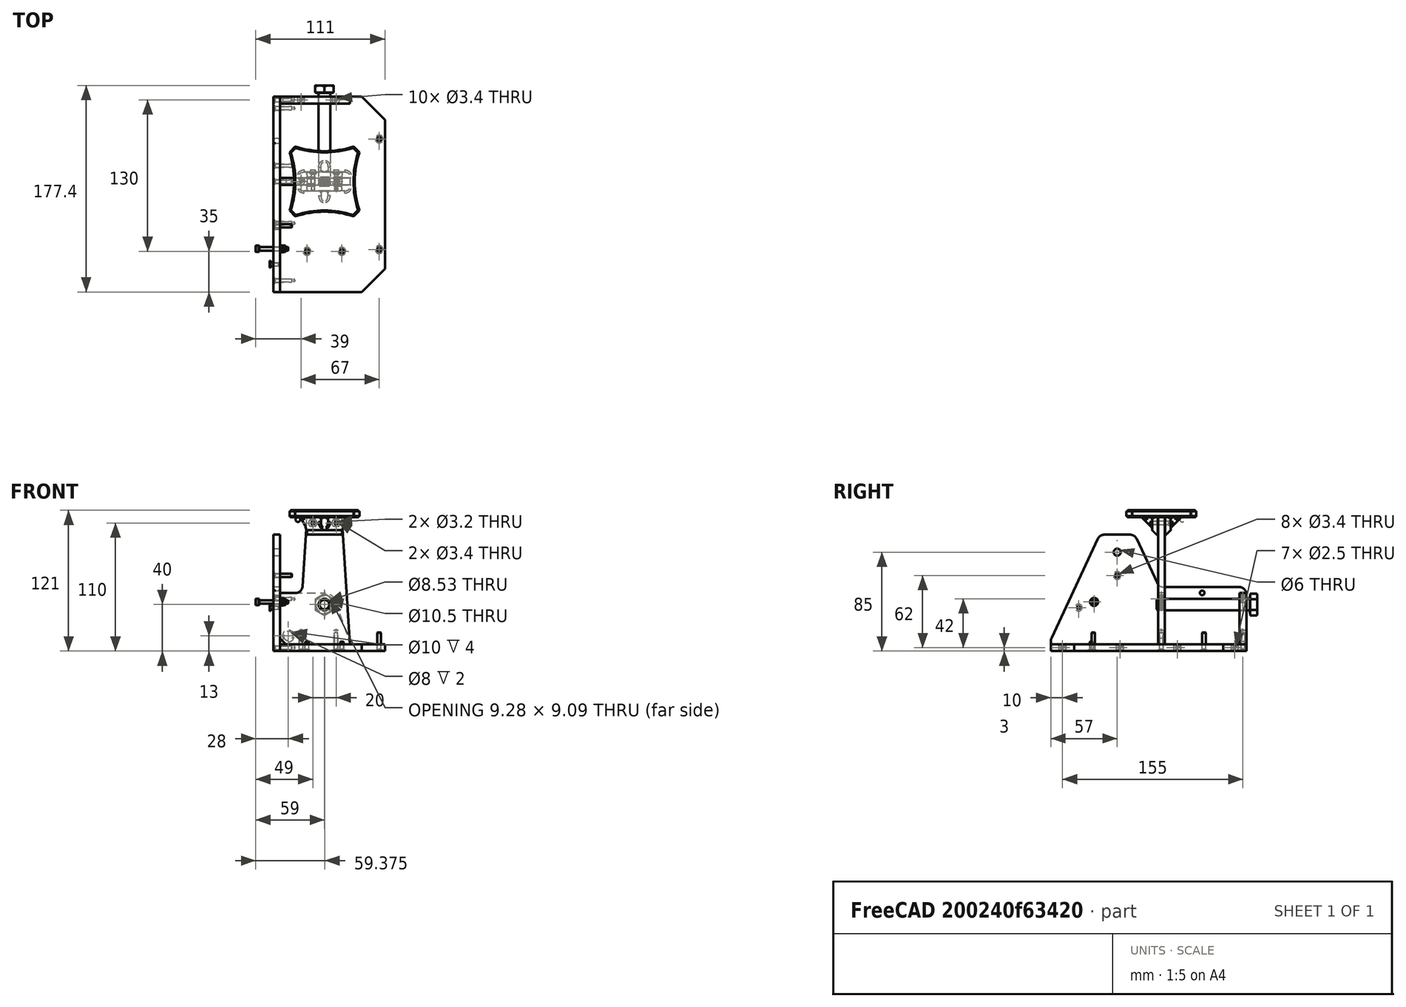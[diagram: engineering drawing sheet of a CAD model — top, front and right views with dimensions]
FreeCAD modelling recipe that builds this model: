
FCSTD DOCUMENT  (FreeCAD 0.20R28730 (Git))
Label: OpenSolder Stand
License: All rights reserved
LicenseURL: http://en.wikipedia.org/wiki/All_rights_reserved
objects: TechDraw::DrawViewBalloon×31, Sketcher::SketchObject×27, Part::FeaturePython×22, PartDesign::CoordinateSystem×21, App::Link×16, App::DocumentObjectGroup×15, PartDesign::Line×15, PartDesign::Hole×12, PartDesign::Pad×6, App::LinkElement×6, PartDesign::Body×5, PartDesign::Chamfer×5, PartDesign::Fillet×5, Spreadsheet::Sheet×5, PartDesign::Pocket×3, TechDraw::DrawSVGTemplate×3, TechDraw::DrawProjGroupItem×3, TechDraw::DrawViewPart×3, TechDraw::DrawViewDimension×3, TechDraw::DrawPage×3, +5 more types
note: 152 computed .brp shape members not serialized (recipe doc carries the construction recipe); baked Part::Feature solids carry a one-line shape summary decoded from their .brp
EXTERNAL_REF file=Parts/Tip Cleaner.FCStd obj=LCS_Tip_Cleaner_Hole_1
EXTERNAL_REF file=Parts/Tip Cleaner.FCStd obj=Body
EXTERNAL_REF file=Parts/Tip Remover Bracket.FCStd obj=Hole1001
EXTERNAL_REF file=Parts/Tip Remover Bracket.FCStd obj=Body
EXTERNAL_REF file=Parts/Tool Holder Washer.FCStd obj=Center
EXTERNAL_REF file=Parts/Tool Holder Washer.FCStd obj=Body
EXTERNAL_REF file=Parts/Tool Holder Screw.FCStd obj=LCS_1
EXTERNAL_REF file=Parts/Tool Holder Washer.FCStd obj=Center2
EXTERNAL_REF file=Parts/Tool Holder Screw.FCStd obj=Body
EXTERNAL_REF file=Parts/Tool Holder Adapter.FCStd obj=Mounting_face_main_hole
EXTERNAL_REF file=Parts/Tool Holder Adapter.FCStd obj=Body
EXTERNAL_REF file=Parts/Tool Holder.FCStd obj=LCS_1
EXTERNAL_REF file=Parts/Tool Holder Adapter.FCStd obj=Holder
EXTERNAL_REF file=Parts/Tool Holder.FCStd obj=Body
EXTERNAL_REF file=Parts/Tip Magazine.FCStd obj=Hole1
EXTERNAL_REF file=Parts/Tip Magazine.FCStd obj=Body009
EXTERNAL_REF file=Parts/Spool Dummy.FCStd obj=LCS_1
EXTERNAL_REF file=Parts/Spool Dummy.FCStd obj=Body
EXTERNAL_REF file=Parts/Spool Knob.FCStd obj=LCS_1
EXTERNAL_REF file=Parts/Spool Knob.FCStd obj=Body
EXTERNAL_REF file=Parts/Connector Minijack MJ-064H.FCStd obj=LCS_1
EXTERNAL_REF file=Parts/Connector Minijack MJ-064H.FCStd obj=Body
EXTERNAL_REF file=Parts/Tip Dummy.FCStd obj=Remover
EXTERNAL_REF file=Parts/Tip Remover Bracket.FCStd obj=LCS_Tip_Remover_Bracket_Tip_Attachment
EXTERNAL_REF file=Parts/Tip Dummy.FCStd obj=Body
EXTERNAL_REF file=Parts/Tip Dummy.FCStd obj=Tip_base
EXTERNAL_REF file=Parts/Tip Magazine.FCStd obj=Holder_pos_1
EXTERNAL_REF file=Parts/Tip Remover Bracket.FCStd obj=LCS_Tip_Remover_Bracket_Hole_2_Outside
EXTERNAL_REF file=Parts/Spool Knob.FCStd obj=LCS_Spool_Screw_Knob_2
EXTERNAL_REF file=Parts/Tip Remover Bracket.FCStd obj=LCS_Tip_Remover_Bracket_Hole_1_Outside
EXTERNAL_REF file=Parts/Rubber Pad.FCStd obj=LCS_1
EXTERNAL_REF file=Parts/Rubber Pad.FCStd obj=Body

FEATURE [PartDesign::CoordinateSystem] LCS_Origin
  AttacherType = Attacher::AttachEngine3D
  MapMode = 2
  Support = -> [X_Axis]
FEATURE [App::FeaturePython] Variables  # WARN: FeaturePython — macro-defined, semantics opaque (R4)
  Centerline_Offset = 38
  Front_Edge_Angle = 65
  Handle_Screw_Height = 110
  Hole_Depth = 12
  Length = 168
  Mid_Panel_Offset = -98
  Panel_Thickness = 6
  Spool_Holder_Inside_Length = 64
  Tool_Angle = 20
  Type = App::PropertyContainer
  expr: Mid_Panel_Offset = -(Length - Spool_Holder_Inside_Length - Panel_Thickness)
FEATURE [App::DocumentObjectGroup] Constraints
FEATURE [Sketcher::SketchObject] Sketch014  label="Master_Side_Sketch"
  FullyConstrained = true
  MapMode = 5
  Placement = pos=(0,0,0) rot=(0.57735,0.57735,0.57735;2.0944rad)
  Support = -> [YZ_Plane]
  expr: Constraints[15] = Variables.Length
  expr: Constraints[45] = Variables.Panel_Thickness / 2
  expr: Constraints[48] = Variables.Panel_Thickness / 2
  expr: Constraints[49] = Variables.Spool_Holder_Inside_Length + Variables.Panel_Thickness
  expr: Constraints[82] = Variables.Front_Edge_Angle
  sketch-geometry (31):
    g0: LineSegment StartX=0 StartY=0 StartZ=0 EndX=0 EndY=9.93071 EndZ=0
    g1: LineSegment StartX=0 StartY=9.93071 StartZ=0 EndX=42 EndY=100 EndZ=0
    g2: LineSegment StartX=42 StartY=100 StartZ=0 EndX=72 EndY=100 EndZ=0
    g3: LineSegment StartX=72 StartY=100 StartZ=0 EndX=92.9838 EndY=55 EndZ=0
    g4: LineSegment StartX=92.9838 StartY=55 StartZ=0 EndX=168 EndY=55 EndZ=0
    g5: LineSegment StartX=168 StartY=55 StartZ=0 EndX=168 EndY=0 EndZ=0
    g6: LineSegment StartX=168 StartY=0 StartZ=0 EndX=0 EndY=0 EndZ=0
    g7: Circle CenterX=57 CenterY=85 CenterZ=0 NormalX=0 NormalY=0 NormalZ=1 AngleXU=0 Radius=3
    g8: LineSegment StartX=42 StartY=100 StartZ=0 EndX=57 EndY=85 EndZ=0
    g9: LineSegment StartX=57 StartY=85 StartZ=0 EndX=72 EndY=100 EndZ=0
    g10: LineSegment StartX=92.9838 StartY=55 StartZ=0 EndX=21.0162 EndY=55 EndZ=0
    g11: LineSegment StartX=21.0162 StartY=55 StartZ=0 EndX=57 EndY=85 EndZ=0
    g12: LineSegment StartX=57 StartY=85 StartZ=0 EndX=92.9838 EndY=55 EndZ=0
    g13: Circle CenterX=57 CenterY=65 CenterZ=0 NormalX=0 NormalY=0 NormalZ=1 AngleXU=0 Radius=1.5
    g14: LineSegment StartX=10 StartY=3 StartZ=0 EndX=59.3333 EndY=3 EndZ=0
    g15: LineSegment StartX=59.3333 StartY=3 StartZ=0 EndX=108.667 EndY=3 EndZ=0
    g16: LineSegment StartX=108.667 StartY=3 StartZ=0 EndX=158 EndY=3 EndZ=0
    g17: LineSegment StartX=165 StartY=45 StartZ=0 EndX=95 EndY=45 EndZ=0
    g18: Circle CenterX=95 CenterY=45 CenterZ=0 NormalX=0 NormalY=0 NormalZ=1 AngleXU=0 Radius=1.5
    g19: Circle CenterX=165 CenterY=45 CenterZ=0 NormalX=0 NormalY=0 NormalZ=1 AngleXU=0 Radius=1.5
    g20: Circle CenterX=10 CenterY=3 CenterZ=0 NormalX=0 NormalY=0 NormalZ=1 AngleXU=0 Radius=1.5
    g21: Circle CenterX=59.3333 CenterY=3 CenterZ=0 NormalX=0 NormalY=0 NormalZ=1 AngleXU=0 Radius=1.5
    g22: Circle CenterX=108.667 CenterY=3 CenterZ=0 NormalX=0 NormalY=0 NormalZ=1 AngleXU=0 Radius=1.5
    g23: Circle CenterX=158 CenterY=3 CenterZ=0 NormalX=0 NormalY=0 NormalZ=1 AngleXU=0 Radius=1.5
    g24: Circle CenterX=37.144 CenterY=42.2622 CenterZ=0 NormalX=0 NormalY=0 NormalZ=1 AngleXU=0 Radius=1.5
    g25: Circle CenterX=23.8547 CenterY=37.4253 CenterZ=0 NormalX=0 NormalY=0 NormalZ=1 AngleXU=0 Radius=1.5
    g26: LineSegment StartX=14.7916 StartY=41.6515 StartZ=0 EndX=23.8547 EndY=37.4253 EndZ=0
    g27: LineSegment StartX=23.8547 StartY=37.4253 StartZ=0 EndX=32.9178 EndY=33.1991 EndZ=0
    g28: LineSegment StartX=32.9178 StartY=33.1991 StartZ=0 EndX=37.144 EndY=42.2622 EndZ=0
    g29: LineSegment StartX=130 StartY=45 StartZ=0 EndX=130 EndY=50 EndZ=0
    g30: Circle CenterX=130 CenterY=50 CenterZ=0 NormalX=0 NormalY=0 NormalZ=1 AngleXU=0 Radius=2
  constraints (85):
    c: Coincident(g-1,g0)
    c: PointOnObject(g0,g-2)
    c: Coincident(g0,g1)
    c: Coincident(g1,g2)
    c: Horizontal(g2)
    c: Coincident(g2,g3)
    c: Coincident(g3,g4)
    c: Horizontal(g4)
    c: Coincident(g4,g5)
    c: PointOnObject(g5,g-1)
    c: Vertical(g5)
    c: Coincident(g5,g6)
    c: Coincident(g6,g0)
    c: DistanceY(g0,g0) = 9.93071
    c: DistanceY(g5,g5) = 55
    c: DistanceX(g6,g6) = 168
    c: DistanceX(g2,g2) = 30
    c: DistanceY(g0,g7) = 85
    c: DistanceX(g0,g7) = 57
    c: Diameter(g7) = 6
    c: Coincident(g1,g8)
    c: Coincident(g8,g7)
    c: Coincident(g8,g9)
    c: Coincident(g9,g2)
    c: Equal(g9,g8)
    c: Coincident(g10,g3)
    c: PointOnObject(g10,g1)
    c: Horizontal(g10)
    c: Coincident(g10,g11)
    c: Coincident(g11,g7)
    c: Coincident(g11,g12)
    c: Coincident(g12,g3)
    c: Equal(g12,g11)
    c: Vertical(g13,g7)
    c: Diameter(g13) = 3
    c: DistanceY(g13,g7) = 20
    c: DistanceY(g7,g1) = 15
    c: Horizontal(g14)
    c: Coincident(g14,g15)
    c: Horizontal(g15)
    c: Coincident(g15,g16)
    c: Horizontal(g16)
    c: Horizontal(g17)
    c: Equal(g14,g15)
    c: Equal(g15,g16)
    c: DistanceY(g0,g14) = 3
    c: DistanceX(g0,g14) = 10
    c: DistanceX(g16,g5) = 10
    c: DistanceX(g17,g5) = 3
    c: DistanceX(g17,g17) = 70
    c: DistanceY(g0,g17) = 45
    c: Coincident(g18,g17)
    c: Coincident(g19,g17)
    c: Equal(g19,g18)
    c: Equal(g18,g13)
    c: Coincident(g20,g14)
    c: Coincident(g21,g14)
    c: Coincident(g22,g15)
    c: Coincident(g23,g16)
    c: Equal(g23,g22)
    c: Equal(g22,g21)
    c: Equal(g21,g20)
    c: Equal(g20,g13)
    c: PointOnObject(g26,g1)
    c: Coincident(g26,g25)
    c: Coincident(g26,g27)
    c: Coincident(g27,g28)
    c: Coincident(g28,g24)
    c: Parallel(g26,g27)
    c: Perpendicular(g28,g27)
    c: Perpendicular(g1,g26)
    c: Distance(g26) = 10
    c: Distance(g27) = 10
    c: Equal(g27,g28)
    c: Equal(g25,g24)
    c: Equal(g24,g13)
    c: Distance(g0,g26) = 35
    c: Coincident(g30,g29)
    c: Vertical(g29)
    c: Symmetric(g18,g19,g29)
    c: Diameter(g30) = 4
    c: DistanceY(g29,g29) = 5
    c: Angle(g-1,g1) = 1.13446
    c: DistanceY(g30,g4) = 5
    c: DistanceX(g7,g18) = 38
FEATURE [Sketcher::SketchObject] Master_Top_Sketch
  FullyConstrained = true
  MapMode = 5
  Support = -> [XY_Plane]
  expr: Constraints[42] = Variables.Panel_Thickness / 2
  expr: Constraints[51] = Variables.Length
  expr: Constraints[52] = Variables.Spool_Holder_Inside_Length + Variables.Panel_Thickness
  expr: Constraints[54] = Variables.Centerline_Offset
  sketch-geometry (23):
    g0: LineSegment StartX=0 StartY=168 StartZ=0 EndX=0 EndY=0 EndZ=0
    g1: LineSegment StartX=70 StartY=168 StartZ=0 EndX=0 EndY=168 EndZ=0
    g2: LineSegment StartX=90 StartY=20 StartZ=0 EndX=90 EndY=148 EndZ=0
    g3: LineSegment StartX=0 StartY=0 StartZ=0 EndX=70 EndY=0 EndZ=0
    g4: LineSegment StartX=70 StartY=168 StartZ=0 EndX=90 EndY=148 EndZ=0
    g5: LineSegment StartX=70 StartY=0 StartZ=0 EndX=90 EndY=20 EndZ=0
    g6: LineSegment StartX=90 StartY=20 StartZ=0 EndX=90 EndY=0 EndZ=0
    g7: LineSegment StartX=70 StartY=0 StartZ=0 EndX=90 EndY=0 EndZ=0
    g8: Circle CenterX=85 CenterY=131.5 CenterZ=0 NormalX=0 NormalY=0 NormalZ=1 AngleXU=0 Radius=1.5
    g9: Circle CenterX=85 CenterY=36.5 CenterZ=0 NormalX=0 NormalY=0 NormalZ=1 AngleXU=0 Radius=1.5
    g10: LineSegment StartX=38 StartY=35 StartZ=0 EndX=38 EndY=0 EndZ=0
    g11: Circle CenterX=18 CenterY=165 CenterZ=0 NormalX=0 NormalY=0 NormalZ=1 AngleXU=0 Radius=1.5
    g12: Circle CenterX=48 CenterY=165 CenterZ=0 NormalX=0 NormalY=0 NormalZ=1 AngleXU=0 Radius=1.5
    g13: Circle CenterX=18 CenterY=95 CenterZ=0 NormalX=0 NormalY=0 NormalZ=1 AngleXU=0 Radius=1.5
    g14: Circle CenterX=48 CenterY=95 CenterZ=0 NormalX=0 NormalY=0 NormalZ=1 AngleXU=0 Radius=1.5
    g15: LineSegment StartX=18 StartY=95 StartZ=0 EndX=48 EndY=95 EndZ=0
    g16: LineSegment StartX=48 StartY=95 StartZ=0 EndX=48 EndY=165 EndZ=0
    g17: LineSegment StartX=48 StartY=165 StartZ=0 EndX=18 EndY=165 EndZ=0
    g18: LineSegment StartX=18 StartY=165 StartZ=0 EndX=18 EndY=95 EndZ=0
    g19: LineSegment StartX=85 StartY=36.5 StartZ=0 EndX=85 EndY=131.5 EndZ=0
    g20: LineSegment StartX=85 StartY=84 StartZ=0 EndX=0 EndY=84 EndZ=0
    g21: Circle CenterX=23 CenterY=35 CenterZ=0 NormalX=0 NormalY=0 NormalZ=1 AngleXU=0 Radius=1.5
    g22: Circle CenterX=53 CenterY=35 CenterZ=0 NormalX=0 NormalY=0 NormalZ=1 AngleXU=0 Radius=1.5
  constraints (61):
    c: Coincident(g1,g0)
    c: Coincident(g0,g3)
    c: Coincident(g3,g-1)
    c: Horizontal(g1)
    c: Vertical(g2)
    c: Horizontal(g3)
    c: Coincident(g5,g3)
    c: Vertical(g3,g1)
    c: Coincident(g1,g4)
    c: Coincident(g2,g4)
    c: Coincident(g2,g5)
    c: Equal(g5,g4)
    c: Coincident(g6,g2)
    c: PointOnObject(g6,g-1)
    c: Coincident(g7,g3)
    c: Coincident(g7,g6)
    c: Vertical(g6)
    c: Equal(g7,g6)
    c: DistanceX(g7,g7) = 20
    c: DistanceX(g0,g6) = 90
    c: Vertical(g9,g8)
    c: Vertical(g10)
    c: DistanceY(g10,g10) = 35
    c: DistanceY(g9,g8) = 95
    c: Equal(g9,g8)
    c: DistanceX(g9,g2) = 5
    c: Coincident(g15,g16)
    c: Coincident(g16,g17)
    c: Coincident(g17,g18)
    c: Coincident(g18,g15)
    c: Horizontal(g15)
    c: Horizontal(g17)
    c: Vertical(g16)
    c: Vertical(g18)
    c: Coincident(g15,g13)
    c: Coincident(g16,g12)
    c: Coincident(g14,g15)
    c: Coincident(g11,g17)
    c: Equal(g11,g12)
    c: Equal(g12,g14)
    c: Equal(g14,g13)
    c: Diameter(g11) = 3
    c: DistanceY(g11,g0) = 3
    c: DistanceX(g0,g11) = 18
    c: DistanceX(g17,g17) = 30
    c: Equal(g8,g11)
    c: Coincident(g19,g9)
    c: Coincident(g19,g8)
    c: Horizontal(g20)
    c: Symmetric(g9,g8,g20)
    c: Symmetric(g0,g0,g20)
    c: DistanceY(g0,g0) = 168
    c: DistanceY(g18,g18) = 70
    c: PointOnObject(g0,g-2)
    c: DistanceX(g0,g10) = 38
    c: PointOnObject(g10,g3)
    c: Horizontal(g21,g22)
    c: Symmetric(g21,g22,g10)
    c: DistanceX(g21,g22) = 30
    c: Equal(g22,g21)
    c: Equal(g21,g11)
FEATURE [PartDesign::CoordinateSystem] LCS_0  label="LCS_Base"
  AttacherType = Attacher::AttachEngine3D
  MapMode = 2
  Support = -> [X_Axis001]
FEATURE [Sketcher::SketchObject] Sketch  label="Base_Pad_Sketch"
  FullyConstrained = true
  MapMode = 5
  Support = -> [XY_Plane001]
  expr: Constraints[18] = Master_Top_Sketch.Constraints[18]
  expr: Constraints[19] = Master_Top_Sketch.Constraints[19]
  expr: Constraints[22] = Master_Top_Sketch.Constraints[22]
  expr: Constraints[23] = Master_Top_Sketch.Constraints[23]
  expr: Constraints[25] = Master_Top_Sketch.Constraints[25]
  expr: Constraints[41] = Master_Top_Sketch.Constraints[41]
  expr: Constraints[42] = Master_Top_Sketch.Constraints[42]
  expr: Constraints[43] = Master_Top_Sketch.Constraints[43]
  expr: Constraints[44] = Master_Top_Sketch.Constraints[44]
  expr: Constraints[51] = Master_Top_Sketch.Constraints[51]
  expr: Constraints[52] = Master_Top_Sketch.Constraints[52]
  expr: Constraints[54] = Master_Top_Sketch.Constraints[54]
  expr: Constraints[58] = Master_Top_Sketch.Constraints[58]
  sketch-geometry (23):
    g0: LineSegment StartX=0 StartY=168 StartZ=0 EndX=0 EndY=0 EndZ=0
    g1: LineSegment StartX=70 StartY=168 StartZ=0 EndX=0 EndY=168 EndZ=0
    g2: LineSegment StartX=90 StartY=20 StartZ=0 EndX=90 EndY=148 EndZ=0
    g3: LineSegment StartX=0 StartY=0 StartZ=0 EndX=70 EndY=0 EndZ=0
    g4: LineSegment StartX=70 StartY=168 StartZ=0 EndX=90 EndY=148 EndZ=0
    g5: LineSegment StartX=70 StartY=0 StartZ=0 EndX=90 EndY=20 EndZ=0
    g6: LineSegment StartX=90 StartY=20 StartZ=0 EndX=90 EndY=0 EndZ=0
    g7: LineSegment StartX=70 StartY=0 StartZ=0 EndX=90 EndY=0 EndZ=0
    g8: Circle CenterX=85 CenterY=131.5 CenterZ=0 NormalX=0 NormalY=0 NormalZ=1 AngleXU=0 Radius=1.5
    g9: Circle CenterX=85 CenterY=36.5 CenterZ=0 NormalX=0 NormalY=0 NormalZ=1 AngleXU=0 Radius=1.5
    g10: LineSegment StartX=38 StartY=35 StartZ=0 EndX=38 EndY=0 EndZ=0
    g11: Circle CenterX=18 CenterY=165 CenterZ=0 NormalX=0 NormalY=0 NormalZ=1 AngleXU=0 Radius=1.5
    g12: Circle CenterX=48 CenterY=165 CenterZ=0 NormalX=0 NormalY=0 NormalZ=1 AngleXU=0 Radius=1.5
    g13: Circle CenterX=18 CenterY=95 CenterZ=0 NormalX=0 NormalY=0 NormalZ=1 AngleXU=0 Radius=1.5
    g14: Circle CenterX=48 CenterY=95 CenterZ=0 NormalX=0 NormalY=0 NormalZ=1 AngleXU=0 Radius=1.5
    g15: LineSegment StartX=18 StartY=95 StartZ=0 EndX=48 EndY=95 EndZ=0
    g16: LineSegment StartX=48 StartY=95 StartZ=0 EndX=48 EndY=165 EndZ=0
    g17: LineSegment StartX=48 StartY=165 StartZ=0 EndX=18 EndY=165 EndZ=0
    g18: LineSegment StartX=18 StartY=165 StartZ=0 EndX=18 EndY=95 EndZ=0
    g19: LineSegment StartX=85 StartY=36.5 StartZ=0 EndX=85 EndY=131.5 EndZ=0
    g20: LineSegment StartX=85 StartY=84 StartZ=0 EndX=0 EndY=84 EndZ=0
    g21: Circle CenterX=23 CenterY=35 CenterZ=0 NormalX=0 NormalY=0 NormalZ=1 AngleXU=0 Radius=1.5
    g22: Circle CenterX=53 CenterY=35 CenterZ=0 NormalX=0 NormalY=0 NormalZ=1 AngleXU=0 Radius=1.5
  constraints (61):
    c: Coincident(g1,g0)
    c: Coincident(g0,g3)
    c: Coincident(g3,g-1)
    c: Horizontal(g1)
    c: Vertical(g2)
    c: Horizontal(g3)
    c: Coincident(g5,g3)
    c: Vertical(g3,g1)
    c: Coincident(g1,g4)
    c: Coincident(g2,g4)
    c: Coincident(g2,g5)
    c: Equal(g5,g4)
    c: Coincident(g6,g2)
    c: PointOnObject(g6,g-1)
    c: Coincident(g7,g3)
    c: Coincident(g7,g6)
    c: Vertical(g6)
    c: Equal(g7,g6)
    c: DistanceX(g7,g7) = 20
    c: DistanceX(g0,g6) = 90
    c: Vertical(g9,g8)
    c: Vertical(g10)
    c: DistanceY(g10,g10) = 35
    c: DistanceY(g9,g8) = 95
    c: Equal(g9,g8)
    c: DistanceX(g9,g2) = 5
    c: Coincident(g15,g16)
    c: Coincident(g16,g17)
    c: Coincident(g17,g18)
    c: Coincident(g18,g15)
    c: Horizontal(g15)
    c: Horizontal(g17)
    c: Vertical(g16)
    c: Vertical(g18)
    c: Coincident(g15,g13)
    c: Coincident(g16,g12)
    c: Coincident(g14,g15)
    c: Coincident(g11,g17)
    c: Equal(g11,g12)
    c: Equal(g12,g14)
    c: Equal(g14,g13)
    c: Diameter(g11) = 3
    c: DistanceY(g11,g0) = 3
    c: DistanceX(g0,g11) = 18
    c: DistanceX(g17,g17) = 30
    c: Equal(g8,g11)
    c: Coincident(g19,g9)
    c: Coincident(g19,g8)
    c: Horizontal(g20)
    c: Symmetric(g9,g8,g20)
    c: Symmetric(g0,g0,g20)
    c: DistanceY(g0,g0) = 168
    c: DistanceY(g18,g18) = 70
    c: PointOnObject(g0,g-2)
    c: DistanceX(g0,g10) = 38
    c: PointOnObject(g10,g3)
    c: Horizontal(g21,g22)
    c: Symmetric(g21,g22,g10)
    c: DistanceX(g21,g22) = 30
    c: Equal(g22,g21)
    c: Equal(g21,g11)
FEATURE [PartDesign::Pad] Pad  label="Base_Pad"
  Direction = (0,0,1)
  Length = 6
  Length2 = 100
  Profile = -> Sketch
  ReferenceAxis = -> Sketch [N_Axis]
  Refine = true
  Type = 0
  expr: Length = Variables.Panel_Thickness
FEATURE [PartDesign::CoordinateSystem] LCS_0001  label="LCS_Side"
  AttacherType = Attacher::AttachEngine3D
  MapMode = 2
  Support = -> [X_Axis002]
FEATURE [Sketcher::SketchObject] Sketch015  label="Side_Pad_Sketch"
  FullyConstrained = true
  MapMode = 5
  Placement = pos=(0,0,0) rot=(0.57735,0.57735,0.57735;2.0944rad)
  Support = -> [YZ_Plane002]
  expr: Constraints[14] = Sketch014.Constraints[14]
  expr: Constraints[15] = Sketch014.Constraints[15]
  expr: Constraints[16] = Sketch014.Constraints[16]
  expr: Constraints[17] = Sketch014.Constraints[17]
  expr: Constraints[19] = Sketch014.Constraints[19]
  expr: Constraints[34] = Sketch014.Constraints[34]
  expr: Constraints[35] = Sketch014.Constraints[35]
  expr: Constraints[36] = Sketch014.Constraints[36]
  expr: Constraints[45] = Sketch014.Constraints[45]
  expr: Constraints[46] = Sketch014.Constraints[46]
  expr: Constraints[47] = Sketch014.Constraints[47]
  expr: Constraints[48] = Sketch014.Constraints[48]
  expr: Constraints[49] = Sketch014.Constraints[49]
  expr: Constraints[50] = Sketch014.Constraints[50]
  expr: Constraints[71] = Sketch014.Constraints[71]
  expr: Constraints[72] = Sketch014.Constraints[72]
  expr: Constraints[76] = Sketch014.Constraints[76]
  expr: Constraints[80] = Sketch014.Constraints[80]
  expr: Constraints[82] = Sketch014.Constraints[82]
  expr: Constraints[83] = Sketch014.Constraints[83]
  expr: Constraints[84] = Sketch014.Constraints[84]
  sketch-geometry (31):
    g0: LineSegment StartX=0 StartY=0 StartZ=0 EndX=0 EndY=9.93071 EndZ=0
    g1: LineSegment StartX=0 StartY=9.93071 StartZ=0 EndX=42 EndY=100 EndZ=0
    g2: LineSegment StartX=42 StartY=100 StartZ=0 EndX=72 EndY=100 EndZ=0
    g3: LineSegment StartX=72 StartY=100 StartZ=0 EndX=92.9838 EndY=55 EndZ=0
    g4: LineSegment StartX=92.9838 StartY=55 StartZ=0 EndX=168 EndY=55 EndZ=0
    g5: LineSegment StartX=168 StartY=55 StartZ=0 EndX=168 EndY=0 EndZ=0
    g6: LineSegment StartX=168 StartY=0 StartZ=0 EndX=0 EndY=0 EndZ=0
    g7: Circle CenterX=57 CenterY=85 CenterZ=0 NormalX=0 NormalY=0 NormalZ=1 AngleXU=0 Radius=3
    g8: LineSegment StartX=42 StartY=100 StartZ=0 EndX=57 EndY=85 EndZ=0
    g9: LineSegment StartX=57 StartY=85 StartZ=0 EndX=72 EndY=100 EndZ=0
    g10: LineSegment StartX=92.9838 StartY=55 StartZ=0 EndX=21.0162 EndY=55 EndZ=0
    g11: LineSegment StartX=21.0162 StartY=55 StartZ=0 EndX=57 EndY=85 EndZ=0
    g12: LineSegment StartX=57 StartY=85 StartZ=0 EndX=92.9838 EndY=55 EndZ=0
    g13: Circle CenterX=57 CenterY=65 CenterZ=0 NormalX=0 NormalY=0 NormalZ=1 AngleXU=0 Radius=1.5
    g14: LineSegment StartX=10 StartY=3 StartZ=0 EndX=59.3333 EndY=3 EndZ=0
    g15: LineSegment StartX=59.3333 StartY=3 StartZ=0 EndX=108.667 EndY=3 EndZ=0
    g16: LineSegment StartX=108.667 StartY=3 StartZ=0 EndX=158 EndY=3 EndZ=0
    g17: LineSegment StartX=165 StartY=45 StartZ=0 EndX=95 EndY=45 EndZ=0
    g18: Circle CenterX=95 CenterY=45 CenterZ=0 NormalX=0 NormalY=0 NormalZ=1 AngleXU=0 Radius=1.5
    g19: Circle CenterX=165 CenterY=45 CenterZ=0 NormalX=0 NormalY=0 NormalZ=1 AngleXU=0 Radius=1.5
    g20: Circle CenterX=10 CenterY=3 CenterZ=0 NormalX=0 NormalY=0 NormalZ=1 AngleXU=0 Radius=1.5
    g21: Circle CenterX=59.3333 CenterY=3 CenterZ=0 NormalX=0 NormalY=0 NormalZ=1 AngleXU=0 Radius=1.5
    g22: Circle CenterX=108.667 CenterY=3 CenterZ=0 NormalX=0 NormalY=0 NormalZ=1 AngleXU=0 Radius=1.5
    g23: Circle CenterX=158 CenterY=3 CenterZ=0 NormalX=0 NormalY=0 NormalZ=1 AngleXU=0 Radius=1.5
    g24: Circle CenterX=37.144 CenterY=42.2622 CenterZ=0 NormalX=0 NormalY=0 NormalZ=1 AngleXU=0 Radius=1.5
    g25: Circle CenterX=23.8547 CenterY=37.4253 CenterZ=0 NormalX=0 NormalY=0 NormalZ=1 AngleXU=0 Radius=1.5
    g26: LineSegment StartX=14.7916 StartY=41.6515 StartZ=0 EndX=23.8547 EndY=37.4253 EndZ=0
    g27: LineSegment StartX=23.8547 StartY=37.4253 StartZ=0 EndX=32.9178 EndY=33.1991 EndZ=0
    g28: LineSegment StartX=32.9178 StartY=33.1991 StartZ=0 EndX=37.144 EndY=42.2622 EndZ=0
    g29: LineSegment StartX=130 StartY=45 StartZ=0 EndX=130 EndY=50 EndZ=0
    g30: Circle CenterX=130 CenterY=50 CenterZ=0 NormalX=0 NormalY=0 NormalZ=1 AngleXU=0 Radius=2
  constraints (85):
    c: Coincident(g-1,g0)
    c: PointOnObject(g0,g-2)
    c: Coincident(g0,g1)
    c: Coincident(g1,g2)
    c: Horizontal(g2)
    c: Coincident(g2,g3)
    c: Coincident(g3,g4)
    c: Horizontal(g4)
    c: Coincident(g4,g5)
    c: PointOnObject(g5,g-1)
    c: Vertical(g5)
    c: Coincident(g5,g6)
    c: Coincident(g6,g0)
    c: DistanceY(g0,g0) = 9.93071
    c: DistanceY(g5,g5) = 55
    c: DistanceX(g6,g6) = 168
    c: DistanceX(g2,g2) = 30
    c: DistanceY(g0,g7) = 85
    c: DistanceX(g0,g7) = 57
    c: Diameter(g7) = 6
    c: Coincident(g1,g8)
    c: Coincident(g8,g7)
    c: Coincident(g8,g9)
    c: Coincident(g9,g2)
    c: Equal(g9,g8)
    c: Coincident(g10,g3)
    c: PointOnObject(g10,g1)
    c: Horizontal(g10)
    c: Coincident(g10,g11)
    c: Coincident(g11,g7)
    c: Coincident(g11,g12)
    c: Coincident(g12,g3)
    c: Equal(g12,g11)
    c: Vertical(g13,g7)
    c: Diameter(g13) = 3
    c: DistanceY(g13,g7) = 20
    c: DistanceY(g7,g1) = 15
    c: Horizontal(g14)
    c: Coincident(g14,g15)
    c: Horizontal(g15)
    c: Coincident(g15,g16)
    c: Horizontal(g16)
    c: Horizontal(g17)
    c: Equal(g14,g15)
    c: Equal(g15,g16)
    c: DistanceY(g0,g14) = 3
    c: DistanceX(g0,g14) = 10
    c: DistanceX(g16,g5) = 10
    c: DistanceX(g17,g5) = 3
    c: DistanceX(g17,g17) = 70
    c: DistanceY(g0,g17) = 45
    c: Coincident(g18,g17)
    c: Coincident(g19,g17)
    c: Equal(g19,g18)
    c: Equal(g18,g13)
    c: Coincident(g20,g14)
    c: Coincident(g21,g14)
    c: Coincident(g22,g15)
    c: Coincident(g23,g16)
    c: Equal(g23,g22)
    c: Equal(g22,g21)
    c: Equal(g21,g20)
    c: Equal(g20,g13)
    c: PointOnObject(g26,g1)
    c: Coincident(g26,g25)
    c: Coincident(g26,g27)
    c: Coincident(g27,g28)
    c: Coincident(g28,g24)
    c: Parallel(g26,g27)
    c: Perpendicular(g28,g27)
    c: Perpendicular(g1,g26)
    c: Distance(g26) = 10
    c: Distance(g27) = 10
    c: Equal(g27,g28)
    c: Equal(g25,g24)
    c: Equal(g24,g13)
    c: Distance(g0,g26) = 35
    c: Coincident(g30,g29)
    c: Vertical(g29)
    c: Symmetric(g18,g19,g29)
    c: Diameter(g30) = 4
    c: DistanceY(g29,g29) = 5
    c: Angle(g-1,g1) = 1.13446
    c: DistanceY(g30,g4) = 5
    c: DistanceX(g7,g18) = 38
FEATURE [PartDesign::Pad] Pad001  label="Side_Pad"
  Direction = (1,-2e-16,3e-16)
  Length = 6
  Length2 = 100
  Placement = pos=(0,0,0) rot=(0.57735,0.57735,0.57735;2.0944rad)
  Profile = -> Sketch015
  ReferenceAxis = -> Sketch015 [N_Axis]
  Refine = true
  Reversed = true
  Type = 0
  expr: Length = Variables.Panel_Thickness
FEATURE [PartDesign::CoordinateSystem] LCS_0002  label="LCS_Rear"
  AttacherType = Attacher::AttachEngine3D
  MapMode = 2
  Support = -> [X_Axis003]
FEATURE [Sketcher::SketchObject] Sketch020  label="Rear_Pad_Sketch"
  AttachmentOffset = pos=(0,0,-168) rot=(0,0,1;0rad)
  FullyConstrained = true
  MapMode = 5
  Placement = pos=(0,168,3.73e-14) rot=(1,0,0;1.5708rad)
  Support = -> [XZ_Plane003]
  expr: .AttachmentOffset.Base.z = -Variables.Length
  expr: Constraints[10] = Sketch037.Constraints[10]
  expr: Constraints[11] = Sketch037.Constraints[11]
  expr: Constraints[13] = Sketch037.Constraints[13]
  expr: Constraints[14] = Sketch037.Constraints[14]
  expr: Constraints[15] = Sketch037.Constraints[15]
  expr: Constraints[25] = Sketch037.Constraints[25]
  expr: Constraints[33] = Sketch037.Constraints[33]
  expr: Constraints[34] = Sketch037.Constraints[34]
  expr: Constraints[39] = Sketch037.Constraints[39]
  expr: Constraints[40] = Sketch037.Constraints[40]
  expr: Constraints[41] = Sketch037.Constraints[41]
  expr: Constraints[7] = Sketch037.Constraints[7]
  expr: Constraints[8] = Sketch037.Constraints[8]
  expr: Constraints[9] = Sketch037.Constraints[9]
  sketch-geometry (17):
    g0: LineSegment StartX=0 StartY=6 StartZ=0 EndX=60 EndY=6 EndZ=0
    g1: LineSegment StartX=60 StartY=6 StartZ=0 EndX=53 EndY=115 EndZ=0
    g2: LineSegment StartX=53 StartY=115 StartZ=0 EndX=23 EndY=115 EndZ=0
    g3: LineSegment StartX=0 StartY=50 StartZ=0 EndX=0 EndY=6 EndZ=0
    g4: GeomPoint X=38 Y=115 Z=0
    g5: Circle CenterX=38 CenterY=40 CenterZ=0 NormalX=0 NormalY=0 NormalZ=1 AngleXU=0 Radius=5.25
    g6: LineSegment StartX=19.1863 StartY=55.6155 StartZ=0 EndX=23 EndY=115 EndZ=0
    g7: GeomPoint X=38 Y=348.571 Z=0
    g8: LineSegment StartX=0 StartY=50 StartZ=0 EndX=13.1986 EndY=50 EndZ=0
    g9: ArcOfCircle CenterX=13.1986 CenterY=56 CenterZ=0 NormalX=0 NormalY=0 NormalZ=1 AngleXU=0 Radius=6 StartAngle=4.71239 EndAngle=6.21905
    g10: LineSegment StartX=13.1986 StartY=50 StartZ=0 EndX=38 EndY=50 EndZ=0
    g11: ArcOfCircle CenterX=38 CenterY=40 CenterZ=0 NormalX=0 NormalY=0 NormalZ=1 AngleXU=0 Radius=10 StartAngle=0.324791 EndAngle=1.5708
    g12: LineSegment StartX=47.4772 StartY=43.1911 StartZ=0 EndX=60 EndY=6 EndZ=0
    g13: Circle CenterX=7 CenterY=13 CenterZ=0 NormalX=0 NormalY=0 NormalZ=1 AngleXU=0 Radius=5.25
    g14: Circle CenterX=28 CenterY=110 CenterZ=0 NormalX=0 NormalY=0 NormalZ=1 AngleXU=0 Radius=1.5
    g15: Circle CenterX=48 CenterY=110 CenterZ=0 NormalX=0 NormalY=0 NormalZ=1 AngleXU=0 Radius=1.5
    g16: GeomPoint X=38 Y=110 Z=0
  constraints (42):
    c: PointOnObject(g0,g-2)
    c: Horizontal(g0)
    c: Coincident(g0,g1)
    c: Coincident(g1,g2)
    c: Horizontal(g2)
    c: PointOnObject(g3,g-2)
    c: Coincident(g3,g0)
    c: DistanceY(g-1,g3) = 50
    c: DistanceY(g-1,g0) = 6
    c: DistanceX(g0,g0) = 60
    c: DistanceY(g-1,g2) = 115
    c: DistanceX(g2,g2) = 30
    c: Symmetric(g2,g1,g4)
    c: DistanceX(g-1,g5) = 38
    c: DistanceY(g-1,g5) = 40
    c: Diameter(g5) = 10.5
    c: Vertical(g5,g4)
    c: Coincident(g6,g2)
    c: PointOnObject(g7,g6)
    c: PointOnObject(g7,g1)
    c: Vertical(g7,g4)
    c: Coincident(g3,g8)
    c: Horizontal(g8)
    c: Tangent(g8,g9) = -1.5708
    c: Tangent(g9,g6) = -1.5708
    c: Radius(g9) = 6
    c: Coincident(g8,g10)
    c: Horizontal(g10)
    c: Tangent(g10,g11) = 1.5708
    c: Tangent(g11,g12) = 1.5708
    c: Coincident(g12,g0)
    c: Coincident(g11,g5)
    c: Equal(g13,g5)
    c: DistanceX(g0,g13) = 7
    c: DistanceY(g0,g13) = 7
    c: Horizontal(g14,g15)
    c: Symmetric(g14,g15,g16)
    c: Vertical(g16,g4)
    c: Equal(g14,g15)
    c: Diameter(g14) = 3
    c: DistanceX(g14,g15) = 20
    c: DistanceY(g-1,g14) = 110
FEATURE [PartDesign::Pad] Pad002  label="Rear_Pad"
  Direction = (0,-1,-2e-16)
  Length = 6
  Length2 = 100
  Placement = pos=(0,0,0) rot=(1,0,0;1.5708rad)
  Profile = -> Sketch020
  ReferenceAxis = -> Sketch020 [N_Axis]
  Refine = true
  Type = 0
  expr: Length = Variables.Panel_Thickness
FEATURE [Sketcher::SketchObject] Sketch021  label="Rear_Side_Threaded_Hole_Sketch"
  FullyConstrained = true
  MapMode = 5
  Placement = pos=(0,0,0) rot=(0.57735,0.57735,0.57735;2.0944rad)
  Support = -> [YZ_Plane003]
  expr: Constraints[14] = Sketch014.Constraints[14]
  expr: Constraints[15] = Sketch014.Constraints[15]
  expr: Constraints[16] = Sketch014.Constraints[16]
  expr: Constraints[17] = Sketch014.Constraints[17]
  expr: Constraints[19] = Sketch014.Constraints[19]
  expr: Constraints[34] = Sketch014.Constraints[34]
  expr: Constraints[35] = Sketch014.Constraints[35]
  expr: Constraints[36] = Sketch014.Constraints[36]
  expr: Constraints[45] = Sketch014.Constraints[45]
  expr: Constraints[46] = Sketch014.Constraints[46]
  expr: Constraints[47] = Sketch014.Constraints[47]
  expr: Constraints[48] = Sketch014.Constraints[48]
  expr: Constraints[49] = Sketch014.Constraints[49]
  expr: Constraints[50] = Sketch014.Constraints[50]
  expr: Constraints[71] = Sketch014.Constraints[71]
  expr: Constraints[72] = Sketch014.Constraints[72]
  expr: Constraints[76] = Sketch014.Constraints[76]
  expr: Constraints[80] = Sketch014.Constraints[80]
  expr: Constraints[82] = Sketch014.Constraints[82]
  expr: Constraints[83] = Sketch014.Constraints[83]
  expr: Constraints[84] = Sketch014.Constraints[84]
  sketch-geometry (31):
    g0: LineSegment StartX=0 StartY=0 StartZ=0 EndX=0 EndY=9.93071 EndZ=0
    g1: LineSegment StartX=0 StartY=9.93071 StartZ=0 EndX=42 EndY=100 EndZ=0
    g2: LineSegment StartX=42 StartY=100 StartZ=0 EndX=72 EndY=100 EndZ=0
    g3: LineSegment StartX=72 StartY=100 StartZ=0 EndX=92.9838 EndY=55 EndZ=0
    g4: LineSegment StartX=92.9838 StartY=55 StartZ=0 EndX=168 EndY=55 EndZ=0
    g5: LineSegment StartX=168 StartY=55 StartZ=0 EndX=168 EndY=0 EndZ=0
    g6: LineSegment StartX=168 StartY=0 StartZ=0 EndX=0 EndY=0 EndZ=0
    g7: Circle CenterX=57 CenterY=85 CenterZ=0 NormalX=0 NormalY=0 NormalZ=1 AngleXU=0 Radius=3
    g8: LineSegment StartX=42 StartY=100 StartZ=0 EndX=57 EndY=85 EndZ=0
    g9: LineSegment StartX=57 StartY=85 StartZ=0 EndX=72 EndY=100 EndZ=0
    g10: LineSegment StartX=92.9838 StartY=55 StartZ=0 EndX=21.0162 EndY=55 EndZ=0
    g11: LineSegment StartX=21.0162 StartY=55 StartZ=0 EndX=57 EndY=85 EndZ=0
    g12: LineSegment StartX=57 StartY=85 StartZ=0 EndX=92.9838 EndY=55 EndZ=0
    g13: Circle CenterX=57 CenterY=65 CenterZ=0 NormalX=0 NormalY=0 NormalZ=1 AngleXU=0 Radius=1.5
    g14: LineSegment StartX=10 StartY=3 StartZ=0 EndX=59.3333 EndY=3 EndZ=0
    g15: LineSegment StartX=59.3333 StartY=3 StartZ=0 EndX=108.667 EndY=3 EndZ=0
    g16: LineSegment StartX=108.667 StartY=3 StartZ=0 EndX=158 EndY=3 EndZ=0
    g17: LineSegment StartX=165 StartY=45 StartZ=0 EndX=95 EndY=45 EndZ=0
    g18: Circle CenterX=95 CenterY=45 CenterZ=0 NormalX=0 NormalY=0 NormalZ=1 AngleXU=0 Radius=1.5
    g19: Circle CenterX=165 CenterY=45 CenterZ=0 NormalX=0 NormalY=0 NormalZ=1 AngleXU=0 Radius=1.5
    g20: Circle CenterX=10 CenterY=3 CenterZ=0 NormalX=0 NormalY=0 NormalZ=1 AngleXU=0 Radius=1.5
    g21: Circle CenterX=59.3333 CenterY=3 CenterZ=0 NormalX=0 NormalY=0 NormalZ=1 AngleXU=0 Radius=1.5
    g22: Circle CenterX=108.667 CenterY=3 CenterZ=0 NormalX=0 NormalY=0 NormalZ=1 AngleXU=0 Radius=1.5
    g23: Circle CenterX=158 CenterY=3 CenterZ=0 NormalX=0 NormalY=0 NormalZ=1 AngleXU=0 Radius=1.5
    g24: Circle CenterX=37.144 CenterY=42.2622 CenterZ=0 NormalX=0 NormalY=0 NormalZ=1 AngleXU=0 Radius=1.5
    g25: Circle CenterX=23.8547 CenterY=37.4253 CenterZ=0 NormalX=0 NormalY=0 NormalZ=1 AngleXU=0 Radius=1.5
    g26: LineSegment StartX=14.7916 StartY=41.6515 StartZ=0 EndX=23.8547 EndY=37.4253 EndZ=0
    g27: LineSegment StartX=23.8547 StartY=37.4253 StartZ=0 EndX=32.9178 EndY=33.1991 EndZ=0
    g28: LineSegment StartX=32.9178 StartY=33.1991 StartZ=0 EndX=37.144 EndY=42.2622 EndZ=0
    g29: LineSegment StartX=130 StartY=45 StartZ=0 EndX=130 EndY=50 EndZ=0
    g30: Circle CenterX=130 CenterY=50 CenterZ=0 NormalX=0 NormalY=0 NormalZ=1 AngleXU=0 Radius=2
  constraints (85):
    c: Coincident(g-1,g0)
    c: PointOnObject(g0,g-2)
    c: Coincident(g0,g1)
    c: Coincident(g1,g2)
    c: Horizontal(g2)
    c: Coincident(g2,g3)
    c: Coincident(g3,g4)
    c: Horizontal(g4)
    c: Coincident(g4,g5)
    c: PointOnObject(g5,g-1)
    c: Vertical(g5)
    c: Coincident(g5,g6)
    c: Coincident(g6,g0)
    c: DistanceY(g0,g0) = 9.93071
    c: DistanceY(g5,g5) = 55
    c: DistanceX(g6,g6) = 168
    c: DistanceX(g2,g2) = 30
    c: DistanceY(g0,g7) = 85
    c: DistanceX(g0,g7) = 57
    c: Diameter(g7) = 6
    c: Coincident(g1,g8)
    c: Coincident(g8,g7)
    c: Coincident(g8,g9)
    c: Coincident(g9,g2)
    c: Equal(g9,g8)
    c: Coincident(g10,g3)
    c: PointOnObject(g10,g1)
    c: Horizontal(g10)
    c: Coincident(g10,g11)
    c: Coincident(g11,g7)
    c: Coincident(g11,g12)
    c: Coincident(g12,g3)
    c: Equal(g12,g11)
    c: Vertical(g13,g7)
    c: Diameter(g13) = 3
    c: DistanceY(g13,g7) = 20
    c: DistanceY(g7,g1) = 15
    c: Horizontal(g14)
    c: Coincident(g14,g15)
    c: Horizontal(g15)
    c: Coincident(g15,g16)
    c: Horizontal(g16)
    c: Horizontal(g17)
    c: Equal(g14,g15)
    c: Equal(g15,g16)
    c: DistanceY(g0,g14) = 3
    c: DistanceX(g0,g14) = 10
    c: DistanceX(g16,g5) = 10
    c: DistanceX(g17,g5) = 3
    c: DistanceX(g17,g17) = 70
    c: DistanceY(g0,g17) = 45
    c: Coincident(g18,g17)
    c: Coincident(g19,g17)
    c: Equal(g19,g18)
    c: Equal(g18,g13)
    c: Coincident(g20,g14)
    c: Coincident(g21,g14)
    c: Coincident(g22,g15)
    c: Coincident(g23,g16)
    c: Equal(g23,g22)
    c: Equal(g22,g21)
    c: Equal(g21,g20)
    c: Equal(g20,g13)
    c: PointOnObject(g26,g1)
    c: Coincident(g26,g25)
    c: Coincident(g26,g27)
    c: Coincident(g27,g28)
    c: Coincident(g28,g24)
    c: Parallel(g26,g27)
    c: Perpendicular(g28,g27)
    c: Perpendicular(g1,g26)
    c: Distance(g26) = 10
    c: Distance(g27) = 10
    c: Equal(g27,g28)
    c: Equal(g25,g24)
    c: Equal(g24,g13)
    c: Distance(g0,g26) = 35
    c: Coincident(g30,g29)
    c: Vertical(g29)
    c: Symmetric(g18,g19,g29)
    c: Diameter(g30) = 4
    c: DistanceY(g29,g29) = 5
    c: Angle(g-1,g1) = 1.13446
    c: DistanceY(g30,g4) = 5
    c: DistanceX(g7,g18) = 38
FEATURE [PartDesign::Hole] Hole004  label="Rear_Side_Threaded_Hole"
  BaseFeature = -> Pad002
  CustomThreadClearance = 0
  Depth = 12
  DepthType = 0
  Diameter = 2.5
  DrillForDepth = false
  DrillPoint = 1
  DrillPointAngle = 118
  HoleCutCountersinkAngle = 90
  HoleCutCustomValues = false
  HoleCutDepth = 0
  HoleCutDiameter = 6.1
  HoleCutType = 0
  ModelThread = false
  Placement = pos=(0,0,0) rot=(1,0,0;1.5708rad)
  Profile = -> Sketch021
  Refine = true
  Reversed = true
  Tapered = false
  TaperedAngle = 90
  ThreadClass = 0
  ThreadDepth = 12
  ThreadDepthType = 0
  ThreadDirection = 0
  ThreadFit = 0
  ThreadSize = 9
  ThreadType = 1
  Threaded = true
  UseCustomThreadClearance = false
  expr: Depth = Variables.Hole_Depth
FEATURE [Sketcher::SketchObject] Sketch022  label="Rear_Bottom_Threaded_Hole_Sketch"
  AttachmentOffset = pos=(0,0,6) rot=(0,0,1;0rad)
  FullyConstrained = true
  MapMode = 5
  Placement = pos=(0,0,6) rot=(0,0,1;0rad)
  Support = -> [XY_Plane003]
  expr: .AttachmentOffset.Base.z = Variables.Panel_Thickness
  expr: Constraints[18] = Master_Top_Sketch.Constraints[18]
  expr: Constraints[19] = Master_Top_Sketch.Constraints[19]
  expr: Constraints[22] = Master_Top_Sketch.Constraints[22]
  expr: Constraints[23] = Master_Top_Sketch.Constraints[23]
  expr: Constraints[25] = Master_Top_Sketch.Constraints[25]
  expr: Constraints[41] = Master_Top_Sketch.Constraints[41]
  expr: Constraints[42] = Master_Top_Sketch.Constraints[42]
  expr: Constraints[43] = Master_Top_Sketch.Constraints[43]
  expr: Constraints[44] = Master_Top_Sketch.Constraints[44]
  expr: Constraints[51] = Master_Top_Sketch.Constraints[51]
  expr: Constraints[52] = Master_Top_Sketch.Constraints[52]
  expr: Constraints[54] = Master_Top_Sketch.Constraints[54]
  expr: Constraints[58] = Master_Top_Sketch.Constraints[58]
  sketch-geometry (23):
    g0: LineSegment StartX=0 StartY=168 StartZ=0 EndX=0 EndY=0 EndZ=0
    g1: LineSegment StartX=70 StartY=168 StartZ=0 EndX=0 EndY=168 EndZ=0
    g2: LineSegment StartX=90 StartY=20 StartZ=0 EndX=90 EndY=148 EndZ=0
    g3: LineSegment StartX=0 StartY=0 StartZ=0 EndX=70 EndY=0 EndZ=0
    g4: LineSegment StartX=70 StartY=168 StartZ=0 EndX=90 EndY=148 EndZ=0
    g5: LineSegment StartX=70 StartY=0 StartZ=0 EndX=90 EndY=20 EndZ=0
    g6: LineSegment StartX=90 StartY=20 StartZ=0 EndX=90 EndY=0 EndZ=0
    g7: LineSegment StartX=70 StartY=0 StartZ=0 EndX=90 EndY=0 EndZ=0
    g8: Circle CenterX=85 CenterY=131.5 CenterZ=0 NormalX=0 NormalY=0 NormalZ=1 AngleXU=0 Radius=1.5
    g9: Circle CenterX=85 CenterY=36.5 CenterZ=0 NormalX=0 NormalY=0 NormalZ=1 AngleXU=0 Radius=1.5
    g10: LineSegment StartX=38 StartY=35 StartZ=0 EndX=38 EndY=0 EndZ=0
    g11: Circle CenterX=18 CenterY=165 CenterZ=0 NormalX=0 NormalY=0 NormalZ=1 AngleXU=0 Radius=1.5
    g12: Circle CenterX=48 CenterY=165 CenterZ=0 NormalX=0 NormalY=0 NormalZ=1 AngleXU=0 Radius=1.5
    g13: Circle CenterX=18 CenterY=95 CenterZ=0 NormalX=0 NormalY=0 NormalZ=1 AngleXU=0 Radius=1.5
    g14: Circle CenterX=48 CenterY=95 CenterZ=0 NormalX=0 NormalY=0 NormalZ=1 AngleXU=0 Radius=1.5
    g15: LineSegment StartX=18 StartY=95 StartZ=0 EndX=48 EndY=95 EndZ=0
    g16: LineSegment StartX=48 StartY=95 StartZ=0 EndX=48 EndY=165 EndZ=0
    g17: LineSegment StartX=48 StartY=165 StartZ=0 EndX=18 EndY=165 EndZ=0
    g18: LineSegment StartX=18 StartY=165 StartZ=0 EndX=18 EndY=95 EndZ=0
    g19: LineSegment StartX=85 StartY=36.5 StartZ=0 EndX=85 EndY=131.5 EndZ=0
    g20: LineSegment StartX=85 StartY=84 StartZ=0 EndX=0 EndY=84 EndZ=0
    g21: Circle CenterX=23 CenterY=35 CenterZ=0 NormalX=0 NormalY=0 NormalZ=1 AngleXU=0 Radius=1.5
    g22: Circle CenterX=53 CenterY=35 CenterZ=0 NormalX=0 NormalY=0 NormalZ=1 AngleXU=0 Radius=1.5
  constraints (61):
    c: Coincident(g1,g0)
    c: Coincident(g0,g3)
    c: Coincident(g3,g-1)
    c: Horizontal(g1)
    c: Vertical(g2)
    c: Horizontal(g3)
    c: Coincident(g5,g3)
    c: Vertical(g3,g1)
    c: Coincident(g1,g4)
    c: Coincident(g2,g4)
    c: Coincident(g2,g5)
    c: Equal(g5,g4)
    c: Coincident(g6,g2)
    c: PointOnObject(g6,g-1)
    c: Coincident(g7,g3)
    c: Coincident(g7,g6)
    c: Vertical(g6)
    c: Equal(g7,g6)
    c: DistanceX(g7,g7) = 20
    c: DistanceX(g0,g6) = 90
    c: Vertical(g9,g8)
    c: Vertical(g10)
    c: DistanceY(g10,g10) = 35
    c: DistanceY(g9,g8) = 95
    c: Equal(g9,g8)
    c: DistanceX(g9,g2) = 5
    c: Coincident(g15,g16)
    c: Coincident(g16,g17)
    c: Coincident(g17,g18)
    c: Coincident(g18,g15)
    c: Horizontal(g15)
    c: Horizontal(g17)
    c: Vertical(g16)
    c: Vertical(g18)
    c: Coincident(g15,g13)
    c: Coincident(g16,g12)
    c: Coincident(g14,g15)
    c: Coincident(g11,g17)
    c: Equal(g11,g12)
    c: Equal(g12,g14)
    c: Equal(g14,g13)
    c: Diameter(g11) = 3
    c: DistanceY(g11,g0) = 3
    c: DistanceX(g0,g11) = 18
    c: DistanceX(g17,g17) = 30
    c: Equal(g8,g11)
    c: Coincident(g19,g9)
    c: Coincident(g19,g8)
    c: Horizontal(g20)
    c: Symmetric(g9,g8,g20)
    c: Symmetric(g0,g0,g20)
    c: DistanceY(g0,g0) = 168
    c: DistanceY(g18,g18) = 70
    c: PointOnObject(g0,g-2)
    c: DistanceX(g0,g10) = 38
    c: PointOnObject(g10,g3)
    c: Horizontal(g21,g22)
    c: Symmetric(g21,g22,g10)
    c: DistanceX(g21,g22) = 30
    c: Equal(g22,g21)
    c: Equal(g21,g11)
FEATURE [PartDesign::Hole] Hole005  label="Rear_Bottom_Threaded_Hole"
  BaseFeature = -> Hole004
  CustomThreadClearance = 0
  Depth = 12
  DepthType = 0
  Diameter = 3.4
  DrillForDepth = false
  DrillPoint = 1
  DrillPointAngle = 118
  HoleCutCountersinkAngle = 90
  HoleCutCustomValues = false
  HoleCutDepth = 0
  HoleCutDiameter = 6.1
  HoleCutType = 0
  ModelThread = false
  Placement = pos=(0,0,0) rot=(1,0,0;1.5708rad)
  Profile = -> Sketch022
  Refine = true
  Reversed = true
  Tapered = false
  TaperedAngle = 90
  ThreadClass = 0
  ThreadDepth = 12
  ThreadDepthType = 0
  ThreadDirection = 0
  ThreadFit = 0
  ThreadSize = 9
  ThreadType = 1
  Threaded = false
  UseCustomThreadClearance = false
  expr: Depth = Variables.Hole_Depth
FEATURE [Sketcher::SketchObject] Sketch023  label="Rear_Connector_Hole_Sketch"
  AttachmentOffset = pos=(0,0,-168) rot=(0,0,1;0rad)
  FullyConstrained = true
  MapMode = 5
  Placement = pos=(0,168,3.73e-14) rot=(1,0,0;1.5708rad)
  Support = -> [XZ_Plane003]
  expr: .AttachmentOffset.Base.z = -Variables.Length
  expr: Constraints[10] = Sketch037.Constraints[10]
  expr: Constraints[11] = Sketch037.Constraints[11]
  expr: Constraints[13] = Sketch037.Constraints[13]
  expr: Constraints[14] = Sketch037.Constraints[14]
  expr: Constraints[15] = Sketch037.Constraints[15]
  expr: Constraints[25] = Sketch037.Constraints[25]
  expr: Constraints[33] = Sketch037.Constraints[33]
  expr: Constraints[34] = Sketch037.Constraints[34]
  expr: Constraints[39] = Sketch037.Constraints[39]
  expr: Constraints[40] = Sketch037.Constraints[40]
  expr: Constraints[41] = Sketch037.Constraints[41]
  expr: Constraints[7] = Sketch037.Constraints[7]
  expr: Constraints[8] = Sketch037.Constraints[8]
  expr: Constraints[9] = Sketch037.Constraints[9]
  sketch-geometry (17):
    g0: LineSegment StartX=0 StartY=6 StartZ=0 EndX=60 EndY=6 EndZ=0
    g1: LineSegment StartX=60 StartY=6 StartZ=0 EndX=53 EndY=115 EndZ=0
    g2: LineSegment StartX=53 StartY=115 StartZ=0 EndX=23 EndY=115 EndZ=0
    g3: LineSegment StartX=0 StartY=50 StartZ=0 EndX=0 EndY=6 EndZ=0
    g4: GeomPoint X=38 Y=115 Z=0
    g5: Circle CenterX=38 CenterY=40 CenterZ=0 NormalX=0 NormalY=0 NormalZ=1 AngleXU=0 Radius=5.25
    g6: LineSegment StartX=19.1863 StartY=55.6155 StartZ=0 EndX=23 EndY=115 EndZ=0
    g7: GeomPoint X=38 Y=348.571 Z=0
    g8: LineSegment StartX=0 StartY=50 StartZ=0 EndX=13.1986 EndY=50 EndZ=0
    g9: ArcOfCircle CenterX=13.1986 CenterY=56 CenterZ=0 NormalX=0 NormalY=0 NormalZ=1 AngleXU=0 Radius=6 StartAngle=4.71239 EndAngle=6.21905
    g10: LineSegment StartX=13.1986 StartY=50 StartZ=0 EndX=38 EndY=50 EndZ=0
    g11: ArcOfCircle CenterX=38 CenterY=40 CenterZ=0 NormalX=0 NormalY=0 NormalZ=1 AngleXU=0 Radius=10 StartAngle=0.324791 EndAngle=1.5708
    g12: LineSegment StartX=47.4772 StartY=43.1911 StartZ=0 EndX=60 EndY=6 EndZ=0
    g13: Circle CenterX=7 CenterY=13 CenterZ=0 NormalX=0 NormalY=0 NormalZ=1 AngleXU=0 Radius=5.25
    g14: Circle CenterX=28 CenterY=110 CenterZ=0 NormalX=0 NormalY=0 NormalZ=1 AngleXU=0 Radius=1.5
    g15: Circle CenterX=48 CenterY=110 CenterZ=0 NormalX=0 NormalY=0 NormalZ=1 AngleXU=0 Radius=1.5
    g16: GeomPoint X=38 Y=110 Z=0
  constraints (42):
    c: PointOnObject(g0,g-2)
    c: Horizontal(g0)
    c: Coincident(g0,g1)
    c: Coincident(g1,g2)
    c: Horizontal(g2)
    c: PointOnObject(g3,g-2)
    c: Coincident(g3,g0)
    c: DistanceY(g-1,g3) = 50
    c: DistanceY(g-1,g0) = 6
    c: DistanceX(g0,g0) = 60
    c: DistanceY(g-1,g2) = 115
    c: DistanceX(g2,g2) = 30
    c: Symmetric(g2,g1,g4)
    c: DistanceX(g-1,g5) = 38
    c: DistanceY(g-1,g5) = 40
    c: Diameter(g5) = 10.5
    c: Vertical(g5,g4)
    c: Coincident(g6,g2)
    c: PointOnObject(g7,g6)
    c: PointOnObject(g7,g1)
    c: Vertical(g7,g4)
    c: Coincident(g3,g8)
    c: Horizontal(g8)
    c: Tangent(g8,g9) = -1.5708
    c: Tangent(g9,g6) = -1.5708
    c: Radius(g9) = 6
    c: Coincident(g8,g10)
    c: Horizontal(g10)
    c: Tangent(g10,g11) = 1.5708
    c: Tangent(g11,g12) = 1.5708
    c: Coincident(g12,g0)
    c: Coincident(g11,g5)
    c: Equal(g13,g5)
    c: DistanceX(g0,g13) = 7
    c: DistanceY(g0,g13) = 7
    c: Horizontal(g14,g15)
    c: Symmetric(g14,g15,g16)
    c: Vertical(g16,g4)
    c: Equal(g14,g15)
    c: Diameter(g14) = 3
    c: DistanceX(g14,g15) = 20
    c: DistanceY(g-1,g14) = 110
FEATURE [PartDesign::Hole] Hole006  label="Rear_Connector_Hole"
  BaseFeature = -> Hole005
  CustomThreadClearance = 0
  Depth = 150.785
  DepthType = 1
  Diameter = 8
  DrillForDepth = false
  DrillPoint = 1
  DrillPointAngle = 118
  HoleCutCountersinkAngle = 90
  HoleCutCustomValues = false
  HoleCutDepth = 4
  HoleCutDiameter = 10
  HoleCutType = 1
  ModelThread = false
  Placement = pos=(0,0,0) rot=(1,0,0;1.5708rad)
  Profile = -> Sketch023
  Refine = true
  Reversed = true
  Tapered = false
  TaperedAngle = 90
  ThreadClass = 0
  ThreadDepth = 150.785
  ThreadDepthType = 0
  ThreadDirection = 0
  ThreadFit = 0
  ThreadSize = 0
  ThreadType = 0
  Threaded = false
  UseCustomThreadClearance = false
  expr: HoleCutDepth = Variables.Panel_Thickness - 2
FEATURE [PartDesign::Body] Rear  label="Rear_Panel"
  Group = -> [LCS_0002,Sketch020,Pad002,Sketch021,Hole004,Sketch022,Hole005,Sketch023,Hole006]
  Origin = -> Origin003
  Tip = -> Hole006
FEATURE [PartDesign::CoordinateSystem] LCS_0003  label="LCS_Mid"
  AttacherType = Attacher::AttachEngine3D
  MapMode = 2
  Support = -> [X_Axis004]
FEATURE [Sketcher::SketchObject] Sketch024  label="Mid_Pad_Sketch"
  AttachmentOffset = pos=(0,0,-98) rot=(0,0,1;0rad)
  FullyConstrained = true
  MapMode = 5
  Placement = pos=(0,98,2.18e-14) rot=(1,0,0;1.5708rad)
  Support = -> [XZ_Plane004]
  expr: .AttachmentOffset.Base.z = Variables.Mid_Panel_Offset
  expr: Constraints[10] = Sketch037.Constraints[10]
  expr: Constraints[11] = Sketch037.Constraints[11]
  expr: Constraints[13] = Sketch037.Constraints[13]
  expr: Constraints[14] = Sketch037.Constraints[14]
  expr: Constraints[15] = Sketch037.Constraints[15]
  expr: Constraints[25] = Sketch037.Constraints[25]
  expr: Constraints[33] = Sketch037.Constraints[33]
  expr: Constraints[34] = Sketch037.Constraints[34]
  expr: Constraints[39] = Sketch037.Constraints[39]
  expr: Constraints[40] = Sketch037.Constraints[40]
  expr: Constraints[41] = Sketch037.Constraints[41]
  expr: Constraints[7] = Sketch037.Constraints[7]
  expr: Constraints[8] = Sketch037.Constraints[8]
  expr: Constraints[9] = Sketch037.Constraints[9]
  sketch-geometry (17):
    g0: LineSegment StartX=0 StartY=6 StartZ=0 EndX=60 EndY=6 EndZ=0
    g1: LineSegment StartX=60 StartY=6 StartZ=0 EndX=53 EndY=115 EndZ=0
    g2: LineSegment StartX=53 StartY=115 StartZ=0 EndX=23 EndY=115 EndZ=0
    g3: LineSegment StartX=0 StartY=50 StartZ=0 EndX=0 EndY=6 EndZ=0
    g4: GeomPoint X=38 Y=115 Z=0
    g5: Circle CenterX=38 CenterY=40 CenterZ=0 NormalX=0 NormalY=0 NormalZ=1 AngleXU=0 Radius=5.25
    g6: LineSegment StartX=19.1863 StartY=55.6155 StartZ=0 EndX=23 EndY=115 EndZ=0
    g7: GeomPoint X=38 Y=348.571 Z=0
    g8: LineSegment StartX=0 StartY=50 StartZ=0 EndX=13.1986 EndY=50 EndZ=0
    g9: ArcOfCircle CenterX=13.1986 CenterY=56 CenterZ=0 NormalX=0 NormalY=0 NormalZ=1 AngleXU=0 Radius=6 StartAngle=4.71239 EndAngle=6.21905
    g10: LineSegment StartX=13.1986 StartY=50 StartZ=0 EndX=38 EndY=50 EndZ=0
    g11: ArcOfCircle CenterX=38 CenterY=40 CenterZ=0 NormalX=0 NormalY=0 NormalZ=1 AngleXU=0 Radius=10 StartAngle=0.324791 EndAngle=1.5708
    g12: LineSegment StartX=47.4772 StartY=43.1911 StartZ=0 EndX=60 EndY=6 EndZ=0
    g13: Circle CenterX=7 CenterY=13 CenterZ=0 NormalX=0 NormalY=0 NormalZ=1 AngleXU=0 Radius=5.25
    g14: Circle CenterX=28 CenterY=110 CenterZ=0 NormalX=0 NormalY=0 NormalZ=1 AngleXU=0 Radius=1.5
    g15: Circle CenterX=48 CenterY=110 CenterZ=0 NormalX=0 NormalY=0 NormalZ=1 AngleXU=0 Radius=1.5
    g16: GeomPoint X=38 Y=110 Z=0
  constraints (42):
    c: PointOnObject(g0,g-2)
    c: Horizontal(g0)
    c: Coincident(g0,g1)
    c: Coincident(g1,g2)
    c: Horizontal(g2)
    c: PointOnObject(g3,g-2)
    c: Coincident(g3,g0)
    c: DistanceY(g-1,g3) = 50
    c: DistanceY(g-1,g0) = 6
    c: DistanceX(g0,g0) = 60
    c: DistanceY(g-1,g2) = 115
    c: DistanceX(g2,g2) = 30
    c: Symmetric(g2,g1,g4)
    c: DistanceX(g-1,g5) = 38
    c: DistanceY(g-1,g5) = 40
    c: Diameter(g5) = 10.5
    c: Vertical(g5,g4)
    c: Coincident(g6,g2)
    c: PointOnObject(g7,g6)
    c: PointOnObject(g7,g1)
    c: Vertical(g7,g4)
    c: Coincident(g3,g8)
    c: Horizontal(g8)
    c: Tangent(g8,g9) = -1.5708
    c: Tangent(g9,g6) = -1.5708
    c: Radius(g9) = 6
    c: Coincident(g8,g10)
    c: Horizontal(g10)
    c: Tangent(g10,g11) = 1.5708
    c: Tangent(g11,g12) = 1.5708
    c: Coincident(g12,g0)
    c: Coincident(g11,g5)
    c: Equal(g13,g5)
    c: DistanceX(g0,g13) = 7
    c: DistanceY(g0,g13) = 7
    c: Horizontal(g14,g15)
    c: Symmetric(g14,g15,g16)
    c: Vertical(g16,g4)
    c: Equal(g14,g15)
    c: Diameter(g14) = 3
    c: DistanceX(g14,g15) = 20
    c: DistanceY(g-1,g14) = 110
FEATURE [PartDesign::Pad] Pad003  label="Mid_Pad"
  Direction = (0,-1,-2e-16)
  Length = 6
  Length2 = 100
  Placement = pos=(0,0,0) rot=(1,0,0;1.5708rad)
  Profile = -> Sketch024
  ReferenceAxis = -> Sketch024 [N_Axis]
  Refine = true
  Type = 0
  expr: Length = Variables.Panel_Thickness
FEATURE [Sketcher::SketchObject] Sketch025  label="Mid_Handle_Hole_Sketch"
  AttachmentOffset = pos=(0,0,-98) rot=(0,0,1;0rad)
  FullyConstrained = true
  MapMode = 5
  Placement = pos=(0,98,2.18e-14) rot=(1,0,0;1.5708rad)
  Support = -> [XZ_Plane004]
  expr: .AttachmentOffset.Base.z = Variables.Mid_Panel_Offset
  expr: Constraints[10] = Sketch037.Constraints[10]
  expr: Constraints[11] = Sketch037.Constraints[11]
  expr: Constraints[13] = Sketch037.Constraints[13]
  expr: Constraints[14] = Sketch037.Constraints[14]
  expr: Constraints[15] = Sketch037.Constraints[15]
  expr: Constraints[25] = Sketch037.Constraints[25]
  expr: Constraints[33] = Sketch037.Constraints[33]
  expr: Constraints[34] = Sketch037.Constraints[34]
  expr: Constraints[39] = Sketch037.Constraints[39]
  expr: Constraints[40] = Sketch037.Constraints[40]
  expr: Constraints[41] = Sketch037.Constraints[41]
  expr: Constraints[7] = Sketch037.Constraints[7]
  expr: Constraints[8] = Sketch037.Constraints[8]
  expr: Constraints[9] = Sketch037.Constraints[9]
  sketch-geometry (17):
    g0: LineSegment StartX=0 StartY=6 StartZ=0 EndX=60 EndY=6 EndZ=0
    g1: LineSegment StartX=60 StartY=6 StartZ=0 EndX=53 EndY=115 EndZ=0
    g2: LineSegment StartX=53 StartY=115 StartZ=0 EndX=23 EndY=115 EndZ=0
    g3: LineSegment StartX=0 StartY=50 StartZ=0 EndX=0 EndY=6 EndZ=0
    g4: GeomPoint X=38 Y=115 Z=0
    g5: Circle CenterX=38 CenterY=40 CenterZ=0 NormalX=0 NormalY=0 NormalZ=1 AngleXU=0 Radius=5.25
    g6: LineSegment StartX=19.1863 StartY=55.6155 StartZ=0 EndX=23 EndY=115 EndZ=0
    g7: GeomPoint X=38 Y=348.571 Z=0
    g8: LineSegment StartX=0 StartY=50 StartZ=0 EndX=13.1986 EndY=50 EndZ=0
    g9: ArcOfCircle CenterX=13.1986 CenterY=56 CenterZ=0 NormalX=0 NormalY=0 NormalZ=1 AngleXU=0 Radius=6 StartAngle=4.71239 EndAngle=6.21905
    g10: LineSegment StartX=13.1986 StartY=50 StartZ=0 EndX=38 EndY=50 EndZ=0
    g11: ArcOfCircle CenterX=38 CenterY=40 CenterZ=0 NormalX=0 NormalY=0 NormalZ=1 AngleXU=0 Radius=10 StartAngle=0.324791 EndAngle=1.5708
    g12: LineSegment StartX=47.4772 StartY=43.1911 StartZ=0 EndX=60 EndY=6 EndZ=0
    g13: Circle CenterX=7 CenterY=13 CenterZ=0 NormalX=0 NormalY=0 NormalZ=1 AngleXU=0 Radius=5.25
    g14: Circle CenterX=28 CenterY=110 CenterZ=0 NormalX=0 NormalY=0 NormalZ=1 AngleXU=0 Radius=1.5
    g15: Circle CenterX=48 CenterY=110 CenterZ=0 NormalX=0 NormalY=0 NormalZ=1 AngleXU=0 Radius=1.5
    g16: GeomPoint X=38 Y=110 Z=0
  constraints (42):
    c: PointOnObject(g0,g-2)
    c: Horizontal(g0)
    c: Coincident(g0,g1)
    c: Coincident(g1,g2)
    c: Horizontal(g2)
    c: PointOnObject(g3,g-2)
    c: Coincident(g3,g0)
    c: DistanceY(g-1,g3) = 50
    c: DistanceY(g-1,g0) = 6
    c: DistanceX(g0,g0) = 60
    c: DistanceY(g-1,g2) = 115
    c: DistanceX(g2,g2) = 30
    c: Symmetric(g2,g1,g4)
    c: DistanceX(g-1,g5) = 38
    c: DistanceY(g-1,g5) = 40
    c: Diameter(g5) = 10.5
    c: Vertical(g5,g4)
    c: Coincident(g6,g2)
    c: PointOnObject(g7,g6)
    c: PointOnObject(g7,g1)
    c: Vertical(g7,g4)
    c: Coincident(g3,g8)
    c: Horizontal(g8)
    c: Tangent(g8,g9) = -1.5708
    c: Tangent(g9,g6) = -1.5708
    c: Radius(g9) = 6
    c: Coincident(g8,g10)
    c: Horizontal(g10)
    c: Tangent(g10,g11) = 1.5708
    c: Tangent(g11,g12) = 1.5708
    c: Coincident(g12,g0)
    c: Coincident(g11,g5)
    c: Equal(g13,g5)
    c: DistanceX(g0,g13) = 7
    c: DistanceY(g0,g13) = 7
    c: Horizontal(g14,g15)
    c: Symmetric(g14,g15,g16)
    c: Vertical(g16,g4)
    c: Equal(g14,g15)
    c: Diameter(g14) = 3
    c: DistanceX(g14,g15) = 20
    c: DistanceY(g-1,g14) = 110
FEATURE [PartDesign::Hole] Hole007  label="Mid_Handle_Hole"
  BaseFeature = -> Pad003
  CustomThreadClearance = 0
  Depth = 12
  DepthType = 0
  Diameter = 3.4
  DrillForDepth = false
  DrillPoint = 1
  DrillPointAngle = 118
  HoleCutCountersinkAngle = 90
  HoleCutCustomValues = false
  HoleCutDepth = 0
  HoleCutDiameter = 6.1
  HoleCutType = 0
  ModelThread = false
  Placement = pos=(0,0,0) rot=(1,0,0;1.5708rad)
  Profile = -> Sketch025
  Refine = true
  Reversed = true
  Tapered = false
  TaperedAngle = 90
  ThreadClass = 0
  ThreadDepth = 12
  ThreadDepthType = 0
  ThreadDirection = 0
  ThreadFit = 0
  ThreadSize = 9
  ThreadType = 1
  Threaded = false
  UseCustomThreadClearance = false
  expr: Depth = Variables.Hole_Depth
FEATURE [Sketcher::SketchObject] Sketch026  label="Mid_Side_Threaded_Hole_Sketch"
  FullyConstrained = true
  MapMode = 5
  Placement = pos=(0,0,0) rot=(0.57735,0.57735,0.57735;2.0944rad)
  Support = -> [YZ_Plane004]
  expr: Constraints[14] = Sketch014.Constraints[14]
  expr: Constraints[15] = Sketch014.Constraints[15]
  expr: Constraints[16] = Sketch014.Constraints[16]
  expr: Constraints[17] = Sketch014.Constraints[17]
  expr: Constraints[19] = Sketch014.Constraints[19]
  expr: Constraints[34] = Sketch014.Constraints[34]
  expr: Constraints[35] = Sketch014.Constraints[35]
  expr: Constraints[36] = Sketch014.Constraints[36]
  expr: Constraints[45] = Sketch014.Constraints[45]
  expr: Constraints[46] = Sketch014.Constraints[46]
  expr: Constraints[47] = Sketch014.Constraints[47]
  expr: Constraints[48] = Sketch014.Constraints[48]
  expr: Constraints[49] = Sketch014.Constraints[49]
  expr: Constraints[50] = Sketch014.Constraints[50]
  expr: Constraints[71] = Sketch014.Constraints[71]
  expr: Constraints[72] = Sketch014.Constraints[72]
  expr: Constraints[76] = Sketch014.Constraints[76]
  expr: Constraints[80] = Sketch014.Constraints[80]
  expr: Constraints[82] = Sketch014.Constraints[82]
  expr: Constraints[83] = Sketch014.Constraints[83]
  expr: Constraints[84] = Sketch014.Constraints[84]
  sketch-geometry (31):
    g0: LineSegment StartX=0 StartY=0 StartZ=0 EndX=0 EndY=9.93071 EndZ=0
    g1: LineSegment StartX=0 StartY=9.93071 StartZ=0 EndX=42 EndY=100 EndZ=0
    g2: LineSegment StartX=42 StartY=100 StartZ=0 EndX=72 EndY=100 EndZ=0
    g3: LineSegment StartX=72 StartY=100 StartZ=0 EndX=92.9838 EndY=55 EndZ=0
    g4: LineSegment StartX=92.9838 StartY=55 StartZ=0 EndX=168 EndY=55 EndZ=0
    g5: LineSegment StartX=168 StartY=55 StartZ=0 EndX=168 EndY=0 EndZ=0
    g6: LineSegment StartX=168 StartY=0 StartZ=0 EndX=0 EndY=0 EndZ=0
    g7: Circle CenterX=57 CenterY=85 CenterZ=0 NormalX=0 NormalY=0 NormalZ=1 AngleXU=0 Radius=3
    g8: LineSegment StartX=42 StartY=100 StartZ=0 EndX=57 EndY=85 EndZ=0
    g9: LineSegment StartX=57 StartY=85 StartZ=0 EndX=72 EndY=100 EndZ=0
    g10: LineSegment StartX=92.9838 StartY=55 StartZ=0 EndX=21.0162 EndY=55 EndZ=0
    g11: LineSegment StartX=21.0162 StartY=55 StartZ=0 EndX=57 EndY=85 EndZ=0
    g12: LineSegment StartX=57 StartY=85 StartZ=0 EndX=92.9838 EndY=55 EndZ=0
    g13: Circle CenterX=57 CenterY=65 CenterZ=0 NormalX=0 NormalY=0 NormalZ=1 AngleXU=0 Radius=1.5
    g14: LineSegment StartX=10 StartY=3 StartZ=0 EndX=59.3333 EndY=3 EndZ=0
    g15: LineSegment StartX=59.3333 StartY=3 StartZ=0 EndX=108.667 EndY=3 EndZ=0
    g16: LineSegment StartX=108.667 StartY=3 StartZ=0 EndX=158 EndY=3 EndZ=0
    g17: LineSegment StartX=165 StartY=45 StartZ=0 EndX=95 EndY=45 EndZ=0
    g18: Circle CenterX=95 CenterY=45 CenterZ=0 NormalX=0 NormalY=0 NormalZ=1 AngleXU=0 Radius=1.5
    g19: Circle CenterX=165 CenterY=45 CenterZ=0 NormalX=0 NormalY=0 NormalZ=1 AngleXU=0 Radius=1.5
    g20: Circle CenterX=10 CenterY=3 CenterZ=0 NormalX=0 NormalY=0 NormalZ=1 AngleXU=0 Radius=1.5
    g21: Circle CenterX=59.3333 CenterY=3 CenterZ=0 NormalX=0 NormalY=0 NormalZ=1 AngleXU=0 Radius=1.5
    g22: Circle CenterX=108.667 CenterY=3 CenterZ=0 NormalX=0 NormalY=0 NormalZ=1 AngleXU=0 Radius=1.5
    g23: Circle CenterX=158 CenterY=3 CenterZ=0 NormalX=0 NormalY=0 NormalZ=1 AngleXU=0 Radius=1.5
    g24: Circle CenterX=37.144 CenterY=42.2622 CenterZ=0 NormalX=0 NormalY=0 NormalZ=1 AngleXU=0 Radius=1.5
    g25: Circle CenterX=23.8547 CenterY=37.4253 CenterZ=0 NormalX=0 NormalY=0 NormalZ=1 AngleXU=0 Radius=1.5
    g26: LineSegment StartX=14.7916 StartY=41.6515 StartZ=0 EndX=23.8547 EndY=37.4253 EndZ=0
    g27: LineSegment StartX=23.8547 StartY=37.4253 StartZ=0 EndX=32.9178 EndY=33.1991 EndZ=0
    g28: LineSegment StartX=32.9178 StartY=33.1991 StartZ=0 EndX=37.144 EndY=42.2622 EndZ=0
    g29: LineSegment StartX=130 StartY=45 StartZ=0 EndX=130 EndY=50 EndZ=0
    g30: Circle CenterX=130 CenterY=50 CenterZ=0 NormalX=0 NormalY=0 NormalZ=1 AngleXU=0 Radius=2
  constraints (85):
    c: Coincident(g-1,g0)
    c: PointOnObject(g0,g-2)
    c: Coincident(g0,g1)
    c: Coincident(g1,g2)
    c: Horizontal(g2)
    c: Coincident(g2,g3)
    c: Coincident(g3,g4)
    c: Horizontal(g4)
    c: Coincident(g4,g5)
    c: PointOnObject(g5,g-1)
    c: Vertical(g5)
    c: Coincident(g5,g6)
    c: Coincident(g6,g0)
    c: DistanceY(g0,g0) = 9.93071
    c: DistanceY(g5,g5) = 55
    c: DistanceX(g6,g6) = 168
    c: DistanceX(g2,g2) = 30
    c: DistanceY(g0,g7) = 85
    c: DistanceX(g0,g7) = 57
    c: Diameter(g7) = 6
    c: Coincident(g1,g8)
    c: Coincident(g8,g7)
    c: Coincident(g8,g9)
    c: Coincident(g9,g2)
    c: Equal(g9,g8)
    c: Coincident(g10,g3)
    c: PointOnObject(g10,g1)
    c: Horizontal(g10)
    c: Coincident(g10,g11)
    c: Coincident(g11,g7)
    c: Coincident(g11,g12)
    c: Coincident(g12,g3)
    c: Equal(g12,g11)
    c: Vertical(g13,g7)
    c: Diameter(g13) = 3
    c: DistanceY(g13,g7) = 20
    c: DistanceY(g7,g1) = 15
    c: Horizontal(g14)
    c: Coincident(g14,g15)
    c: Horizontal(g15)
    c: Coincident(g15,g16)
    c: Horizontal(g16)
    c: Horizontal(g17)
    c: Equal(g14,g15)
    c: Equal(g15,g16)
    c: DistanceY(g0,g14) = 3
    c: DistanceX(g0,g14) = 10
    c: DistanceX(g16,g5) = 10
    c: DistanceX(g17,g5) = 3
    c: DistanceX(g17,g17) = 70
    c: DistanceY(g0,g17) = 45
    c: Coincident(g18,g17)
    c: Coincident(g19,g17)
    c: Equal(g19,g18)
    c: Equal(g18,g13)
    c: Coincident(g20,g14)
    c: Coincident(g21,g14)
    c: Coincident(g22,g15)
    c: Coincident(g23,g16)
    c: Equal(g23,g22)
    c: Equal(g22,g21)
    c: Equal(g21,g20)
    c: Equal(g20,g13)
    c: PointOnObject(g26,g1)
    c: Coincident(g26,g25)
    c: Coincident(g26,g27)
    c: Coincident(g27,g28)
    c: Coincident(g28,g24)
    c: Parallel(g26,g27)
    c: Perpendicular(g28,g27)
    c: Perpendicular(g1,g26)
    c: Distance(g26) = 10
    c: Distance(g27) = 10
    c: Equal(g27,g28)
    c: Equal(g25,g24)
    c: Equal(g24,g13)
    c: Distance(g0,g26) = 35
    c: Coincident(g30,g29)
    c: Vertical(g29)
    c: Symmetric(g18,g19,g29)
    c: Diameter(g30) = 4
    c: DistanceY(g29,g29) = 5
    c: Angle(g-1,g1) = 1.13446
    c: DistanceY(g30,g4) = 5
    c: DistanceX(g7,g18) = 38
FEATURE [PartDesign::Hole] Hole008  label="Mid_Side_Threaded_Hole"
  BaseFeature = -> Hole007
  CustomThreadClearance = 0
  Depth = 12
  DepthType = 0
  Diameter = 2.5
  DrillForDepth = false
  DrillPoint = 1
  DrillPointAngle = 118
  HoleCutCountersinkAngle = 90
  HoleCutCustomValues = false
  HoleCutDepth = 0
  HoleCutDiameter = 6.1
  HoleCutType = 0
  ModelThread = false
  Placement = pos=(0,0,0) rot=(1,0,0;1.5708rad)
  Profile = -> Sketch026
  Refine = true
  Reversed = true
  Tapered = false
  TaperedAngle = 90
  ThreadClass = 0
  ThreadDepth = 12
  ThreadDepthType = 0
  ThreadDirection = 0
  ThreadFit = 0
  ThreadSize = 9
  ThreadType = 1
  Threaded = true
  UseCustomThreadClearance = false
  expr: Depth = Variables.Hole_Depth
FEATURE [Sketcher::SketchObject] Sketch027  label="Mid_Bottom_Threaded_Hole_Sketch"
  AttachmentOffset = pos=(0,0,6) rot=(0,0,1;0rad)
  FullyConstrained = true
  MapMode = 5
  Placement = pos=(0,0,6) rot=(0,0,1;0rad)
  Support = -> [XY_Plane004]
  expr: .AttachmentOffset.Base.z = Variables.Panel_Thickness
  expr: Constraints[18] = Master_Top_Sketch.Constraints[18]
  expr: Constraints[19] = Master_Top_Sketch.Constraints[19]
  expr: Constraints[22] = Master_Top_Sketch.Constraints[22]
  expr: Constraints[23] = Master_Top_Sketch.Constraints[23]
  expr: Constraints[25] = Master_Top_Sketch.Constraints[25]
  expr: Constraints[41] = Master_Top_Sketch.Constraints[41]
  expr: Constraints[42] = Master_Top_Sketch.Constraints[42]
  expr: Constraints[43] = Master_Top_Sketch.Constraints[43]
  expr: Constraints[44] = Master_Top_Sketch.Constraints[44]
  expr: Constraints[51] = Master_Top_Sketch.Constraints[51]
  expr: Constraints[52] = Master_Top_Sketch.Constraints[52]
  expr: Constraints[54] = Master_Top_Sketch.Constraints[54]
  expr: Constraints[58] = Master_Top_Sketch.Constraints[58]
  sketch-geometry (23):
    g0: LineSegment StartX=0 StartY=168 StartZ=0 EndX=0 EndY=0 EndZ=0
    g1: LineSegment StartX=70 StartY=168 StartZ=0 EndX=0 EndY=168 EndZ=0
    g2: LineSegment StartX=90 StartY=20 StartZ=0 EndX=90 EndY=148 EndZ=0
    g3: LineSegment StartX=0 StartY=0 StartZ=0 EndX=70 EndY=0 EndZ=0
    g4: LineSegment StartX=70 StartY=168 StartZ=0 EndX=90 EndY=148 EndZ=0
    g5: LineSegment StartX=70 StartY=0 StartZ=0 EndX=90 EndY=20 EndZ=0
    g6: LineSegment StartX=90 StartY=20 StartZ=0 EndX=90 EndY=0 EndZ=0
    g7: LineSegment StartX=70 StartY=0 StartZ=0 EndX=90 EndY=0 EndZ=0
    g8: Circle CenterX=85 CenterY=131.5 CenterZ=0 NormalX=0 NormalY=0 NormalZ=1 AngleXU=0 Radius=1.5
    g9: Circle CenterX=85 CenterY=36.5 CenterZ=0 NormalX=0 NormalY=0 NormalZ=1 AngleXU=0 Radius=1.5
    g10: LineSegment StartX=38 StartY=35 StartZ=0 EndX=38 EndY=0 EndZ=0
    g11: Circle CenterX=18 CenterY=165 CenterZ=0 NormalX=0 NormalY=0 NormalZ=1 AngleXU=0 Radius=1.5
    g12: Circle CenterX=48 CenterY=165 CenterZ=0 NormalX=0 NormalY=0 NormalZ=1 AngleXU=0 Radius=1.5
    g13: Circle CenterX=18 CenterY=95 CenterZ=0 NormalX=0 NormalY=0 NormalZ=1 AngleXU=0 Radius=1.5
    g14: Circle CenterX=48 CenterY=95 CenterZ=0 NormalX=0 NormalY=0 NormalZ=1 AngleXU=0 Radius=1.5
    g15: LineSegment StartX=18 StartY=95 StartZ=0 EndX=48 EndY=95 EndZ=0
    g16: LineSegment StartX=48 StartY=95 StartZ=0 EndX=48 EndY=165 EndZ=0
    g17: LineSegment StartX=48 StartY=165 StartZ=0 EndX=18 EndY=165 EndZ=0
    g18: LineSegment StartX=18 StartY=165 StartZ=0 EndX=18 EndY=95 EndZ=0
    g19: LineSegment StartX=85 StartY=36.5 StartZ=0 EndX=85 EndY=131.5 EndZ=0
    g20: LineSegment StartX=85 StartY=84 StartZ=0 EndX=0 EndY=84 EndZ=0
    g21: Circle CenterX=23 CenterY=35 CenterZ=0 NormalX=0 NormalY=0 NormalZ=1 AngleXU=0 Radius=1.5
    g22: Circle CenterX=53 CenterY=35 CenterZ=0 NormalX=0 NormalY=0 NormalZ=1 AngleXU=0 Radius=1.5
  constraints (61):
    c: Coincident(g1,g0)
    c: Coincident(g0,g3)
    c: Coincident(g3,g-1)
    c: Horizontal(g1)
    c: Vertical(g2)
    c: Horizontal(g3)
    c: Coincident(g5,g3)
    c: Vertical(g3,g1)
    c: Coincident(g1,g4)
    c: Coincident(g2,g4)
    c: Coincident(g2,g5)
    c: Equal(g5,g4)
    c: Coincident(g6,g2)
    c: PointOnObject(g6,g-1)
    c: Coincident(g7,g3)
    c: Coincident(g7,g6)
    c: Vertical(g6)
    c: Equal(g7,g6)
    c: DistanceX(g7,g7) = 20
    c: DistanceX(g0,g6) = 90
    c: Vertical(g9,g8)
    c: Vertical(g10)
    c: DistanceY(g10,g10) = 35
    c: DistanceY(g9,g8) = 95
    c: Equal(g9,g8)
    c: DistanceX(g9,g2) = 5
    c: Coincident(g15,g16)
    c: Coincident(g16,g17)
    c: Coincident(g17,g18)
    c: Coincident(g18,g15)
    c: Horizontal(g15)
    c: Horizontal(g17)
    c: Vertical(g16)
    c: Vertical(g18)
    c: Coincident(g15,g13)
    c: Coincident(g16,g12)
    c: Coincident(g14,g15)
    c: Coincident(g11,g17)
    c: Equal(g11,g12)
    c: Equal(g12,g14)
    c: Equal(g14,g13)
    c: Diameter(g11) = 3
    c: DistanceY(g11,g0) = 3
    c: DistanceX(g0,g11) = 18
    c: DistanceX(g17,g17) = 30
    c: Equal(g8,g11)
    c: Coincident(g19,g9)
    c: Coincident(g19,g8)
    c: Horizontal(g20)
    c: Symmetric(g9,g8,g20)
    c: Symmetric(g0,g0,g20)
    c: DistanceY(g0,g0) = 168
    c: DistanceY(g18,g18) = 70
    c: PointOnObject(g0,g-2)
    c: DistanceX(g0,g10) = 38
    c: PointOnObject(g10,g3)
    c: Horizontal(g21,g22)
    c: Symmetric(g21,g22,g10)
    c: DistanceX(g21,g22) = 30
    c: Equal(g22,g21)
    c: Equal(g21,g11)
FEATURE [PartDesign::Hole] Hole009  label="Mid_Bottom_Threaded_Hole"
  BaseFeature = -> Hole008
  CustomThreadClearance = 0
  Depth = 12
  DepthType = 0
  Diameter = 2.5
  DrillForDepth = false
  DrillPoint = 1
  DrillPointAngle = 118
  HoleCutCountersinkAngle = 90
  HoleCutCustomValues = false
  HoleCutDepth = 0
  HoleCutDiameter = 6.1
  HoleCutType = 0
  ModelThread = false
  Placement = pos=(0,0,0) rot=(1,0,0;1.5708rad)
  Profile = -> Sketch027
  Refine = true
  Reversed = true
  Tapered = false
  TaperedAngle = 90
  ThreadClass = 0
  ThreadDepth = 12
  ThreadDepthType = 0
  ThreadDirection = 0
  ThreadFit = 0
  ThreadSize = 9
  ThreadType = 1
  Threaded = true
  UseCustomThreadClearance = false
  expr: Depth = Variables.Hole_Depth
FEATURE [Sketcher::SketchObject] Sketch030  label="Mid_Spool_Threaded_Hole_Sketch"
  AttachmentOffset = pos=(0,0,-98) rot=(0,0,1;0rad)
  FullyConstrained = true
  MapMode = 5
  Placement = pos=(0,98,2.18e-14) rot=(1,0,0;1.5708rad)
  Support = -> [XZ_Plane004]
  expr: .AttachmentOffset.Base.z = Variables.Mid_Panel_Offset
  expr: Constraints[10] = Sketch037.Constraints[10]
  expr: Constraints[11] = Sketch037.Constraints[11]
  expr: Constraints[13] = Sketch037.Constraints[13]
  expr: Constraints[14] = Sketch037.Constraints[14]
  expr: Constraints[15] = Sketch037.Constraints[15]
  expr: Constraints[25] = Sketch037.Constraints[25]
  expr: Constraints[33] = Sketch037.Constraints[33]
  expr: Constraints[34] = Sketch037.Constraints[34]
  expr: Constraints[39] = Sketch037.Constraints[39]
  expr: Constraints[40] = Sketch037.Constraints[40]
  expr: Constraints[41] = Sketch037.Constraints[41]
  expr: Constraints[7] = Sketch037.Constraints[7]
  expr: Constraints[8] = Sketch037.Constraints[8]
  expr: Constraints[9] = Sketch037.Constraints[9]
  sketch-geometry (17):
    g0: LineSegment StartX=0 StartY=6 StartZ=0 EndX=60 EndY=6 EndZ=0
    g1: LineSegment StartX=60 StartY=6 StartZ=0 EndX=53 EndY=115 EndZ=0
    g2: LineSegment StartX=53 StartY=115 StartZ=0 EndX=23 EndY=115 EndZ=0
    g3: LineSegment StartX=0 StartY=50 StartZ=0 EndX=0 EndY=6 EndZ=0
    g4: GeomPoint X=38 Y=115 Z=0
    g5: Circle CenterX=38 CenterY=40 CenterZ=0 NormalX=0 NormalY=0 NormalZ=1 AngleXU=0 Radius=5.25
    g6: LineSegment StartX=19.1863 StartY=55.6155 StartZ=0 EndX=23 EndY=115 EndZ=0
    g7: GeomPoint X=38 Y=348.571 Z=0
    g8: LineSegment StartX=0 StartY=50 StartZ=0 EndX=13.1986 EndY=50 EndZ=0
    g9: ArcOfCircle CenterX=13.1986 CenterY=56 CenterZ=0 NormalX=0 NormalY=0 NormalZ=1 AngleXU=0 Radius=6 StartAngle=4.71239 EndAngle=6.21905
    g10: LineSegment StartX=13.1986 StartY=50 StartZ=0 EndX=38 EndY=50 EndZ=0
    g11: ArcOfCircle CenterX=38 CenterY=40 CenterZ=0 NormalX=0 NormalY=0 NormalZ=1 AngleXU=0 Radius=10 StartAngle=0.324791 EndAngle=1.5708
    g12: LineSegment StartX=47.4772 StartY=43.1911 StartZ=0 EndX=60 EndY=6 EndZ=0
    g13: Circle CenterX=7 CenterY=13 CenterZ=0 NormalX=0 NormalY=0 NormalZ=1 AngleXU=0 Radius=5.25
    g14: Circle CenterX=28 CenterY=110 CenterZ=0 NormalX=0 NormalY=0 NormalZ=1 AngleXU=0 Radius=1.5
    g15: Circle CenterX=48 CenterY=110 CenterZ=0 NormalX=0 NormalY=0 NormalZ=1 AngleXU=0 Radius=1.5
    g16: GeomPoint X=38 Y=110 Z=0
  constraints (42):
    c: PointOnObject(g0,g-2)
    c: Horizontal(g0)
    c: Coincident(g0,g1)
    c: Coincident(g1,g2)
    c: Horizontal(g2)
    c: PointOnObject(g3,g-2)
    c: Coincident(g3,g0)
    c: DistanceY(g-1,g3) = 50
    c: DistanceY(g-1,g0) = 6
    c: DistanceX(g0,g0) = 60
    c: DistanceY(g-1,g2) = 115
    c: DistanceX(g2,g2) = 30
    c: Symmetric(g2,g1,g4)
    c: DistanceX(g-1,g5) = 38
    c: DistanceY(g-1,g5) = 40
    c: Diameter(g5) = 10.5
    c: Vertical(g5,g4)
    c: Coincident(g6,g2)
    c: PointOnObject(g7,g6)
    c: PointOnObject(g7,g1)
    c: Vertical(g7,g4)
    c: Coincident(g3,g8)
    c: Horizontal(g8)
    c: Tangent(g8,g9) = -1.5708
    c: Tangent(g9,g6) = -1.5708
    c: Radius(g9) = 6
    c: Coincident(g8,g10)
    c: Horizontal(g10)
    c: Tangent(g10,g11) = 1.5708
    c: Tangent(g11,g12) = 1.5708
    c: Coincident(g12,g0)
    c: Coincident(g11,g5)
    c: Equal(g13,g5)
    c: DistanceX(g0,g13) = 7
    c: DistanceY(g0,g13) = 7
    c: Horizontal(g14,g15)
    c: Symmetric(g14,g15,g16)
    c: Vertical(g16,g4)
    c: Equal(g14,g15)
    c: Diameter(g14) = 3
    c: DistanceX(g14,g15) = 20
    c: DistanceY(g-1,g14) = 110
FEATURE [PartDesign::Hole] Hole011  label="Mid_Spool_Threaded_Hole"
  BaseFeature = -> Hole009
  CustomThreadClearance = 0
  Depth = 12
  DepthType = 0
  Diameter = 8.532
  DrillForDepth = false
  DrillPoint = 1
  DrillPointAngle = 118
  HoleCutCountersinkAngle = 90
  HoleCutCustomValues = false
  HoleCutDepth = 0
  HoleCutDiameter = 8.6
  HoleCutType = 0
  ModelThread = true
  Placement = pos=(0,0,0) rot=(1,0,0;1.5708rad)
  Profile = -> Sketch030
  Refine = true
  Reversed = true
  Tapered = false
  TaperedAngle = 90
  ThreadClass = 0
  ThreadDepth = 12
  ThreadDepthType = 0
  ThreadDirection = 0
  ThreadFit = 0
  ThreadSize = 18
  ThreadType = 1
  Threaded = true
  UseCustomThreadClearance = false
  expr: Depth = Variables.Panel_Thickness * 2
FEATURE [PartDesign::Chamfer] Chamfer  label="Cable_Pass_Chamfer"
  Angle = 45
  Base = -> Hole011 [Edge1]
  BaseFeature = -> Hole011
  ChamferType = 0
  FlipDirection = false
  Placement = pos=(0,0,0) rot=(1,0,0;1.5708rad)
  Refine = true
  Size = 5
  Size2 = 1
  SupportTransform = false
  UseAllEdges = false
FEATURE [PartDesign::Chamfer] Chamfer001  label="Handle_Clearance_Chamfer"
  Angle = 45
  Base = -> Chamfer [Edge10,Edge26]
  BaseFeature = -> Chamfer
  ChamferType = 0
  FlipDirection = false
  Placement = pos=(0,0,0) rot=(1,0,0;1.5708rad)
  Refine = true
  Size = 1
  Size2 = 1
  SupportTransform = false
  UseAllEdges = false
FEATURE [PartDesign::Body] Handle  label="Mid_Panel"
  Group = -> [LCS_0003,Sketch024,Pad003,Sketch025,Hole007,Sketch026,Hole008,Sketch027,Hole009,Sketch030,Hole011,Chamfer,Chamfer001]
  Origin = -> Origin004
  Tip = -> Chamfer001
FEATURE [PartDesign::CoordinateSystem] LCS_0004  label="LCS_Handle"
  AttacherType = Attacher::AttachEngine3D
  MapMode = 2
  Support = -> [X_Axis005]
FEATURE [Sketcher::SketchObject] Sketch031  label="Handle_Pad_Sketch"
  FullyConstrained = true
  MapMode = 5
  Placement = pos=(0,0,0) rot=(0.57735,0.57735,0.57735;2.0944rad)
  Support = -> [YZ_Plane005]
  expr: Constraints[25] = Variables.Panel_Thickness + 0.1
  sketch-geometry (12):
    g0: LineSegment StartX=3.05 StartY=-15 StartZ=0 EndX=8.05 EndY=-15 EndZ=0
    g1: LineSegment StartX=8.05 StartY=-15 StartZ=0 EndX=8.05 EndY=0 EndZ=0
    g2: LineSegment StartX=8.05 StartY=0 StartZ=0 EndX=30 EndY=0 EndZ=0
    g3: LineSegment StartX=30 StartY=0 StartZ=0 EndX=30 EndY=6 EndZ=0
    g4: LineSegment StartX=3.05 StartY=-15 StartZ=0 EndX=3.05 EndY=0 EndZ=0
    g5: LineSegment StartX=3.05 StartY=0 StartZ=0 EndX=-3.05 EndY=0 EndZ=0
    g6: LineSegment StartX=-3.05 StartY=0 StartZ=0 EndX=-3.05 EndY=-15 EndZ=0
    g7: LineSegment StartX=-3.05 StartY=-15 StartZ=0 EndX=-8.05 EndY=-15 EndZ=0
    g8: LineSegment StartX=-8.05 StartY=-15 StartZ=0 EndX=-8.05 EndY=0 EndZ=0
    g9: LineSegment StartX=-8.05 StartY=0 StartZ=0 EndX=-30 EndY=0 EndZ=0
    g10: LineSegment StartX=-30 StartY=0 StartZ=0 EndX=-30 EndY=6 EndZ=0
    g11: LineSegment StartX=-30 StartY=6 StartZ=0 EndX=30 EndY=6 EndZ=0
  constraints (34):
    c: Horizontal(g0)
    c: Vertical(g1)
    c: Coincident(g1,g2)
    c: Horizontal(g2)
    c: Coincident(g2,g3)
    c: Vertical(g3)
    c: Coincident(g0,g1)
    c: Coincident(g4,g0)
    c: Coincident(g4,g5)
    c: Coincident(g5,g6)
    c: Vertical(g6)
    c: Coincident(g6,g7)
    c: Horizontal(g7)
    c: Coincident(g7,g8)
    c: Vertical(g8)
    c: Coincident(g8,g9)
    c: Coincident(g9,g10)
    c: Coincident(g10,g11)
    c: Coincident(g11,g3)
    c: Horizontal(g11)
    c: Horizontal(g8,g5)
    c: Horizontal(g4,g1)
    c: Horizontal(g6,g0)
    c: Vertical(g10)
    c: DistanceX(g11,g11) = 60
    c: DistanceX(g5,g5) = 6.1
    c: DistanceX(g0,g0) = 5
    c: Equal(g0,g7)
    c: DistanceY(g3,g3) = 6
    c: DistanceY(g1,g1) = 15
    c: Vertical(g4)
    c: Horizontal(g9)
    c: Symmetric(g5,g4,g-1)
    c: Symmetric(g9,g2,g-2)
FEATURE [PartDesign::Pad] Pad004  label="Handle_Pad"
  Direction = (1,-2e-16,3e-16)
  Length = 60
  Length2 = 10
  Midplane = true
  Placement = pos=(0,0,0) rot=(0.57735,0.57735,0.57735;2.0944rad)
  Profile = -> Sketch031
  ReferenceAxis = -> Sketch031 [N_Axis]
  Refine = true
  Type = 0
FEATURE [Sketcher::SketchObject] Sketch032  label="Pocket001_Sketch"
  ExternalGeometry = -> [Pad004]
  FullyConstrained = true
  MapMode = 5
  Placement = pos=(0,0,0) rot=(1,0,0;1.5708rad)
  Support = -> [XZ_Plane005]
  sketch-geometry (10):
    g0: Circle CenterX=10 CenterY=-5 CenterZ=0 NormalX=0 NormalY=0 NormalZ=1 AngleXU=0 Radius=1.25
    g1: Circle CenterX=-10 CenterY=-5 CenterZ=0 NormalX=0 NormalY=0 NormalZ=1 AngleXU=0 Radius=1.25
    g2: ArcOfCircle CenterX=34.5714 CenterY=-15 CenterZ=0 NormalX=0 NormalY=0 NormalZ=1 AngleXU=0 Radius=19.5714 StartAngle=2.26834 EndAngle=3.14159
    g3: LineSegment StartX=30 StartY=-2.096e-13 StartZ=0 EndX=30 EndY=-15 EndZ=0
    g4: LineSegment StartX=30 StartY=-15 StartZ=0 EndX=15 EndY=-15 EndZ=0
    g5: LineSegment StartX=22 StartY=-2.096e-13 StartZ=0 EndX=30 EndY=-2.096e-13 EndZ=0
    g6: ArcOfCircle CenterX=-34.5714 CenterY=-15 CenterZ=0 NormalX=0 NormalY=0 NormalZ=1 AngleXU=0 Radius=19.5714 StartAngle=1.5e-15 EndAngle=0.873254
    g7: LineSegment StartX=-15 StartY=-15 StartZ=0 EndX=-30 EndY=-15 EndZ=0
    g8: LineSegment StartX=-30 StartY=-15 StartZ=0 EndX=-30 EndY=-2.345e-13 EndZ=0
    g9: LineSegment StartX=-30 StartY=-2.345e-13 StartZ=0 EndX=-22 EndY=-2.345e-13 EndZ=0
  constraints (27):
    c: Coincident(g4,g2) = 4.71239
    c: Coincident(g3,g4)
    c: PointOnObject(g2,g4)
    c: Horizontal(g4)
    c: Coincident(g3,g-3)
    c: DistanceX(g-1,g2) = 15
    c: Coincident(g5,g2)
    c: Coincident(g5,g3)
    c: Horizontal(g5)
    c: Coincident(g3,g-4)
    c: DistanceX(g5,g5) = 8
    c: Coincident(g6,g7)
    c: Coincident(g7,g8)
    c: Coincident(g8,g-4)
    c: Coincident(g8,g9)
    c: Coincident(g9,g6)
    c: Horizontal(g9)
    c: Horizontal(g7)
    c: Coincident(g7,g-3)
    c: Equal(g7,g4)
    c: Equal(g9,g5)
    c: Equal(g2,g6)
    c: DistanceX(g1,g0) = 20
    c: Equal(g0,g1)
    c: Diameter(g0) = 2.5
    c: Symmetric(g1,g0,g-2)
    c: DistanceY(g1,g-1) = 5
FEATURE [PartDesign::Pocket] Pocket001
  BaseFeature = -> Pad004
  Direction = (0,1,2e-16)
  Length = 5
  Length2 = 5
  Midplane = true
  Placement = pos=(0,0,0) rot=(0.57735,0.57735,0.57735;2.0944rad)
  Profile = -> Sketch032
  ReferenceAxis = -> Sketch032 [N_Axis]
  Refine = true
  Type = 1
FEATURE [Sketcher::SketchObject] Sketch033  label="Pocket002_Sketch"
  ExternalGeometry = -> [Pocket001]
  FullyConstrained = true
  MapMode = 5
  Placement = pos=(0,0,0) rot=(1,0,0;1.5708rad)
  Support = -> [XZ_Plane005]
  sketch-geometry (2):
    g0: Circle CenterX=-10 CenterY=-5 CenterZ=0 NormalX=0 NormalY=0 NormalZ=1 AngleXU=0 Radius=1.6
    g1: Circle CenterX=10 CenterY=-5 CenterZ=0 NormalX=0 NormalY=0 NormalZ=1 AngleXU=0 Radius=1.6
  constraints (4):
    c: Coincident(g0,g-3)
    c: Coincident(g1,g-4)
    c: Equal(g1,g0)
    c: Diameter(g1) = 3.2
FEATURE [PartDesign::Pocket] Pocket002
  BaseFeature = -> Pocket001
  Direction = (0,1,2e-16)
  Length = 5
  Length2 = 5
  Placement = pos=(0,0,0) rot=(0.57735,0.57735,0.57735;2.0944rad)
  Profile = -> Sketch033
  ReferenceAxis = -> Sketch033 [N_Axis]
  Refine = true
  Type = 1
FEATURE [Sketcher::SketchObject] Sketch034  label="Rib_Pad_Sketch"
  ExternalGeometry = -> [Pocket002]
  FullyConstrained = true
  MapMode = 5
  Placement = pos=(0,0,0) rot=(0.57735,0.57735,0.57735;2.0944rad)
  Support = -> [YZ_Plane005]
  sketch-geometry (6):
    g0: LineSegment StartX=8.05 StartY=-9 StartZ=0 EndX=17.05 EndY=-2.167e-13 EndZ=0
    g1: LineSegment StartX=17.05 StartY=-2.167e-13 StartZ=0 EndX=8.05 EndY=-2.167e-13 EndZ=0
    g2: LineSegment StartX=8.05 StartY=-2.167e-13 StartZ=0 EndX=8.05 EndY=-9 EndZ=0
    g3: LineSegment StartX=-8.05 StartY=-9 StartZ=0 EndX=-17.05 EndY=-2.167e-13 EndZ=0
    g4: LineSegment StartX=-17.05 StartY=-2.167e-13 StartZ=0 EndX=-8.05 EndY=-2.167e-13 EndZ=0
    g5: LineSegment StartX=-8.05 StartY=-2.167e-13 StartZ=0 EndX=-8.05 EndY=-9 EndZ=0
  constraints (16):
    c: Coincident(g0,g1)
    c: Horizontal(g1)
    c: Coincident(g2,g0)
    c: Coincident(g3,g4)
    c: Horizontal(g4)
    c: Coincident(g4,g5)
    c: Coincident(g5,g3)
    c: Equal(g2,g1)
    c: Equal(g1,g5)
    c: Equal(g5,g4)
    c: DistanceY(g2,g2) = 9
    c: Coincident(g2,g1)
    c: Vertical(g5)
    c: Vertical(g2)
    c: Coincident(g4,g-4)
    c: Coincident(g-3,g1)
FEATURE [PartDesign::Pad] Pad005  label="Rib_Pad"
  BaseFeature = -> Pocket002
  Direction = (1,-2e-16,3e-16)
  Length = 6
  Length2 = 10
  Midplane = true
  Placement = pos=(0,0,0) rot=(0.57735,0.57735,0.57735;2.0944rad)
  Profile = -> Sketch034
  ReferenceAxis = -> Sketch034 [N_Axis]
  Refine = true
  Type = 0
FEATURE [Sketcher::SketchObject] Sketch035  label="Pocket003_Sketch"
  ExternalGeometry = -> [Pad005]
  FullyConstrained = true
  MapMode = 5
  Support = -> [XY_Plane005]
  sketch-geometry (13):
    g0: ArcOfCircle CenterX=-106.125 CenterY=3.53e-14 CenterZ=0 NormalX=0 NormalY=0 NormalZ=1 AngleXU=0 Radius=80.125 StartAngle=5.96587 EndAngle=6.6005
    g1: ArcOfCircle CenterX=106.125 CenterY=3.53e-14 CenterZ=0 NormalX=0 NormalY=0 NormalZ=1 AngleXU=0 Radius=80.125 StartAngle=2.82428 EndAngle=3.4589
    g2: ArcOfCircle CenterX=0 CenterY=106.125 CenterZ=0 NormalX=0 NormalY=0 NormalZ=1 AngleXU=0 Radius=80.125 StartAngle=4.39508 EndAngle=5.0297
    g3: ArcOfCircle CenterX=0 CenterY=-106.125 CenterZ=0 NormalX=0 NormalY=0 NormalZ=1 AngleXU=0 Radius=80.125 StartAngle=1.25349 EndAngle=1.88811
    g4: GeomPoint X=0 Y=3.53e-14 Z=0
    g5: GeomPoint X=-30 Y=3.53e-14 Z=0
    g6: GeomPoint X=-26 Y=3.53e-14 Z=0
    g7: GeomPoint X=0 Y=26 Z=0
    g8: Circle CenterX=0 CenterY=0 CenterZ=0 NormalX=0 NormalY=0 NormalZ=1 AngleXU=0 Radius=75
    g9: LineSegment StartX=-30 StartY=-25 StartZ=0 EndX=-25 EndY=-30 EndZ=0
    g10: LineSegment StartX=25 StartY=-30 StartZ=0 EndX=30 EndY=-25 EndZ=0
    g11: LineSegment StartX=25 StartY=30 StartZ=0 EndX=30 EndY=25 EndZ=0
    g12: LineSegment StartX=-30 StartY=25 StartZ=0 EndX=-25 EndY=30 EndZ=0
  constraints (34):
    c: PointOnObject(g2,g-2)
    c: Horizontal(g2,g2)
    c: PointOnObject(g4,g-2)
    c: Horizontal(g5,g4)
    c: Symmetric(g0,g1,g-2)
    c: Horizontal(g0,g4)
    c: Symmetric(g0,g1,g-2)
    c: Symmetric(g0,g1,g-2)
    c: Symmetric(g2,g3,g4)
    c: Horizontal(g3,g3)
    c: Equal(g3,g2)
    c: PointOnObject(g6,g0)
    c: PointOnObject(g7,g2)
    c: Horizontal(g0,g6)
    c: Vertical(g2,g7)
    c: DistanceY(g7,g2) = 4
    c: DistanceX(g5,g6) = 4
    c: Coincident(g8,g-1)
    c: Diameter(g8) = 150
    c: Coincident(g9,g0)
    c: Coincident(g9,g3)
    c: Coincident(g10,g3)
    c: Coincident(g10,g1)
    c: Coincident(g11,g2)
    c: Coincident(g11,g1)
    c: Coincident(g12,g0)
    c: Coincident(g12,g2)
    c: PointOnObject(g0,g-3)
    c: Symmetric(g-3,g-3,g5)
    c: Angle(g11,g-1) = 0.785398
    c: DistanceY(g0,g-3) = 5
    c: Horizontal(g-3,g2)
    c: Vertical(g0,g0)
    c: Perpendicular(g10,g9)
FEATURE [PartDesign::Pocket] Pocket003
  BaseFeature = -> Pad005
  Direction = (0,0,-1)
  Length = 5
  Length2 = 5
  Placement = pos=(0,0,0) rot=(0.57735,0.57735,0.57735;2.0944rad)
  Profile = -> Sketch035
  ReferenceAxis = -> Sketch035 [N_Axis]
  Refine = true
  Reversed = true
  Type = 1
FEATURE [PartDesign::Chamfer] Chamfer002  label="CS_Hole_Chamfer"
  Angle = 45
  Base = -> Pocket003 [Edge53,Edge54]
  BaseFeature = -> Pocket003
  ChamferType = 0
  FlipDirection = false
  Placement = pos=(0,0,0) rot=(0.57735,0.57735,0.57735;2.0944rad)
  Refine = true
  Size = 2
  Size2 = 1
  SupportTransform = false
  UseAllEdges = false
FEATURE [PartDesign::Chamfer] Chamfer003  label="Blend_Chamfer"
  Angle = 45
  Base = -> Chamfer002 [Edge9,Edge70]
  BaseFeature = -> Chamfer002
  ChamferType = 0
  FlipDirection = false
  Placement = pos=(0,0,0) rot=(0.57735,0.57735,0.57735;2.0944rad)
  Refine = true
  Size = 4
  Size2 = 1
  SupportTransform = false
  UseAllEdges = false
FEATURE [PartDesign::Chamfer] Chamfer004  label="Grip_Chamfer"
  Angle = 45
  Base = -> Chamfer003 [Face30,Edge21,Edge23,Edge22,Edge19,Edge17,Edge24,Edge20,Edge18]
  BaseFeature = -> Chamfer003
  ChamferType = 0
  FlipDirection = false
  Placement = pos=(0,0,0) rot=(0.57735,0.57735,0.57735;2.0944rad)
  Refine = true
  Size = 1
  Size2 = 1
  SupportTransform = false
  UseAllEdges = false
FEATURE [PartDesign::Fillet] Fillet002  label="Rib_Fillet_1"
  Base = -> Chamfer004 [Edge50,Edge59,Edge58,Edge41,Edge60,Edge65,Edge75,Edge78]
  BaseFeature = -> Chamfer004
  Placement = pos=(0,0,0) rot=(0.57735,0.57735,0.57735;2.0944rad)
  Radius = 2
  Refine = true
  SupportTransform = false
  UseAllEdges = false
FEATURE [PartDesign::Fillet] Fillet003  label="Brace_Fillet"
  Base = -> Fillet002 [Edge9,Edge4,Edge24,Edge29]
  BaseFeature = -> Fillet002
  Placement = pos=(0,0,0) rot=(0.57735,0.57735,0.57735;2.0944rad)
  Radius = 2
  Refine = true
  SupportTransform = false
  UseAllEdges = false
FEATURE [PartDesign::Fillet] Fillet004  label="Rib_Fillet_2"
  Base = -> Fillet003 [Edge5,Edge31]
  BaseFeature = -> Fillet003
  Placement = pos=(0,0,0) rot=(0.57735,0.57735,0.57735;2.0944rad)
  Radius = 2
  Refine = true
  SupportTransform = false
  UseAllEdges = false
FEATURE [PartDesign::Body] Handle001  label="Handle"
  AssemblyType = Part::Link
  AttachedBy = Origin
  AttachedTo = Parent Assembly#LCS_Assembly_Handle
  Group = -> [LCS_0004,Sketch031,Pad004,Sketch032,Pocket001,Sketch033,Pocket002,Sketch034,Pad005,Sketch035,Pocket003,Chamfer002,Chamfer003,Chamfer004,Fillet002,Fillet003,Fillet004]
  Origin = -> Origin005
  Placement = pos=(38,95,115) rot=(0,0,1;0rad)
  SolverId = Asm4EE
  Tip = -> Fillet004
  expr: Placement = LCS_Assembly_Handle.Placement * AttachmentOffset
FEATURE [Sketcher::SketchObject] Sketch037  label="Master_Front_Sketch"
  AttachmentOffset = pos=(0,0,-98) rot=(0,0,1;0rad)
  FullyConstrained = true
  MapMode = 5
  Placement = pos=(0,98,2.18e-14) rot=(1,0,0;1.5708rad)
  Support = -> [XZ_Plane]
  expr: .AttachmentOffset.Base.z = Variables.Mid_Panel_Offset
  expr: Constraints[10] = Variables.Handle_Screw_Height + 5
  expr: Constraints[13] = Variables.Centerline_Offset
  expr: Constraints[41] = Variables.Handle_Screw_Height
  expr: Constraints[8] = Variables.Panel_Thickness
  sketch-geometry (17):
    g0: LineSegment StartX=0 StartY=6 StartZ=0 EndX=60 EndY=6 EndZ=0
    g1: LineSegment StartX=60 StartY=6 StartZ=0 EndX=53 EndY=115 EndZ=0
    g2: LineSegment StartX=53 StartY=115 StartZ=0 EndX=23 EndY=115 EndZ=0
    g3: LineSegment StartX=0 StartY=50 StartZ=0 EndX=0 EndY=6 EndZ=0
    g4: GeomPoint X=38 Y=115 Z=0
    g5: Circle CenterX=38 CenterY=40 CenterZ=0 NormalX=0 NormalY=0 NormalZ=1 AngleXU=0 Radius=5.25
    g6: LineSegment StartX=19.1863 StartY=55.6155 StartZ=0 EndX=23 EndY=115 EndZ=0
    g7: GeomPoint X=38 Y=348.571 Z=0
    g8: LineSegment StartX=0 StartY=50 StartZ=0 EndX=13.1986 EndY=50 EndZ=0
    g9: ArcOfCircle CenterX=13.1986 CenterY=56 CenterZ=0 NormalX=0 NormalY=0 NormalZ=1 AngleXU=0 Radius=6 StartAngle=4.71239 EndAngle=6.21905
    g10: LineSegment StartX=13.1986 StartY=50 StartZ=0 EndX=38 EndY=50 EndZ=0
    g11: ArcOfCircle CenterX=38 CenterY=40 CenterZ=0 NormalX=0 NormalY=0 NormalZ=1 AngleXU=0 Radius=10 StartAngle=0.324791 EndAngle=1.5708
    g12: LineSegment StartX=47.4772 StartY=43.1911 StartZ=0 EndX=60 EndY=6 EndZ=0
    g13: Circle CenterX=7 CenterY=13 CenterZ=0 NormalX=0 NormalY=0 NormalZ=1 AngleXU=0 Radius=5.25
    g14: Circle CenterX=28 CenterY=110 CenterZ=0 NormalX=0 NormalY=0 NormalZ=1 AngleXU=0 Radius=1.5
    g15: Circle CenterX=48 CenterY=110 CenterZ=0 NormalX=0 NormalY=0 NormalZ=1 AngleXU=0 Radius=1.5
    g16: GeomPoint X=38 Y=110 Z=0
  constraints (42):
    c: PointOnObject(g0,g-2)
    c: Horizontal(g0)
    c: Coincident(g0,g1)
    c: Coincident(g1,g2)
    c: Horizontal(g2)
    c: PointOnObject(g3,g-2)
    c: Coincident(g3,g0)
    c: DistanceY(g-1,g3) = 50
    c: DistanceY(g-1,g0) = 6
    c: DistanceX(g0,g0) = 60
    c: DistanceY(g-1,g2) = 115
    c: DistanceX(g2,g2) = 30
    c: Symmetric(g2,g1,g4)
    c: DistanceX(g-1,g5) = 38
    c: DistanceY(g-1,g5) = 40
    c: Diameter(g5) = 10.5
    c: Vertical(g5,g4)
    c: Coincident(g6,g2)
    c: PointOnObject(g7,g6)
    c: PointOnObject(g7,g1)
    c: Vertical(g7,g4)
    c: Coincident(g3,g8)
    c: Horizontal(g8)
    c: Tangent(g8,g9) = -1.5708
    c: Tangent(g9,g6) = -1.5708
    c: Radius(g9) = 6
    c: Coincident(g8,g10)
    c: Horizontal(g10)
    c: Tangent(g10,g11) = 1.5708
    c: Tangent(g11,g12) = 1.5708
    c: Coincident(g12,g0)
    c: Coincident(g11,g5)
    c: Equal(g13,g5)
    c: DistanceX(g0,g13) = 7
    c: DistanceY(g0,g13) = 7
    c: Horizontal(g14,g15)
    c: Symmetric(g14,g15,g16)
    c: Vertical(g16,g4)
    c: Equal(g14,g15)
    c: Diameter(g14) = 3
    c: DistanceX(g14,g15) = 20
    c: DistanceY(g-1,g14) = 110
FEATURE [Sketcher::SketchObject] Sketch038  label="Base_Bottom_CS_Hole_Sketch"
  FullyConstrained = true
  MapMode = 5
  Support = -> [XY_Plane001]
  expr: Constraints[18] = Master_Top_Sketch.Constraints[18]
  expr: Constraints[19] = Master_Top_Sketch.Constraints[19]
  expr: Constraints[22] = Master_Top_Sketch.Constraints[22]
  expr: Constraints[23] = Master_Top_Sketch.Constraints[23]
  expr: Constraints[25] = Master_Top_Sketch.Constraints[25]
  expr: Constraints[41] = Master_Top_Sketch.Constraints[41]
  expr: Constraints[42] = Master_Top_Sketch.Constraints[42]
  expr: Constraints[43] = Master_Top_Sketch.Constraints[43]
  expr: Constraints[44] = Master_Top_Sketch.Constraints[44]
  expr: Constraints[51] = Master_Top_Sketch.Constraints[51]
  expr: Constraints[52] = Master_Top_Sketch.Constraints[52]
  expr: Constraints[54] = Master_Top_Sketch.Constraints[54]
  expr: Constraints[58] = Master_Top_Sketch.Constraints[58]
  sketch-geometry (23):
    g0: LineSegment StartX=0 StartY=168 StartZ=0 EndX=0 EndY=0 EndZ=0
    g1: LineSegment StartX=70 StartY=168 StartZ=0 EndX=0 EndY=168 EndZ=0
    g2: LineSegment StartX=90 StartY=20 StartZ=0 EndX=90 EndY=148 EndZ=0
    g3: LineSegment StartX=0 StartY=0 StartZ=0 EndX=70 EndY=0 EndZ=0
    g4: LineSegment StartX=70 StartY=168 StartZ=0 EndX=90 EndY=148 EndZ=0
    g5: LineSegment StartX=70 StartY=0 StartZ=0 EndX=90 EndY=20 EndZ=0
    g6: LineSegment StartX=90 StartY=20 StartZ=0 EndX=90 EndY=0 EndZ=0
    g7: LineSegment StartX=70 StartY=0 StartZ=0 EndX=90 EndY=0 EndZ=0
    g8: Circle CenterX=85 CenterY=131.5 CenterZ=0 NormalX=0 NormalY=0 NormalZ=1 AngleXU=0 Radius=1.5
    g9: Circle CenterX=85 CenterY=36.5 CenterZ=0 NormalX=0 NormalY=0 NormalZ=1 AngleXU=0 Radius=1.5
    g10: LineSegment StartX=38 StartY=35 StartZ=0 EndX=38 EndY=0 EndZ=0
    g11: Circle CenterX=18 CenterY=165 CenterZ=0 NormalX=0 NormalY=0 NormalZ=1 AngleXU=0 Radius=1.5
    g12: Circle CenterX=48 CenterY=165 CenterZ=0 NormalX=0 NormalY=0 NormalZ=1 AngleXU=0 Radius=1.5
    g13: Circle CenterX=18 CenterY=95 CenterZ=0 NormalX=0 NormalY=0 NormalZ=1 AngleXU=0 Radius=1.5
    g14: Circle CenterX=48 CenterY=95 CenterZ=0 NormalX=0 NormalY=0 NormalZ=1 AngleXU=0 Radius=1.5
    g15: LineSegment StartX=18 StartY=95 StartZ=0 EndX=48 EndY=95 EndZ=0
    g16: LineSegment StartX=48 StartY=95 StartZ=0 EndX=48 EndY=165 EndZ=0
    g17: LineSegment StartX=48 StartY=165 StartZ=0 EndX=18 EndY=165 EndZ=0
    g18: LineSegment StartX=18 StartY=165 StartZ=0 EndX=18 EndY=95 EndZ=0
    g19: LineSegment StartX=85 StartY=36.5 StartZ=0 EndX=85 EndY=131.5 EndZ=0
    g20: LineSegment StartX=85 StartY=84 StartZ=0 EndX=0 EndY=84 EndZ=0
    g21: Circle CenterX=23 CenterY=35 CenterZ=0 NormalX=0 NormalY=0 NormalZ=1 AngleXU=0 Radius=1.5
    g22: Circle CenterX=53 CenterY=35 CenterZ=0 NormalX=0 NormalY=0 NormalZ=1 AngleXU=0 Radius=1.5
  constraints (61):
    c: Coincident(g1,g0)
    c: Coincident(g0,g3)
    c: Coincident(g3,g-1)
    c: Horizontal(g1)
    c: Vertical(g2)
    c: Horizontal(g3)
    c: Coincident(g5,g3)
    c: Vertical(g3,g1)
    c: Coincident(g1,g4)
    c: Coincident(g2,g4)
    c: Coincident(g2,g5)
    c: Equal(g5,g4)
    c: Coincident(g6,g2)
    c: PointOnObject(g6,g-1)
    c: Coincident(g7,g3)
    c: Coincident(g7,g6)
    c: Vertical(g6)
    c: Equal(g7,g6)
    c: DistanceX(g7,g7) = 20
    c: DistanceX(g0,g6) = 90
    c: Vertical(g9,g8)
    c: Vertical(g10)
    c: DistanceY(g10,g10) = 35
    c: DistanceY(g9,g8) = 95
    c: Equal(g9,g8)
    c: DistanceX(g9,g2) = 5
    c: Coincident(g15,g16)
    c: Coincident(g16,g17)
    c: Coincident(g17,g18)
    c: Coincident(g18,g15)
    c: Horizontal(g15)
    c: Horizontal(g17)
    c: Vertical(g16)
    c: Vertical(g18)
    c: Coincident(g15,g13)
    c: Coincident(g16,g12)
    c: Coincident(g14,g15)
    c: Coincident(g11,g17)
    c: Equal(g11,g12)
    c: Equal(g12,g14)
    c: Equal(g14,g13)
    c: Diameter(g11) = 3
    c: DistanceY(g11,g0) = 3
    c: DistanceX(g0,g11) = 18
    c: DistanceX(g17,g17) = 30
    c: Equal(g8,g11)
    c: Coincident(g19,g9)
    c: Coincident(g19,g8)
    c: Horizontal(g20)
    c: Symmetric(g9,g8,g20)
    c: Symmetric(g0,g0,g20)
    c: DistanceY(g0,g0) = 168
    c: DistanceY(g18,g18) = 70
    c: PointOnObject(g0,g-2)
    c: DistanceX(g0,g10) = 38
    c: PointOnObject(g10,g3)
    c: Horizontal(g21,g22)
    c: Symmetric(g21,g22,g10)
    c: DistanceX(g21,g22) = 30
    c: Equal(g22,g21)
    c: Equal(g21,g11)
FEATURE [PartDesign::Hole] Hole012  label="Base_Bottom_CS_Hole"
  BaseFeature = -> Pad
  CustomThreadClearance = 0
  Depth = 12
  DepthType = 0
  Diameter = 3.4
  DrillForDepth = false
  DrillPoint = 1
  DrillPointAngle = 118
  HoleCutCountersinkAngle = 90
  HoleCutCustomValues = false
  HoleCutDepth = 1.7
  HoleCutDiameter = 6.7
  HoleCutType = 7
  ModelThread = false
  Profile = -> Sketch038
  Refine = true
  Reversed = true
  Tapered = false
  TaperedAngle = 90
  ThreadClass = 0
  ThreadDepth = 12
  ThreadDepthType = 0
  ThreadDirection = 0
  ThreadFit = 0
  ThreadSize = 9
  ThreadType = 1
  Threaded = false
  UseCustomThreadClearance = false
  expr: Depth = Variables.Hole_Depth
FEATURE [Sketcher::SketchObject] Sketch039  label="Base_Side_Threaded_Hole_Sketch"
  FullyConstrained = true
  MapMode = 5
  Placement = pos=(0,0,0) rot=(0.57735,0.57735,0.57735;2.0944rad)
  Support = -> [YZ_Plane001]
  expr: Constraints[14] = Sketch014.Constraints[14]
  expr: Constraints[15] = Sketch014.Constraints[15]
  expr: Constraints[16] = Sketch014.Constraints[16]
  expr: Constraints[17] = Sketch014.Constraints[17]
  expr: Constraints[19] = Sketch014.Constraints[19]
  expr: Constraints[34] = Sketch014.Constraints[34]
  expr: Constraints[35] = Sketch014.Constraints[35]
  expr: Constraints[36] = Sketch014.Constraints[36]
  expr: Constraints[45] = Sketch014.Constraints[45]
  expr: Constraints[46] = Sketch014.Constraints[46]
  expr: Constraints[47] = Sketch014.Constraints[47]
  expr: Constraints[48] = Sketch014.Constraints[48]
  expr: Constraints[49] = Sketch014.Constraints[49]
  expr: Constraints[50] = Sketch014.Constraints[50]
  expr: Constraints[71] = Sketch014.Constraints[71]
  expr: Constraints[72] = Sketch014.Constraints[72]
  expr: Constraints[76] = Sketch014.Constraints[76]
  expr: Constraints[80] = Sketch014.Constraints[80]
  expr: Constraints[82] = Sketch014.Constraints[82]
  expr: Constraints[83] = Sketch014.Constraints[83]
  expr: Constraints[84] = Sketch014.Constraints[84]
  sketch-geometry (31):
    g0: LineSegment StartX=0 StartY=0 StartZ=0 EndX=0 EndY=9.93071 EndZ=0
    g1: LineSegment StartX=0 StartY=9.93071 StartZ=0 EndX=42 EndY=100 EndZ=0
    g2: LineSegment StartX=42 StartY=100 StartZ=0 EndX=72 EndY=100 EndZ=0
    g3: LineSegment StartX=72 StartY=100 StartZ=0 EndX=92.9838 EndY=55 EndZ=0
    g4: LineSegment StartX=92.9838 StartY=55 StartZ=0 EndX=168 EndY=55 EndZ=0
    g5: LineSegment StartX=168 StartY=55 StartZ=0 EndX=168 EndY=0 EndZ=0
    g6: LineSegment StartX=168 StartY=0 StartZ=0 EndX=0 EndY=0 EndZ=0
    g7: Circle CenterX=57 CenterY=85 CenterZ=0 NormalX=0 NormalY=0 NormalZ=1 AngleXU=0 Radius=3
    g8: LineSegment StartX=42 StartY=100 StartZ=0 EndX=57 EndY=85 EndZ=0
    g9: LineSegment StartX=57 StartY=85 StartZ=0 EndX=72 EndY=100 EndZ=0
    g10: LineSegment StartX=92.9838 StartY=55 StartZ=0 EndX=21.0162 EndY=55 EndZ=0
    g11: LineSegment StartX=21.0162 StartY=55 StartZ=0 EndX=57 EndY=85 EndZ=0
    g12: LineSegment StartX=57 StartY=85 StartZ=0 EndX=92.9838 EndY=55 EndZ=0
    g13: Circle CenterX=57 CenterY=65 CenterZ=0 NormalX=0 NormalY=0 NormalZ=1 AngleXU=0 Radius=1.5
    g14: LineSegment StartX=10 StartY=3 StartZ=0 EndX=59.3333 EndY=3 EndZ=0
    g15: LineSegment StartX=59.3333 StartY=3 StartZ=0 EndX=108.667 EndY=3 EndZ=0
    g16: LineSegment StartX=108.667 StartY=3 StartZ=0 EndX=158 EndY=3 EndZ=0
    g17: LineSegment StartX=165 StartY=45 StartZ=0 EndX=95 EndY=45 EndZ=0
    g18: Circle CenterX=95 CenterY=45 CenterZ=0 NormalX=0 NormalY=0 NormalZ=1 AngleXU=0 Radius=1.5
    g19: Circle CenterX=165 CenterY=45 CenterZ=0 NormalX=0 NormalY=0 NormalZ=1 AngleXU=0 Radius=1.5
    g20: Circle CenterX=10 CenterY=3 CenterZ=0 NormalX=0 NormalY=0 NormalZ=1 AngleXU=0 Radius=1.5
    g21: Circle CenterX=59.3333 CenterY=3 CenterZ=0 NormalX=0 NormalY=0 NormalZ=1 AngleXU=0 Radius=1.5
    g22: Circle CenterX=108.667 CenterY=3 CenterZ=0 NormalX=0 NormalY=0 NormalZ=1 AngleXU=0 Radius=1.5
    g23: Circle CenterX=158 CenterY=3 CenterZ=0 NormalX=0 NormalY=0 NormalZ=1 AngleXU=0 Radius=1.5
    g24: Circle CenterX=37.144 CenterY=42.2622 CenterZ=0 NormalX=0 NormalY=0 NormalZ=1 AngleXU=0 Radius=1.5
    g25: Circle CenterX=23.8547 CenterY=37.4253 CenterZ=0 NormalX=0 NormalY=0 NormalZ=1 AngleXU=0 Radius=1.5
    g26: LineSegment StartX=14.7916 StartY=41.6515 StartZ=0 EndX=23.8547 EndY=37.4253 EndZ=0
    g27: LineSegment StartX=23.8547 StartY=37.4253 StartZ=0 EndX=32.9178 EndY=33.1991 EndZ=0
    g28: LineSegment StartX=32.9178 StartY=33.1991 StartZ=0 EndX=37.144 EndY=42.2622 EndZ=0
    g29: LineSegment StartX=130 StartY=45 StartZ=0 EndX=130 EndY=50 EndZ=0
    g30: Circle CenterX=130 CenterY=50 CenterZ=0 NormalX=0 NormalY=0 NormalZ=1 AngleXU=0 Radius=2
  constraints (85):
    c: Coincident(g-1,g0)
    c: PointOnObject(g0,g-2)
    c: Coincident(g0,g1)
    c: Coincident(g1,g2)
    c: Horizontal(g2)
    c: Coincident(g2,g3)
    c: Coincident(g3,g4)
    c: Horizontal(g4)
    c: Coincident(g4,g5)
    c: PointOnObject(g5,g-1)
    c: Vertical(g5)
    c: Coincident(g5,g6)
    c: Coincident(g6,g0)
    c: DistanceY(g0,g0) = 9.93071
    c: DistanceY(g5,g5) = 55
    c: DistanceX(g6,g6) = 168
    c: DistanceX(g2,g2) = 30
    c: DistanceY(g0,g7) = 85
    c: DistanceX(g0,g7) = 57
    c: Diameter(g7) = 6
    c: Coincident(g1,g8)
    c: Coincident(g8,g7)
    c: Coincident(g8,g9)
    c: Coincident(g9,g2)
    c: Equal(g9,g8)
    c: Coincident(g10,g3)
    c: PointOnObject(g10,g1)
    c: Horizontal(g10)
    c: Coincident(g10,g11)
    c: Coincident(g11,g7)
    c: Coincident(g11,g12)
    c: Coincident(g12,g3)
    c: Equal(g12,g11)
    c: Vertical(g13,g7)
    c: Diameter(g13) = 3
    c: DistanceY(g13,g7) = 20
    c: DistanceY(g7,g1) = 15
    c: Horizontal(g14)
    c: Coincident(g14,g15)
    c: Horizontal(g15)
    c: Coincident(g15,g16)
    c: Horizontal(g16)
    c: Horizontal(g17)
    c: Equal(g14,g15)
    c: Equal(g15,g16)
    c: DistanceY(g0,g14) = 3
    c: DistanceX(g0,g14) = 10
    c: DistanceX(g16,g5) = 10
    c: DistanceX(g17,g5) = 3
    c: DistanceX(g17,g17) = 70
    c: DistanceY(g0,g17) = 45
    c: Coincident(g18,g17)
    c: Coincident(g19,g17)
    c: Equal(g19,g18)
    c: Equal(g18,g13)
    c: Coincident(g20,g14)
    c: Coincident(g21,g14)
    c: Coincident(g22,g15)
    c: Coincident(g23,g16)
    c: Equal(g23,g22)
    c: Equal(g22,g21)
    c: Equal(g21,g20)
    c: Equal(g20,g13)
    c: PointOnObject(g26,g1)
    c: Coincident(g26,g25)
    c: Coincident(g26,g27)
    c: Coincident(g27,g28)
    c: Coincident(g28,g24)
    c: Parallel(g26,g27)
    c: Perpendicular(g28,g27)
    c: Perpendicular(g1,g26)
    c: Distance(g26) = 10
    c: Distance(g27) = 10
    c: Equal(g27,g28)
    c: Equal(g25,g24)
    c: Equal(g24,g13)
    c: Distance(g0,g26) = 35
    c: Coincident(g30,g29)
    c: Vertical(g29)
    c: Symmetric(g18,g19,g29)
    c: Diameter(g30) = 4
    c: DistanceY(g29,g29) = 5
    c: Angle(g-1,g1) = 1.13446
    c: DistanceY(g30,g4) = 5
    c: DistanceX(g7,g18) = 38
FEATURE [PartDesign::Hole] Hole013  label="Base_Side_Threaded_Hole"
  BaseFeature = -> Hole012
  CustomThreadClearance = 0
  Depth = 12
  DepthType = 0
  Diameter = 2.5
  DrillForDepth = false
  DrillPoint = 1
  DrillPointAngle = 118
  HoleCutCountersinkAngle = 90
  HoleCutCustomValues = false
  HoleCutDepth = 0
  HoleCutDiameter = 6.7
  HoleCutType = 0
  ModelThread = false
  Profile = -> Sketch039
  Refine = true
  Reversed = true
  Tapered = false
  TaperedAngle = 90
  ThreadClass = 0
  ThreadDepth = 12
  ThreadDepthType = 0
  ThreadDirection = 0
  ThreadFit = 0
  ThreadSize = 9
  ThreadType = 1
  Threaded = true
  UseCustomThreadClearance = false
  expr: Depth = Variables.Hole_Depth
FEATURE [PartDesign::Body] Base  label="Base_Panel"
  Group = -> [LCS_0,Sketch,Pad,Sketch038,Hole012,Sketch039,Hole013]
  Origin = -> Origin001
  Tip = -> Hole013
FEATURE [Sketcher::SketchObject] Sketch040  label="Side_CS_Hole_Sketch"
  AttachmentOffset = pos=(0,0,-6) rot=(0,0,1;0rad)
  FullyConstrained = true
  MapMode = 5
  Placement = pos=(-6,1.3e-15,-1.3e-15) rot=(0.57735,0.57735,0.57735;2.0944rad)
  Support = -> [YZ_Plane002]
  expr: .AttachmentOffset.Base.z = -Variables.Panel_Thickness
  expr: Constraints[14] = Sketch014.Constraints[14]
  expr: Constraints[15] = Sketch014.Constraints[15]
  expr: Constraints[16] = Sketch014.Constraints[16]
  expr: Constraints[17] = Sketch014.Constraints[17]
  expr: Constraints[19] = Sketch014.Constraints[19]
  expr: Constraints[34] = Sketch014.Constraints[34]
  expr: Constraints[35] = Sketch014.Constraints[35]
  expr: Constraints[36] = Sketch014.Constraints[36]
  expr: Constraints[45] = Sketch014.Constraints[45]
  expr: Constraints[46] = Sketch014.Constraints[46]
  expr: Constraints[47] = Sketch014.Constraints[47]
  expr: Constraints[48] = Sketch014.Constraints[48]
  expr: Constraints[49] = Sketch014.Constraints[49]
  expr: Constraints[50] = Sketch014.Constraints[50]
  expr: Constraints[71] = Sketch014.Constraints[71]
  expr: Constraints[72] = Sketch014.Constraints[72]
  expr: Constraints[76] = Sketch014.Constraints[76]
  expr: Constraints[80] = Sketch014.Constraints[80]
  expr: Constraints[82] = Sketch014.Constraints[82]
  expr: Constraints[83] = Sketch014.Constraints[83]
  expr: Constraints[84] = Sketch014.Constraints[84]
  sketch-geometry (31):
    g0: LineSegment StartX=0 StartY=0 StartZ=0 EndX=0 EndY=9.93071 EndZ=0
    g1: LineSegment StartX=0 StartY=9.93071 StartZ=0 EndX=42 EndY=100 EndZ=0
    g2: LineSegment StartX=42 StartY=100 StartZ=0 EndX=72 EndY=100 EndZ=0
    g3: LineSegment StartX=72 StartY=100 StartZ=0 EndX=92.9838 EndY=55 EndZ=0
    g4: LineSegment StartX=92.9838 StartY=55 StartZ=0 EndX=168 EndY=55 EndZ=0
    g5: LineSegment StartX=168 StartY=55 StartZ=0 EndX=168 EndY=0 EndZ=0
    g6: LineSegment StartX=168 StartY=0 StartZ=0 EndX=0 EndY=0 EndZ=0
    g7: Circle CenterX=57 CenterY=85 CenterZ=0 NormalX=0 NormalY=0 NormalZ=1 AngleXU=0 Radius=3
    g8: LineSegment StartX=42 StartY=100 StartZ=0 EndX=57 EndY=85 EndZ=0
    g9: LineSegment StartX=57 StartY=85 StartZ=0 EndX=72 EndY=100 EndZ=0
    g10: LineSegment StartX=92.9838 StartY=55 StartZ=0 EndX=21.0162 EndY=55 EndZ=0
    g11: LineSegment StartX=21.0162 StartY=55 StartZ=0 EndX=57 EndY=85 EndZ=0
    g12: LineSegment StartX=57 StartY=85 StartZ=0 EndX=92.9838 EndY=55 EndZ=0
    g13: Circle CenterX=57 CenterY=65 CenterZ=0 NormalX=0 NormalY=0 NormalZ=1 AngleXU=0 Radius=1.5
    g14: LineSegment StartX=10 StartY=3 StartZ=0 EndX=59.3333 EndY=3 EndZ=0
    g15: LineSegment StartX=59.3333 StartY=3 StartZ=0 EndX=108.667 EndY=3 EndZ=0
    g16: LineSegment StartX=108.667 StartY=3 StartZ=0 EndX=158 EndY=3 EndZ=0
    g17: LineSegment StartX=165 StartY=45 StartZ=0 EndX=95 EndY=45 EndZ=0
    g18: Circle CenterX=95 CenterY=45 CenterZ=0 NormalX=0 NormalY=0 NormalZ=1 AngleXU=0 Radius=1.5
    g19: Circle CenterX=165 CenterY=45 CenterZ=0 NormalX=0 NormalY=0 NormalZ=1 AngleXU=0 Radius=1.5
    g20: Circle CenterX=10 CenterY=3 CenterZ=0 NormalX=0 NormalY=0 NormalZ=1 AngleXU=0 Radius=1.5
    g21: Circle CenterX=59.3333 CenterY=3 CenterZ=0 NormalX=0 NormalY=0 NormalZ=1 AngleXU=0 Radius=1.5
    g22: Circle CenterX=108.667 CenterY=3 CenterZ=0 NormalX=0 NormalY=0 NormalZ=1 AngleXU=0 Radius=1.5
    g23: Circle CenterX=158 CenterY=3 CenterZ=0 NormalX=0 NormalY=0 NormalZ=1 AngleXU=0 Radius=1.5
    g24: Circle CenterX=37.144 CenterY=42.2622 CenterZ=0 NormalX=0 NormalY=0 NormalZ=1 AngleXU=0 Radius=1.5
    g25: Circle CenterX=23.8547 CenterY=37.4253 CenterZ=0 NormalX=0 NormalY=0 NormalZ=1 AngleXU=0 Radius=1.5
    g26: LineSegment StartX=14.7916 StartY=41.6515 StartZ=0 EndX=23.8547 EndY=37.4253 EndZ=0
    g27: LineSegment StartX=23.8547 StartY=37.4253 StartZ=0 EndX=32.9178 EndY=33.1991 EndZ=0
    g28: LineSegment StartX=32.9178 StartY=33.1991 StartZ=0 EndX=37.144 EndY=42.2622 EndZ=0
    g29: LineSegment StartX=130 StartY=45 StartZ=0 EndX=130 EndY=50 EndZ=0
    g30: Circle CenterX=130 CenterY=50 CenterZ=0 NormalX=0 NormalY=0 NormalZ=1 AngleXU=0 Radius=2
  constraints (85):
    c: Coincident(g-1,g0)
    c: PointOnObject(g0,g-2)
    c: Coincident(g0,g1)
    c: Coincident(g1,g2)
    c: Horizontal(g2)
    c: Coincident(g2,g3)
    c: Coincident(g3,g4)
    c: Horizontal(g4)
    c: Coincident(g4,g5)
    c: PointOnObject(g5,g-1)
    c: Vertical(g5)
    c: Coincident(g5,g6)
    c: Coincident(g6,g0)
    c: DistanceY(g0,g0) = 9.93071
    c: DistanceY(g5,g5) = 55
    c: DistanceX(g6,g6) = 168
    c: DistanceX(g2,g2) = 30
    c: DistanceY(g0,g7) = 85
    c: DistanceX(g0,g7) = 57
    c: Diameter(g7) = 6
    c: Coincident(g1,g8)
    c: Coincident(g8,g7)
    c: Coincident(g8,g9)
    c: Coincident(g9,g2)
    c: Equal(g9,g8)
    c: Coincident(g10,g3)
    c: PointOnObject(g10,g1)
    c: Horizontal(g10)
    c: Coincident(g10,g11)
    c: Coincident(g11,g7)
    c: Coincident(g11,g12)
    c: Coincident(g12,g3)
    c: Equal(g12,g11)
    c: Vertical(g13,g7)
    c: Diameter(g13) = 3
    c: DistanceY(g13,g7) = 20
    c: DistanceY(g7,g1) = 15
    c: Horizontal(g14)
    c: Coincident(g14,g15)
    c: Horizontal(g15)
    c: Coincident(g15,g16)
    c: Horizontal(g16)
    c: Horizontal(g17)
    c: Equal(g14,g15)
    c: Equal(g15,g16)
    c: DistanceY(g0,g14) = 3
    c: DistanceX(g0,g14) = 10
    c: DistanceX(g16,g5) = 10
    c: DistanceX(g17,g5) = 3
    c: DistanceX(g17,g17) = 70
    c: DistanceY(g0,g17) = 45
    c: Coincident(g18,g17)
    c: Coincident(g19,g17)
    c: Equal(g19,g18)
    c: Equal(g18,g13)
    c: Coincident(g20,g14)
    c: Coincident(g21,g14)
    c: Coincident(g22,g15)
    c: Coincident(g23,g16)
    c: Equal(g23,g22)
    c: Equal(g22,g21)
    c: Equal(g21,g20)
    c: Equal(g20,g13)
    c: PointOnObject(g26,g1)
    c: Coincident(g26,g25)
    c: Coincident(g26,g27)
    c: Coincident(g27,g28)
    c: Coincident(g28,g24)
    c: Parallel(g26,g27)
    c: Perpendicular(g28,g27)
    c: Perpendicular(g1,g26)
    c: Distance(g26) = 10
    c: Distance(g27) = 10
    c: Equal(g27,g28)
    c: Equal(g25,g24)
    c: Equal(g24,g13)
    c: Distance(g0,g26) = 35
    c: Coincident(g30,g29)
    c: Vertical(g29)
    c: Symmetric(g18,g19,g29)
    c: Diameter(g30) = 4
    c: DistanceY(g29,g29) = 5
    c: Angle(g-1,g1) = 1.13446
    c: DistanceY(g30,g4) = 5
    c: DistanceX(g7,g18) = 38
FEATURE [PartDesign::Hole] Hole  label="Side_CS_Hole"
  BaseFeature = -> Pad001
  CustomThreadClearance = 0
  Depth = 12
  DepthType = 0
  Diameter = 3.4
  DrillForDepth = false
  DrillPoint = 1
  DrillPointAngle = 118
  HoleCutCountersinkAngle = 90
  HoleCutCustomValues = false
  HoleCutDepth = 0
  HoleCutDiameter = 6.7
  HoleCutType = 7
  ModelThread = false
  Placement = pos=(0,0,0) rot=(0.57735,0.57735,0.57735;2.0944rad)
  Profile = -> Sketch040
  Refine = true
  Reversed = true
  Tapered = false
  TaperedAngle = 90
  ThreadClass = 0
  ThreadDepth = 12
  ThreadDepthType = 0
  ThreadDirection = 0
  ThreadFit = 0
  ThreadSize = 9
  ThreadType = 1
  Threaded = false
  UseCustomThreadClearance = false
  expr: Depth = Variables.Hole_Depth
FEATURE [Sketcher::SketchObject] Sketch041  label="Side_Threaded_Hole_Sketch"
  AttachmentOffset = pos=(0,0,-6) rot=(0,0,1;0rad)
  FullyConstrained = true
  MapMode = 5
  Placement = pos=(-6,1.3e-15,-1.3e-15) rot=(0.57735,0.57735,0.57735;2.0944rad)
  Support = -> [YZ_Plane002]
  expr: .AttachmentOffset.Base.z = -Variables.Panel_Thickness
  expr: Constraints[14] = Sketch014.Constraints[14]
  expr: Constraints[15] = Sketch014.Constraints[15]
  expr: Constraints[16] = Sketch014.Constraints[16]
  expr: Constraints[17] = Sketch014.Constraints[17]
  expr: Constraints[19] = Sketch014.Constraints[19]
  expr: Constraints[34] = Sketch014.Constraints[34]
  expr: Constraints[35] = Sketch014.Constraints[35]
  expr: Constraints[36] = Sketch014.Constraints[36]
  expr: Constraints[45] = Sketch014.Constraints[45]
  expr: Constraints[46] = Sketch014.Constraints[46]
  expr: Constraints[47] = Sketch014.Constraints[47]
  expr: Constraints[48] = Sketch014.Constraints[48]
  expr: Constraints[49] = Sketch014.Constraints[49]
  expr: Constraints[50] = Sketch014.Constraints[50]
  expr: Constraints[71] = Sketch014.Constraints[71]
  expr: Constraints[72] = Sketch014.Constraints[72]
  expr: Constraints[76] = Sketch014.Constraints[76]
  expr: Constraints[80] = Sketch014.Constraints[80]
  expr: Constraints[82] = Sketch014.Constraints[82]
  expr: Constraints[83] = Sketch014.Constraints[83]
  expr: Constraints[84] = Sketch014.Constraints[84]
  sketch-geometry (31):
    g0: LineSegment StartX=0 StartY=0 StartZ=0 EndX=0 EndY=9.93071 EndZ=0
    g1: LineSegment StartX=0 StartY=9.93071 StartZ=0 EndX=42 EndY=100 EndZ=0
    g2: LineSegment StartX=42 StartY=100 StartZ=0 EndX=72 EndY=100 EndZ=0
    g3: LineSegment StartX=72 StartY=100 StartZ=0 EndX=92.9838 EndY=55 EndZ=0
    g4: LineSegment StartX=92.9838 StartY=55 StartZ=0 EndX=168 EndY=55 EndZ=0
    g5: LineSegment StartX=168 StartY=55 StartZ=0 EndX=168 EndY=0 EndZ=0
    g6: LineSegment StartX=168 StartY=0 StartZ=0 EndX=0 EndY=0 EndZ=0
    g7: Circle CenterX=57 CenterY=85 CenterZ=0 NormalX=0 NormalY=0 NormalZ=1 AngleXU=0 Radius=3
    g8: LineSegment StartX=42 StartY=100 StartZ=0 EndX=57 EndY=85 EndZ=0
    g9: LineSegment StartX=57 StartY=85 StartZ=0 EndX=72 EndY=100 EndZ=0
    g10: LineSegment StartX=92.9838 StartY=55 StartZ=0 EndX=21.0162 EndY=55 EndZ=0
    g11: LineSegment StartX=21.0162 StartY=55 StartZ=0 EndX=57 EndY=85 EndZ=0
    g12: LineSegment StartX=57 StartY=85 StartZ=0 EndX=92.9838 EndY=55 EndZ=0
    g13: Circle CenterX=57 CenterY=65 CenterZ=0 NormalX=0 NormalY=0 NormalZ=1 AngleXU=0 Radius=1.5
    g14: LineSegment StartX=10 StartY=3 StartZ=0 EndX=59.3333 EndY=3 EndZ=0
    g15: LineSegment StartX=59.3333 StartY=3 StartZ=0 EndX=108.667 EndY=3 EndZ=0
    g16: LineSegment StartX=108.667 StartY=3 StartZ=0 EndX=158 EndY=3 EndZ=0
    g17: LineSegment StartX=165 StartY=45 StartZ=0 EndX=95 EndY=45 EndZ=0
    g18: Circle CenterX=95 CenterY=45 CenterZ=0 NormalX=0 NormalY=0 NormalZ=1 AngleXU=0 Radius=1.5
    g19: Circle CenterX=165 CenterY=45 CenterZ=0 NormalX=0 NormalY=0 NormalZ=1 AngleXU=0 Radius=1.5
    g20: Circle CenterX=10 CenterY=3 CenterZ=0 NormalX=0 NormalY=0 NormalZ=1 AngleXU=0 Radius=1.5
    g21: Circle CenterX=59.3333 CenterY=3 CenterZ=0 NormalX=0 NormalY=0 NormalZ=1 AngleXU=0 Radius=1.5
    g22: Circle CenterX=108.667 CenterY=3 CenterZ=0 NormalX=0 NormalY=0 NormalZ=1 AngleXU=0 Radius=1.5
    g23: Circle CenterX=158 CenterY=3 CenterZ=0 NormalX=0 NormalY=0 NormalZ=1 AngleXU=0 Radius=1.5
    g24: Circle CenterX=37.144 CenterY=42.2622 CenterZ=0 NormalX=0 NormalY=0 NormalZ=1 AngleXU=0 Radius=1.5
    g25: Circle CenterX=23.8547 CenterY=37.4253 CenterZ=0 NormalX=0 NormalY=0 NormalZ=1 AngleXU=0 Radius=1.5
    g26: LineSegment StartX=14.7916 StartY=41.6515 StartZ=0 EndX=23.8547 EndY=37.4253 EndZ=0
    g27: LineSegment StartX=23.8547 StartY=37.4253 StartZ=0 EndX=32.9178 EndY=33.1991 EndZ=0
    g28: LineSegment StartX=32.9178 StartY=33.1991 StartZ=0 EndX=37.144 EndY=42.2622 EndZ=0
    g29: LineSegment StartX=130 StartY=45 StartZ=0 EndX=130 EndY=50 EndZ=0
    g30: Circle CenterX=130 CenterY=50 CenterZ=0 NormalX=0 NormalY=0 NormalZ=1 AngleXU=0 Radius=2
  constraints (85):
    c: Coincident(g-1,g0)
    c: PointOnObject(g0,g-2)
    c: Coincident(g0,g1)
    c: Coincident(g1,g2)
    c: Horizontal(g2)
    c: Coincident(g2,g3)
    c: Coincident(g3,g4)
    c: Horizontal(g4)
    c: Coincident(g4,g5)
    c: PointOnObject(g5,g-1)
    c: Vertical(g5)
    c: Coincident(g5,g6)
    c: Coincident(g6,g0)
    c: DistanceY(g0,g0) = 9.93071
    c: DistanceY(g5,g5) = 55
    c: DistanceX(g6,g6) = 168
    c: DistanceX(g2,g2) = 30
    c: DistanceY(g0,g7) = 85
    c: DistanceX(g0,g7) = 57
    c: Diameter(g7) = 6
    c: Coincident(g1,g8)
    c: Coincident(g8,g7)
    c: Coincident(g8,g9)
    c: Coincident(g9,g2)
    c: Equal(g9,g8)
    c: Coincident(g10,g3)
    c: PointOnObject(g10,g1)
    c: Horizontal(g10)
    c: Coincident(g10,g11)
    c: Coincident(g11,g7)
    c: Coincident(g11,g12)
    c: Coincident(g12,g3)
    c: Equal(g12,g11)
    c: Vertical(g13,g7)
    c: Diameter(g13) = 3
    c: DistanceY(g13,g7) = 20
    c: DistanceY(g7,g1) = 15
    c: Horizontal(g14)
    c: Coincident(g14,g15)
    c: Horizontal(g15)
    c: Coincident(g15,g16)
    c: Horizontal(g16)
    c: Horizontal(g17)
    c: Equal(g14,g15)
    c: Equal(g15,g16)
    c: DistanceY(g0,g14) = 3
    c: DistanceX(g0,g14) = 10
    c: DistanceX(g16,g5) = 10
    c: DistanceX(g17,g5) = 3
    c: DistanceX(g17,g17) = 70
    c: DistanceY(g0,g17) = 45
    c: Coincident(g18,g17)
    c: Coincident(g19,g17)
    c: Equal(g19,g18)
    c: Equal(g18,g13)
    c: Coincident(g20,g14)
    c: Coincident(g21,g14)
    c: Coincident(g22,g15)
    c: Coincident(g23,g16)
    c: Equal(g23,g22)
    c: Equal(g22,g21)
    c: Equal(g21,g20)
    c: Equal(g20,g13)
    c: PointOnObject(g26,g1)
    c: Coincident(g26,g25)
    c: Coincident(g26,g27)
    c: Coincident(g27,g28)
    c: Coincident(g28,g24)
    c: Parallel(g26,g27)
    c: Perpendicular(g28,g27)
    c: Perpendicular(g1,g26)
    c: Distance(g26) = 10
    c: Distance(g27) = 10
    c: Equal(g27,g28)
    c: Equal(g25,g24)
    c: Equal(g24,g13)
    c: Distance(g0,g26) = 35
    c: Coincident(g30,g29)
    c: Vertical(g29)
    c: Symmetric(g18,g19,g29)
    c: Diameter(g30) = 4
    c: DistanceY(g29,g29) = 5
    c: Angle(g-1,g1) = 1.13446
    c: DistanceY(g30,g4) = 5
    c: DistanceX(g7,g18) = 38
FEATURE [Sketcher::SketchObject] Sketch042  label="Side_Pass_Hole_Sketch"
  AttachmentOffset = pos=(0,0,-6) rot=(0,0,1;0rad)
  FullyConstrained = true
  MapMode = 5
  Placement = pos=(-6,1.3e-15,-1.3e-15) rot=(0.57735,0.57735,0.57735;2.0944rad)
  Support = -> [YZ_Plane002]
  expr: .AttachmentOffset.Base.z = -Variables.Panel_Thickness
  expr: Constraints[14] = Sketch014.Constraints[14]
  expr: Constraints[15] = Sketch014.Constraints[15]
  expr: Constraints[16] = Sketch014.Constraints[16]
  expr: Constraints[17] = Sketch014.Constraints[17]
  expr: Constraints[19] = Sketch014.Constraints[19]
  expr: Constraints[34] = Sketch014.Constraints[34]
  expr: Constraints[35] = Sketch014.Constraints[35]
  expr: Constraints[36] = Sketch014.Constraints[36]
  expr: Constraints[45] = Sketch014.Constraints[45]
  expr: Constraints[46] = Sketch014.Constraints[46]
  expr: Constraints[47] = Sketch014.Constraints[47]
  expr: Constraints[48] = Sketch014.Constraints[48]
  expr: Constraints[49] = Sketch014.Constraints[49]
  expr: Constraints[50] = Sketch014.Constraints[50]
  expr: Constraints[71] = Sketch014.Constraints[71]
  expr: Constraints[72] = Sketch014.Constraints[72]
  expr: Constraints[76] = Sketch014.Constraints[76]
  expr: Constraints[80] = Sketch014.Constraints[80]
  expr: Constraints[82] = Sketch014.Constraints[82]
  expr: Constraints[83] = Sketch014.Constraints[83]
  expr: Constraints[84] = Sketch014.Constraints[84]
  sketch-geometry (31):
    g0: LineSegment StartX=0 StartY=0 StartZ=0 EndX=0 EndY=9.93071 EndZ=0
    g1: LineSegment StartX=0 StartY=9.93071 StartZ=0 EndX=42 EndY=100 EndZ=0
    g2: LineSegment StartX=42 StartY=100 StartZ=0 EndX=72 EndY=100 EndZ=0
    g3: LineSegment StartX=72 StartY=100 StartZ=0 EndX=92.9838 EndY=55 EndZ=0
    g4: LineSegment StartX=92.9838 StartY=55 StartZ=0 EndX=168 EndY=55 EndZ=0
    g5: LineSegment StartX=168 StartY=55 StartZ=0 EndX=168 EndY=0 EndZ=0
    g6: LineSegment StartX=168 StartY=0 StartZ=0 EndX=0 EndY=0 EndZ=0
    g7: Circle CenterX=57 CenterY=85 CenterZ=0 NormalX=0 NormalY=0 NormalZ=1 AngleXU=0 Radius=3
    g8: LineSegment StartX=42 StartY=100 StartZ=0 EndX=57 EndY=85 EndZ=0
    g9: LineSegment StartX=57 StartY=85 StartZ=0 EndX=72 EndY=100 EndZ=0
    g10: LineSegment StartX=92.9838 StartY=55 StartZ=0 EndX=21.0162 EndY=55 EndZ=0
    g11: LineSegment StartX=21.0162 StartY=55 StartZ=0 EndX=57 EndY=85 EndZ=0
    g12: LineSegment StartX=57 StartY=85 StartZ=0 EndX=92.9838 EndY=55 EndZ=0
    g13: Circle CenterX=57 CenterY=65 CenterZ=0 NormalX=0 NormalY=0 NormalZ=1 AngleXU=0 Radius=1.5
    g14: LineSegment StartX=10 StartY=3 StartZ=0 EndX=59.3333 EndY=3 EndZ=0
    g15: LineSegment StartX=59.3333 StartY=3 StartZ=0 EndX=108.667 EndY=3 EndZ=0
    g16: LineSegment StartX=108.667 StartY=3 StartZ=0 EndX=158 EndY=3 EndZ=0
    g17: LineSegment StartX=165 StartY=45 StartZ=0 EndX=95 EndY=45 EndZ=0
    g18: Circle CenterX=95 CenterY=45 CenterZ=0 NormalX=0 NormalY=0 NormalZ=1 AngleXU=0 Radius=1.5
    g19: Circle CenterX=165 CenterY=45 CenterZ=0 NormalX=0 NormalY=0 NormalZ=1 AngleXU=0 Radius=1.5
    g20: Circle CenterX=10 CenterY=3 CenterZ=0 NormalX=0 NormalY=0 NormalZ=1 AngleXU=0 Radius=1.5
    g21: Circle CenterX=59.3333 CenterY=3 CenterZ=0 NormalX=0 NormalY=0 NormalZ=1 AngleXU=0 Radius=1.5
    g22: Circle CenterX=108.667 CenterY=3 CenterZ=0 NormalX=0 NormalY=0 NormalZ=1 AngleXU=0 Radius=1.5
    g23: Circle CenterX=158 CenterY=3 CenterZ=0 NormalX=0 NormalY=0 NormalZ=1 AngleXU=0 Radius=1.5
    g24: Circle CenterX=37.144 CenterY=42.2622 CenterZ=0 NormalX=0 NormalY=0 NormalZ=1 AngleXU=0 Radius=1.5
    g25: Circle CenterX=23.8547 CenterY=37.4253 CenterZ=0 NormalX=0 NormalY=0 NormalZ=1 AngleXU=0 Radius=1.5
    g26: LineSegment StartX=14.7916 StartY=41.6515 StartZ=0 EndX=23.8547 EndY=37.4253 EndZ=0
    g27: LineSegment StartX=23.8547 StartY=37.4253 StartZ=0 EndX=32.9178 EndY=33.1991 EndZ=0
    g28: LineSegment StartX=32.9178 StartY=33.1991 StartZ=0 EndX=37.144 EndY=42.2622 EndZ=0
    g29: LineSegment StartX=130 StartY=45 StartZ=0 EndX=130 EndY=50 EndZ=0
    g30: Circle CenterX=130 CenterY=50 CenterZ=0 NormalX=0 NormalY=0 NormalZ=1 AngleXU=0 Radius=2
  constraints (85):
    c: Coincident(g-1,g0)
    c: PointOnObject(g0,g-2)
    c: Coincident(g0,g1)
    c: Coincident(g1,g2)
    c: Horizontal(g2)
    c: Coincident(g2,g3)
    c: Coincident(g3,g4)
    c: Horizontal(g4)
    c: Coincident(g4,g5)
    c: PointOnObject(g5,g-1)
    c: Vertical(g5)
    c: Coincident(g5,g6)
    c: Coincident(g6,g0)
    c: DistanceY(g0,g0) = 9.93071
    c: DistanceY(g5,g5) = 55
    c: DistanceX(g6,g6) = 168
    c: DistanceX(g2,g2) = 30
    c: DistanceY(g0,g7) = 85
    c: DistanceX(g0,g7) = 57
    c: Diameter(g7) = 6
    c: Coincident(g1,g8)
    c: Coincident(g8,g7)
    c: Coincident(g8,g9)
    c: Coincident(g9,g2)
    c: Equal(g9,g8)
    c: Coincident(g10,g3)
    c: PointOnObject(g10,g1)
    c: Horizontal(g10)
    c: Coincident(g10,g11)
    c: Coincident(g11,g7)
    c: Coincident(g11,g12)
    c: Coincident(g12,g3)
    c: Equal(g12,g11)
    c: Vertical(g13,g7)
    c: Diameter(g13) = 3
    c: DistanceY(g13,g7) = 20
    c: DistanceY(g7,g1) = 15
    c: Horizontal(g14)
    c: Coincident(g14,g15)
    c: Horizontal(g15)
    c: Coincident(g15,g16)
    c: Horizontal(g16)
    c: Horizontal(g17)
    c: Equal(g14,g15)
    c: Equal(g15,g16)
    c: DistanceY(g0,g14) = 3
    c: DistanceX(g0,g14) = 10
    c: DistanceX(g16,g5) = 10
    c: DistanceX(g17,g5) = 3
    c: DistanceX(g17,g17) = 70
    c: DistanceY(g0,g17) = 45
    c: Coincident(g18,g17)
    c: Coincident(g19,g17)
    c: Equal(g19,g18)
    c: Equal(g18,g13)
    c: Coincident(g20,g14)
    c: Coincident(g21,g14)
    c: Coincident(g22,g15)
    c: Coincident(g23,g16)
    c: Equal(g23,g22)
    c: Equal(g22,g21)
    c: Equal(g21,g20)
    c: Equal(g20,g13)
    c: PointOnObject(g26,g1)
    c: Coincident(g26,g25)
    c: Coincident(g26,g27)
    c: Coincident(g27,g28)
    c: Coincident(g28,g24)
    c: Parallel(g26,g27)
    c: Perpendicular(g28,g27)
    c: Perpendicular(g1,g26)
    c: Distance(g26) = 10
    c: Distance(g27) = 10
    c: Equal(g27,g28)
    c: Equal(g25,g24)
    c: Equal(g24,g13)
    c: Distance(g0,g26) = 35
    c: Coincident(g30,g29)
    c: Vertical(g29)
    c: Symmetric(g18,g19,g29)
    c: Diameter(g30) = 4
    c: DistanceY(g29,g29) = 5
    c: Angle(g-1,g1) = 1.13446
    c: DistanceY(g30,g4) = 5
    c: DistanceX(g7,g18) = 38
FEATURE [PartDesign::Hole] Hole014  label="Side_Threaded_Hole"
  BaseFeature = -> Hole
  CustomThreadClearance = 0
  Depth = 12
  DepthType = 0
  Diameter = 2.5
  DrillForDepth = false
  DrillPoint = 1
  DrillPointAngle = 118
  HoleCutCountersinkAngle = 90
  HoleCutCustomValues = false
  HoleCutDepth = 0
  HoleCutDiameter = 6.1
  HoleCutType = 0
  ModelThread = false
  Placement = pos=(0,0,0) rot=(0.57735,0.57735,0.57735;2.0944rad)
  Profile = -> Sketch041
  Refine = true
  Reversed = true
  Tapered = false
  TaperedAngle = 90
  ThreadClass = 0
  ThreadDepth = 12
  ThreadDepthType = 0
  ThreadDirection = 0
  ThreadFit = 0
  ThreadSize = 9
  ThreadType = 1
  Threaded = true
  UseCustomThreadClearance = false
  expr: Depth = Variables.Hole_Depth
FEATURE [PartDesign::Hole] Hole015  label="Side_Pass_Hole"
  BaseFeature = -> Hole014
  CustomThreadClearance = 0
  Depth = 12
  DepthType = 0
  Diameter = 3.4
  DrillForDepth = false
  DrillPoint = 1
  DrillPointAngle = 118
  HoleCutCountersinkAngle = 90
  HoleCutCustomValues = false
  HoleCutDepth = 0
  HoleCutDiameter = 6.1
  HoleCutType = 0
  ModelThread = false
  Placement = pos=(0,0,0) rot=(0.57735,0.57735,0.57735;2.0944rad)
  Profile = -> Sketch042
  Refine = true
  Reversed = true
  Tapered = false
  TaperedAngle = 90
  ThreadClass = 0
  ThreadDepth = 12
  ThreadDepthType = 0
  ThreadDirection = 0
  ThreadFit = 0
  ThreadSize = 9
  ThreadType = 1
  Threaded = false
  UseCustomThreadClearance = false
  expr: Depth = Variables.Hole_Depth
FEATURE [PartDesign::Fillet] Fillet  label="Solderwire_Hole_Fillet"
  Base = -> Hole015 [Face17]
  BaseFeature = -> Hole015
  Placement = pos=(0,0,0) rot=(0.57735,0.57735,0.57735;2.0944rad)
  Radius = 2
  Refine = true
  SupportTransform = false
  UseAllEdges = false
  expr: Radius = Variables.Panel_Thickness / 2 - 1
FEATURE [PartDesign::Fillet] Fillet005  label="Side_Edge_Fillet"
  Base = -> Fillet [Edge22,Edge34,Edge40,Edge42,Edge39]
  BaseFeature = -> Fillet
  Placement = pos=(0,0,0) rot=(0.57735,0.57735,0.57735;2.0944rad)
  Radius = 6
  Refine = true
  SupportTransform = false
  UseAllEdges = false
FEATURE [PartDesign::Body] Side  label="Side_Panel"
  Group = -> [LCS_0001,Sketch015,Pad001,Sketch040,Hole,Sketch041,Sketch042,Hole014,Hole015,Fillet,Fillet005]
  Origin = -> Origin002
  Tip = -> Fillet005
FEATURE [App::DocumentObjectGroup] Bodies
  Group = -> [Base,Side,Rear,Handle,Handle001]
FEATURE [Sketcher::SketchObject] Master_Side_Screw_Sketch
  AttachmentOffset = pos=(0,0,-6) rot=(0,0,1;0rad)
  ExternalGeometry = -> [Sketch014]
  FullyConstrained = true
  MapMode = 5
  Placement = pos=(-6,1.3e-15,-1.3e-15) rot=(0.57735,0.57735,0.57735;2.0944rad)
  Support = -> [YZ_Plane]
  expr: .AttachmentOffset.Base.z = -Variables.Panel_Thickness
  sketch-geometry (9):
    g0: Circle CenterX=57 CenterY=65 CenterZ=0 NormalX=0 NormalY=0 NormalZ=1 AngleXU=0 Radius=1.5
    g1: Circle CenterX=23.8547 CenterY=37.4253 CenterZ=0 NormalX=0 NormalY=0 NormalZ=1 AngleXU=0 Radius=1.5
    g2: Circle CenterX=37.144 CenterY=42.2622 CenterZ=0 NormalX=0 NormalY=0 NormalZ=1 AngleXU=0 Radius=1.5
    g3: Circle CenterX=95 CenterY=45 CenterZ=0 NormalX=0 NormalY=0 NormalZ=1 AngleXU=0 Radius=1.5
    g4: Circle CenterX=165 CenterY=45 CenterZ=0 NormalX=0 NormalY=0 NormalZ=1 AngleXU=0 Radius=1.5
    g5: Circle CenterX=158 CenterY=3 CenterZ=0 NormalX=0 NormalY=0 NormalZ=1 AngleXU=0 Radius=1.5
    g6: Circle CenterX=108.667 CenterY=3 CenterZ=0 NormalX=0 NormalY=0 NormalZ=1 AngleXU=0 Radius=1.5
    g7: Circle CenterX=59.3333 CenterY=3 CenterZ=0 NormalX=0 NormalY=0 NormalZ=1 AngleXU=0 Radius=1.5
    g8: Circle CenterX=10 CenterY=3 CenterZ=0 NormalX=0 NormalY=0 NormalZ=1 AngleXU=0 Radius=1.5
  constraints (18):
    c: Coincident(g0,g-11)
    c: Coincident(g1,g-9)
    c: Coincident(g2,g-10)
    c: Coincident(g3,g-8)
    c: Coincident(g4,g-7)
    c: Coincident(g5,g-6)
    c: Coincident(g6,g-5)
    c: Coincident(g7,g-4)
    c: Coincident(g8,g-3)
    c: Equal(g0,g1)
    c: Equal(g1,g2)
    c: Equal(g2,g3)
    c: Equal(g3,g4)
    c: Equal(g4,g5)
    c: Equal(g5,g6)
    c: Equal(g6,g7)
    c: Equal(g7,g8)
    c: Equal(g-11,g0)
FEATURE [Sketcher::SketchObject] Master_Top_Screw_Sketch
  FullyConstrained = true
  MapMode = 5
  Support = -> [XY_Plane]
  expr: Constraints[18] = Master_Top_Sketch.Constraints[18]
  expr: Constraints[19] = Master_Top_Sketch.Constraints[19]
  expr: Constraints[22] = Master_Top_Sketch.Constraints[22]
  expr: Constraints[23] = Master_Top_Sketch.Constraints[23]
  expr: Constraints[25] = Master_Top_Sketch.Constraints[25]
  expr: Constraints[41] = Master_Top_Sketch.Constraints[41]
  expr: Constraints[42] = Master_Top_Sketch.Constraints[42]
  expr: Constraints[43] = Master_Top_Sketch.Constraints[43]
  expr: Constraints[44] = Master_Top_Sketch.Constraints[44]
  expr: Constraints[51] = Master_Top_Sketch.Constraints[51]
  expr: Constraints[52] = Master_Top_Sketch.Constraints[52]
  expr: Constraints[54] = Master_Top_Sketch.Constraints[54]
  expr: Constraints[58] = Master_Top_Sketch.Constraints[58]
  sketch-geometry (23):
    g0: LineSegment StartX=0 StartY=168 StartZ=0 EndX=0 EndY=0 EndZ=0
    g1: LineSegment StartX=70 StartY=168 StartZ=0 EndX=0 EndY=168 EndZ=0
    g2: LineSegment StartX=90 StartY=20 StartZ=0 EndX=90 EndY=148 EndZ=0
    g3: LineSegment StartX=0 StartY=0 StartZ=0 EndX=70 EndY=0 EndZ=0
    g4: LineSegment StartX=70 StartY=168 StartZ=0 EndX=90 EndY=148 EndZ=0
    g5: LineSegment StartX=70 StartY=0 StartZ=0 EndX=90 EndY=20 EndZ=0
    g6: LineSegment StartX=90 StartY=20 StartZ=0 EndX=90 EndY=0 EndZ=0
    g7: LineSegment StartX=70 StartY=0 StartZ=0 EndX=90 EndY=0 EndZ=0
    g8: Circle CenterX=85 CenterY=131.5 CenterZ=0 NormalX=0 NormalY=0 NormalZ=1 AngleXU=0 Radius=1.5
    g9: Circle CenterX=85 CenterY=36.5 CenterZ=0 NormalX=0 NormalY=0 NormalZ=1 AngleXU=0 Radius=1.5
    g10: LineSegment StartX=38 StartY=35 StartZ=0 EndX=38 EndY=0 EndZ=0
    g11: Circle CenterX=18 CenterY=165 CenterZ=0 NormalX=0 NormalY=0 NormalZ=1 AngleXU=0 Radius=1.5
    g12: Circle CenterX=48 CenterY=165 CenterZ=0 NormalX=0 NormalY=0 NormalZ=1 AngleXU=0 Radius=1.5
    g13: Circle CenterX=18 CenterY=95 CenterZ=0 NormalX=0 NormalY=0 NormalZ=1 AngleXU=0 Radius=1.5
    g14: Circle CenterX=48 CenterY=95 CenterZ=0 NormalX=0 NormalY=0 NormalZ=1 AngleXU=0 Radius=1.5
    g15: LineSegment StartX=18 StartY=95 StartZ=0 EndX=48 EndY=95 EndZ=0
    g16: LineSegment StartX=48 StartY=95 StartZ=0 EndX=48 EndY=165 EndZ=0
    g17: LineSegment StartX=48 StartY=165 StartZ=0 EndX=18 EndY=165 EndZ=0
    g18: LineSegment StartX=18 StartY=165 StartZ=0 EndX=18 EndY=95 EndZ=0
    g19: LineSegment StartX=85 StartY=36.5 StartZ=0 EndX=85 EndY=131.5 EndZ=0
    g20: LineSegment StartX=85 StartY=84 StartZ=0 EndX=0 EndY=84 EndZ=0
    g21: Circle CenterX=23 CenterY=35 CenterZ=0 NormalX=0 NormalY=0 NormalZ=1 AngleXU=0 Radius=1.5
    g22: Circle CenterX=53 CenterY=35 CenterZ=0 NormalX=0 NormalY=0 NormalZ=1 AngleXU=0 Radius=1.5
  constraints (61):
    c: Coincident(g1,g0)
    c: Coincident(g0,g3)
    c: Coincident(g3,g-1)
    c: Horizontal(g1)
    c: Vertical(g2)
    c: Horizontal(g3)
    c: Coincident(g5,g3)
    c: Vertical(g3,g1)
    c: Coincident(g1,g4)
    c: Coincident(g2,g4)
    c: Coincident(g2,g5)
    c: Equal(g5,g4)
    c: Coincident(g6,g2)
    c: PointOnObject(g6,g-1)
    c: Coincident(g7,g3)
    c: Coincident(g7,g6)
    c: Vertical(g6)
    c: Equal(g7,g6)
    c: DistanceX(g7,g7) = 20
    c: DistanceX(g0,g6) = 90
    c: Vertical(g9,g8)
    c: Vertical(g10)
    c: DistanceY(g10,g10) = 35
    c: DistanceY(g9,g8) = 95
    c: Equal(g9,g8)
    c: DistanceX(g9,g2) = 5
    c: Coincident(g15,g16)
    c: Coincident(g16,g17)
    c: Coincident(g17,g18)
    c: Coincident(g18,g15)
    c: Horizontal(g15)
    c: Horizontal(g17)
    c: Vertical(g16)
    c: Vertical(g18)
    c: Coincident(g15,g13)
    c: Coincident(g16,g12)
    c: Coincident(g14,g15)
    c: Coincident(g11,g17)
    c: Equal(g11,g12)
    c: Equal(g12,g14)
    c: Equal(g14,g13)
    c: Diameter(g11) = 3
    c: DistanceY(g11,g0) = 3
    c: DistanceX(g0,g11) = 18
    c: DistanceX(g17,g17) = 30
    c: Equal(g8,g11)
    c: Coincident(g19,g9)
    c: Coincident(g19,g8)
    c: Horizontal(g20)
    c: Symmetric(g9,g8,g20)
    c: Symmetric(g0,g0,g20)
    c: DistanceY(g0,g0) = 168
    c: DistanceY(g18,g18) = 70
    c: PointOnObject(g0,g-2)
    c: DistanceX(g0,g10) = 38
    c: PointOnObject(g10,g3)
    c: Horizontal(g21,g22)
    c: Symmetric(g21,g22,g10)
    c: DistanceX(g21,g22) = 30
    c: Equal(g22,g21)
    c: Equal(g21,g11)
FEATURE [PartDesign::CoordinateSystem] LCS_Assembly_Handle
  AttacherType = Attacher::AttachEngine3D
  AttachmentOffset = pos=(-3,0,0) rot=(0,0,1;0rad)
  Placement = pos=(38,95,115) rot=(0,0,1;0rad)
  Support = -> [Origin]
  expr: .AttachmentOffset.Base.x = -Variables.Panel_Thickness / 2
  expr: .Placement.Base.x = Variables.Centerline_Offset
  expr: .Placement.Base.y = -Variables.Mid_Panel_Offset - Variables.Panel_Thickness / 2
  expr: .Placement.Base.z = Variables.Handle_Screw_Height + 5
FEATURE [PartDesign::CoordinateSystem] LCS_Tool_Holder_Adapter  label="LCS_Assembly_Tool_Holder_Adapter"
  AttacherType = Attacher::AttachEngine3D
  MapMode = 11
  Placement = pos=(-6.2e-15,57,85) rot=(0.707107,0,0.707107;3.14159rad)
  Support = -> [Sketch014]
FEATURE [PartDesign::CoordinateSystem] LCS_Tool_Holder_Washer  label="LCS_Assembly_Tool_Holder_Washer"
  AttacherType = Attacher::AttachEngine3D
  AttachmentOffset = pos=(0,0,-6) rot=(0,0,1;0rad)
  MapMode = 11
  Placement = pos=(-6,57,85) rot=(0.707107,0,0.707107;3.14159rad)
  Support = -> [Sketch014]
  expr: .AttachmentOffset.Base.z = -Variables.Panel_Thickness
FEATURE [PartDesign::CoordinateSystem] LCS_Spool_Screw  label="LCS_Assembly_Spool_Screw_Knob"
  AttacherType = Attacher::AttachEngine3D
  AttachmentOffset = pos=(0,0,-70) rot=(0,0,1;0rad)
  MapMode = 11
  Placement = pos=(38,168,40) rot=(0.57735,-0.57735,0.57735;2.0944rad)
  Support = -> [Sketch037]
  expr: .AttachmentOffset.Base.z = -Variables.Length - Variables.Mid_Panel_Offset
FEATURE [PartDesign::CoordinateSystem] LCS_Assembly_Rear_Connector
  AttacherType = Attacher::AttachEngine3D
  AttachmentOffset = pos=(0,0,-70) rot=(0,0,1;0rad)
  MapMode = 11
  Placement = pos=(7,168,13) rot=(0.57735,-0.57735,0.57735;2.0944rad)
  Support = -> [Sketch037]
  expr: .AttachmentOffset.Base.z = -Variables.Length - Variables.Mid_Panel_Offset
FEATURE [PartDesign::CoordinateSystem] LCS_Assembly_Tip_Cleaner
  AttacherType = Attacher::AttachEngine3D
  AttachmentOffset = pos=(0,0,6) rot=(0,0,1;0rad)
  MapMode = 11
  Placement = pos=(23,35,6) rot=(0,0,1;1.5708rad)
  Support = -> [Master_Top_Sketch]
  expr: .AttachmentOffset.Base.z = Variables.Panel_Thickness
FEATURE [PartDesign::CoordinateSystem] LCS_Assembly_Tip_Magazine
  AttacherType = Attacher::AttachEngine3D
  AttachmentOffset = pos=(0,0,6) rot=(0,0,1;0rad)
  MapMode = 11
  Placement = pos=(85,36.5,6) rot=(0,0,1;1.5708rad)
  Support = -> [Master_Top_Sketch]
  expr: .AttachmentOffset.Base.z = Variables.Panel_Thickness
FEATURE [PartDesign::CoordinateSystem] LCS_Assembly_Spool
  AttacherType = Attacher::AttachEngine3D
  AttachmentOffset = pos=(0,0,-63.5) rot=(0,0,1;0rad)
  MapMode = 11
  Placement = pos=(38,161.5,40) rot=(0.57735,-0.57735,0.57735;2.0944rad)
  Support = -> [Sketch037]
  expr: .AttachmentOffset.Base.z = -Variables.Length - Variables.Mid_Panel_Offset + Variables.Panel_Thickness + 0.5
FEATURE [PartDesign::CoordinateSystem] LCS_Assembly_Tip_Remover
  AttacherType = Attacher::AttachEngine3D
  AttachmentOffset = pos=(0,0,-6) rot=(0,0,1;1.13446rad)
  MapMode = 11
  Placement = pos=(-6,37.144,42.2622) rot=(0.644711,-0.410726,0.644711;3.92103rad)
  Support = -> [Sketch014]
  expr: .AttachmentOffset.Base.z = -Variables.Panel_Thickness
  expr: .AttachmentOffset.Rotation.Yaw = Variables.Front_Edge_Angle
FEATURE [App::Link] Tip_Cleaner
  AssemblyType = Part::Link
  AttachedBy = #LCS_Tip_Cleaner_Hole_1
  AttachedTo = Parent Assembly#LCS_Assembly_Tip_Cleaner
  AttachmentOffset = pos=(0,0,0) rot=(1,0,0;3.14159rad)
  LinkPlacement = pos=(38,-7.1e-15,6) rot=(0,0,1;0rad)
  LinkedObject = -> <external Parts/Tip Cleaner.FCStd>#Body
  Placement = pos=(38,-7.1e-15,6) rot=(0,0,1;0rad)
  SolverId = Asm4EE
  expr: Placement = LCS_Assembly_Tip_Cleaner.Placement * AttachmentOffset * Tip_Cleaner#LCS_Tip_Cleaner_Hole_1.Placement ^ -1
FEATURE [App::Link] Tip_Remover_Bracket
  AssemblyType = Part::Link
  AttachedBy = #Hole1001
  AttachedTo = Parent Assembly#LCS_Assembly_Tip_Remover
  AttachmentOffset = pos=(0,0,0) rot=(0,0,-1;1.5708rad)
  LinkPlacement = pos=(-6,12.6785,37.1199) rot=(1,0,0;5.84685rad)
  LinkedObject = -> <external Parts/Tip Remover Bracket.FCStd>#Body
  Placement = pos=(-6,12.6785,37.1199) rot=(1,0,0;5.84685rad)
  SolverId = Asm4EE
  expr: Placement = LCS_Assembly_Tip_Remover.Placement * AttachmentOffset * Tip_Remover_Bracket#Hole1001.Placement ^ -1
FEATURE [App::Link] Tool_Holder_Washer
  AssemblyType = Part::Link
  AttachedBy = #Center
  AttachedTo = Parent Assembly#LCS_Tool_Holder_Washer
  AttachmentOffset = pos=(0,0,0) rot=(1,0,0;3.14159rad)
  LinkPlacement = pos=(-6,57,85) rot=(0,0,1;4.71239rad)
  LinkedObject = -> <external Parts/Tool Holder Washer.FCStd>#Body
  Placement = pos=(-6,57,85) rot=(0,0,1;4.71239rad)
  SolverId = Asm4EE
  expr: Placement = LCS_Tool_Holder_Washer.Placement * AttachmentOffset * Tool_Holder_Washer#Center.Placement ^ -1
FEATURE [App::Link] Tool_Holder_Screw
  AssemblyType = Part::Link
  AttachedBy = #LCS_1
  AttachedTo = Tool_Holder_Washer#Center2
  AttachmentOffset = pos=(0,0,0) rot=(1,0,0;3.14159rad)
  LinkPlacement = pos=(-10,57,85) rot=(-1,0,0;1.5708rad)
  LinkedObject = -> <external Parts/Tool Holder Screw.FCStd>#Body
  Placement = pos=(-10,57,85) rot=(-1,0,0;1.5708rad)
  SolverId = Asm4EE
  expr: Placement = Tool_Holder_Washer.Placement * Tool_Holder_Washer#Center2.Placement * AttachmentOffset * Tool_Holder_Screw#LCS_1.Placement ^ -1
FEATURE [App::Link] Tool_Holder_Adapter
  AssemblyType = Part::Link
  AttachedBy = #Mounting_face_main_hole
  AttachedTo = Parent Assembly#LCS_Tool_Holder_Adapter
  AttachmentOffset = pos=(0,0,0) rot=(0.57735,0.57735,0.57735;2.0944rad)
  LinkPlacement = pos=(10,57,85) rot=(0,0,1;4.71239rad)
  LinkedObject = -> <external Parts/Tool Holder Adapter.FCStd>#Body
  Placement = pos=(10,57,85) rot=(0,0,1;4.71239rad)
  SolverId = Asm4EE
  expr: Placement = LCS_Tool_Holder_Adapter.Placement * AttachmentOffset * Tool_Holder_Adapter#Mounting_face_main_hole.Placement ^ -1
FEATURE [App::Link] Tool_Holder
  AssemblyType = Part::Link
  AttachedBy = #LCS_1
  AttachedTo = Tool_Holder_Adapter#Holder
  AttachmentOffset = pos=(0,0,0) rot=(0,-1,0;0.349066rad)
  LinkPlacement = pos=(38,23.1711,97.3127) rot=(1,0,0;5.93412rad)
  LinkedObject = -> <external Parts/Tool Holder.FCStd>#Body
  Placement = pos=(38,23.1711,97.3127) rot=(1,0,0;5.93412rad)
  SolverId = Asm4EE
  expr: .AttachmentOffset.Rotation.Angle = Variables.Tool_Angle
  expr: Placement = Tool_Holder_Adapter.Placement * Tool_Holder_Adapter#Holder.Placement * AttachmentOffset * Tool_Holder#LCS_1.Placement ^ -1
FEATURE [App::Link] Tip_Magazine
  AssemblyType = Part::Link
  AttachedBy = #Hole1
  AttachedTo = Parent Assembly#LCS_Assembly_Tip_Magazine
  AttachmentOffset = pos=(0,0,0) rot=(0,0,-1;1.5708rad)
  LinkPlacement = pos=(85,46.5,6) rot=(0,0,1;0rad)
  LinkedObject = -> <external Parts/Tip Magazine.FCStd>#Body009
  Placement = pos=(85,46.5,6) rot=(0,0,1;0rad)
  SolverId = Asm4EE
  expr: Placement = LCS_Assembly_Tip_Magazine.Placement * AttachmentOffset * Tip_Magazine#Hole1.Placement ^ -1
FEATURE [App::Link] Spool_Dummy
  AssemblyType = Part::Link
  AttachedBy = #LCS_1
  AttachedTo = Parent Assembly#LCS_Assembly_Spool
  AttachmentOffset = pos=(0,0,0) rot=(1,0,0;3.14159rad)
  LinkPlacement = pos=(38,130,40) rot=(0.57735,0.57735,-0.57735;4.18879rad)
  LinkedObject = -> <external Parts/Spool Dummy.FCStd>#Body
  Placement = pos=(38,130,40) rot=(0.57735,0.57735,-0.57735;4.18879rad)
  SolverId = Asm4EE
  expr: Placement = LCS_Assembly_Spool.Placement * AttachmentOffset * Spool_Dummy#LCS_1.Placement ^ -1
FEATURE [App::Link] Spool_Screw_Knob  label="Spool_Knob"
  AssemblyType = Part::Link
  AttachedBy = #LCS_1
  AttachedTo = Parent Assembly#LCS_Spool_Screw
  LinkPlacement = pos=(38,168,40) rot=(1,0,0;3.14159rad)
  LinkedObject = -> <external Parts/Spool Knob.FCStd>#Body
  Placement = pos=(38,168,40) rot=(1,0,0;3.14159rad)
  SolverId = Asm4EE
  expr: Placement = LCS_Spool_Screw.Placement * AttachmentOffset * Spool_Knob#LCS_1.Placement ^ -1
FEATURE [App::Link] Connector_Minijack
  AssemblyType = Part::Link
  AttachedBy = #LCS_1
  AttachedTo = Parent Assembly#LCS_Assembly_Rear_Connector
  AttachmentOffset = pos=(0,0,4) rot=(1,0,0;3.14159rad)
  LinkPlacement = pos=(7,166,13) rot=(-0.57735,0.57735,0.57735;4.18879rad)
  LinkedObject = -> <external Parts/Connector Minijack MJ-064H.FCStd>#Body
  Placement = pos=(7,166,13) rot=(-0.57735,0.57735,0.57735;4.18879rad)
  SolverId = Asm4EE
  expr: Placement = LCS_Assembly_Rear_Connector.Placement * AttachmentOffset * Connector_Minijack_MJ_064H#LCS_1.Placement ^ -1
FEATURE [App::Link] Tip_Dummy_Remover
  AssemblyType = Part::Link
  AttachedBy = #Remover
  AttachedTo = Tip_Remover_Bracket#LCS_Tip_Remover_Bracket_Tip_Attachment
  LinkPlacement = pos=(-14,-48.3494,76.6115) rot=(-0.644711,-0.410726,0.644711;2.36216rad)
  LinkedObject = -> <external Parts/Tip Dummy.FCStd>#Body
  Placement = pos=(-14,-48.3494,76.6115) rot=(-0.644711,-0.410726,0.644711;2.36216rad)
  SolverId = Asm4EE
  expr: Placement = Tip_Remover_Bracket.Placement * Tip_Remover_Bracket#LCS_Tip_Remover_Bracket_Tip_Attachment.Placement * AttachmentOffset * Tip_Dummy#Remover.Placement ^ -1
FEATURE [App::LinkElement] Tip_Dummy_Magazine_i0
  LinkedObject = -> <external Parts/Tip Dummy.FCStd>#Body
  _LinkOwner = 2662
FEATURE [App::LinkElement] Tip_Dummy_Magazine_i1
  LinkPlacement = pos=(0,0,15) rot=(0,0,1;0rad)
  LinkedObject = -> <external Parts/Tip Dummy.FCStd>#Body
  Placement = pos=(0,0,15) rot=(0,0,1;0rad)
  _LinkOwner = 2662
FEATURE [App::LinkElement] Tip_Dummy_Magazine_i2
  LinkPlacement = pos=(0,0,30) rot=(0,0,1;0rad)
  LinkedObject = -> <external Parts/Tip Dummy.FCStd>#Body
  Placement = pos=(0,0,30) rot=(0,0,1;0rad)
  _LinkOwner = 2662
FEATURE [App::LinkElement] Tip_Dummy_Magazine_i3
  LinkPlacement = pos=(0,0,45) rot=(0,0,1;0rad)
  LinkedObject = -> <external Parts/Tip Dummy.FCStd>#Body
  Placement = pos=(0,0,45) rot=(0,0,1;0rad)
  _LinkOwner = 2662
FEATURE [App::LinkElement] Tip_Dummy_Magazine_i4
  LinkPlacement = pos=(0,0,60) rot=(0,0,1;0rad)
  LinkedObject = -> <external Parts/Tip Dummy.FCStd>#Body
  Placement = pos=(0,0,60) rot=(0,0,1;0rad)
  _LinkOwner = 2662
FEATURE [App::LinkElement] Tip_Dummy_Magazine_i5
  LinkPlacement = pos=(0,0,75) rot=(0,0,1;0rad)
  LinkedObject = -> <external Parts/Tip Dummy.FCStd>#Body
  Placement = pos=(0,0,75) rot=(0,0,1;0rad)
  _LinkOwner = 2662
FEATURE [App::Link] Tip_Dummy_Magazine
  AssemblyType = Part::Link
  AttachedBy = #Tip_base
  AttachedTo = Tip_Magazine#Holder_pos_1
  AttachmentOffset = pos=(0,0,0) rot=(1,0,0;3.14159rad)
  ElementCount = 6
  ElementList = -> [Tip_Dummy_Magazine_i0,Tip_Dummy_Magazine_i1,Tip_Dummy_Magazine_i2,Tip_Dummy_Magazine_i3,Tip_Dummy_Magazine_i4,Tip_Dummy_Magazine_i5]
  LinkPlacement = pos=(85,46.5,6) rot=(-0.57735,-0.57735,-0.57735;2.0944rad)
  LinkedObject = -> <external Parts/Tip Dummy.FCStd>#Body
  Placement = pos=(85,46.5,6) rot=(-0.57735,-0.57735,-0.57735;2.0944rad)
  SolverId = Asm4EE
  expr: Placement = Tip_Magazine.Placement * Tip_Magazine#Holder_pos_1.Placement * AttachmentOffset * Tip_Dummy#Tip_base.Placement ^ -1
FEATURE [App::DocumentObjectGroup] Dummy_Parts  label="Dummy_Models"
  Group = -> [Spool_Dummy,Tip_Dummy_Remover,Tip_Dummy_Magazine]
FEATURE [Part::FeaturePython] Screw  label="M3x16-Screw"  # Fasteners workbench fastener (typed FeaturePython)
  AssemblyType = Part::Link
  AttachedBy = Origin
  AttachedTo = Parent Assembly#HoleAxis_1
  AttachmentOffset = pos=(0,0,0) rot=(1,0,0;3.14159rad)
  Placement = pos=(48,165,0) rot=(1,0,0;3.14159rad)
  SolverId = Asm4EE
  diameter = 3
  invert = true
  length = 3
  lengthCustom = 16
  matchOuter = true
  offset = 0
  thread = false
  type = 18
  expr: Placement = HoleAxis_1.Placement * AttachmentOffset
FEATURE [Part::FeaturePython] Screw013  label="M3x8-Screw"  # Fasteners workbench fastener (typed FeaturePython)
  AssemblyType = Part::Link
  AttachedBy = Origin
  AttachedTo = Tip_Remover_Bracket#LCS_Tip_Remover_Bracket_Hole_2_Outside
  Placement = pos=(-9,23.8547,37.4253) rot=(-0.644711,-0.410726,0.644711;2.36216rad)
  SolverId = Asm4EE
  diameter = 3
  invert = true
  length = 0
  lengthCustom = 8
  matchOuter = true
  offset = 0
  thread = false
  type = 18
  expr: Placement = Tip_Remover_Bracket.Placement * Tip_Remover_Bracket#LCS_Tip_Remover_Bracket_Hole_2_Outside.Placement * AttachmentOffset
FEATURE [Part::FeaturePython] Screw017  label="M10x80-Screw"  # Fasteners workbench fastener (typed FeaturePython)
  AssemblyType = Part::Link
  AttachedBy = Origin
  AttachedTo = Spool_Screw_Knob#LCS_Spool_Screw_Knob_2
  AttachmentOffset = pos=(0,0,0) rot=(1,0,0;3.14159rad)
  Placement = pos=(38,171,40) rot=(0.57735,0.57735,0.57735;4.18879rad)
  SolverId = Asm4EE
  diameter = 10
  invert = false
  length = 8
  lengthCustom = 80
  matchOuter = true
  offset = 0
  thread = false
  type = 28
  expr: Placement = Spool_Screw_Knob.Placement * Spool_Knob#LCS_Spool_Screw_Knob_2.Placement * AttachmentOffset
FEATURE [Part::FeaturePython] Screw019  label="M3x25-Screw"  # Fasteners workbench fastener (typed FeaturePython)
  AssemblyType = Part::Link
  AttachedBy = Origin
  AttachedTo = Tip_Remover_Bracket#LCS_Tip_Remover_Bracket_Hole_1_Outside
  AttachmentOffset = pos=(0,0,9) rot=(0,0,1;0rad)
  Placement = pos=(-18,37.144,42.2622) rot=(-0.644711,-0.410726,0.644711;2.36216rad)
  SolverId = Asm4EE
  diameter = 4
  invert = false
  length = 8
  lengthCustom = 25
  matchOuter = true
  offset = 0
  thread = false
  type = 34
  expr: Placement = Tip_Remover_Bracket.Placement * Tip_Remover_Bracket#LCS_Tip_Remover_Bracket_Hole_1_Outside.Placement * AttachmentOffset
FEATURE [Part::FeaturePython] Washer  label="M3-Washer"  # Fasteners workbench fastener (typed FeaturePython)
  AssemblyType = Part::Link
  AttachedBy = Origin
  AttachedTo = Tip_Remover_Bracket#LCS_Tip_Remover_Bracket_Hole_1_Outside
  AttachmentOffset = pos=(0,0,-9) rot=(1,0,0;3.14159rad)
  Placement = pos=(0,37.144,42.2622) rot=(0.473306,0.742942,0.473306;1.86366rad)
  SolverId = Asm4EE
  diameter = 4
  invert = false
  matchOuter = true
  offset = 0
  type = 3
  expr: Placement = Tip_Remover_Bracket.Placement * Tip_Remover_Bracket#LCS_Tip_Remover_Bracket_Hole_1_Outside.Placement * AttachmentOffset
FEATURE [Part::FeaturePython] Nut  label="M3-Nut"  # Fasteners workbench fastener (typed FeaturePython)
  AssemblyType = Part::Link
  AttachedBy = Origin
  AttachedTo = Tip_Remover_Bracket#LCS_Tip_Remover_Bracket_Hole_1_Outside
  AttachmentOffset = pos=(0,0,-9.6) rot=(1,0,0;3.14159rad)
  Placement = pos=(0.6,37.144,42.2622) rot=(0.473306,0.742942,0.473306;1.86366rad)
  SolverId = Asm4EE
  diameter = 1
  invert = false
  matchOuter = true
  offset = 0
  thread = false
  type = 5
  expr: Placement = Tip_Remover_Bracket.Placement * Tip_Remover_Bracket#LCS_Tip_Remover_Bracket_Hole_1_Outside.Placement * AttachmentOffset
FEATURE [App::DocumentObjectGroup] Tip_Remover_Fasteners
  Group = -> [Screw013,Screw019,Washer,Nut]
FEATURE [Sketcher::SketchObject] Master_Top_Pad_Sketch  label="Master_Rubber_Pad_Sketch"
  FullyConstrained = true
  MapMode = 5
  Support = -> [XY_Plane]
  expr: Constraints[18] = Master_Top_Sketch.Constraints[18]
  expr: Constraints[19] = Master_Top_Sketch.Constraints[19]
  expr: Constraints[22] = Master_Top_Sketch.Constraints[22]
  expr: Constraints[23] = Master_Top_Sketch.Constraints[23]
  expr: Constraints[25] = Master_Top_Sketch.Constraints[25]
  expr: Constraints[41] = Master_Top_Sketch.Constraints[41]
  expr: Constraints[42] = Master_Top_Sketch.Constraints[42]
  expr: Constraints[43] = Master_Top_Sketch.Constraints[43]
  expr: Constraints[44] = Master_Top_Sketch.Constraints[44]
  expr: Constraints[51] = Master_Top_Sketch.Constraints[51]
  expr: Constraints[52] = Master_Top_Sketch.Constraints[52]
  expr: Constraints[54] = Master_Top_Sketch.Constraints[54]
  expr: Constraints[58] = Master_Top_Sketch.Constraints[58]
  sketch-geometry (28):
    g0: LineSegment StartX=0 StartY=168 StartZ=0 EndX=0 EndY=0 EndZ=0
    g1: LineSegment StartX=70 StartY=168 StartZ=0 EndX=0 EndY=168 EndZ=0
    g2: LineSegment StartX=90 StartY=20 StartZ=0 EndX=90 EndY=148 EndZ=0
    g3: LineSegment StartX=0 StartY=0 StartZ=0 EndX=70 EndY=0 EndZ=0
    g4: LineSegment StartX=70 StartY=168 StartZ=0 EndX=90 EndY=148 EndZ=0
    g5: LineSegment StartX=70 StartY=0 StartZ=0 EndX=90 EndY=20 EndZ=0
    g6: LineSegment StartX=90 StartY=20 StartZ=0 EndX=90 EndY=0 EndZ=0
    g7: LineSegment StartX=70 StartY=0 StartZ=0 EndX=90 EndY=0 EndZ=0
    g8: Circle CenterX=85 CenterY=131.5 CenterZ=0 NormalX=0 NormalY=0 NormalZ=1 AngleXU=0 Radius=1.5
    g9: Circle CenterX=85 CenterY=36.5 CenterZ=0 NormalX=0 NormalY=0 NormalZ=1 AngleXU=0 Radius=1.5
    g10: LineSegment StartX=38 StartY=35 StartZ=0 EndX=38 EndY=0 EndZ=0
    g11: Circle CenterX=18 CenterY=165 CenterZ=0 NormalX=0 NormalY=0 NormalZ=1 AngleXU=0 Radius=1.5
    g12: Circle CenterX=48 CenterY=165 CenterZ=0 NormalX=0 NormalY=0 NormalZ=1 AngleXU=0 Radius=1.5
    g13: Circle CenterX=18 CenterY=95 CenterZ=0 NormalX=0 NormalY=0 NormalZ=1 AngleXU=0 Radius=1.5
    g14: Circle CenterX=48 CenterY=95 CenterZ=0 NormalX=0 NormalY=0 NormalZ=1 AngleXU=0 Radius=1.5
    g15: LineSegment StartX=18 StartY=95 StartZ=0 EndX=48 EndY=95 EndZ=0
    g16: LineSegment StartX=48 StartY=95 StartZ=0 EndX=48 EndY=165 EndZ=0
    g17: LineSegment StartX=48 StartY=165 StartZ=0 EndX=18 EndY=165 EndZ=0
    g18: LineSegment StartX=18 StartY=165 StartZ=0 EndX=18 EndY=95 EndZ=0
    g19: LineSegment StartX=85 StartY=36.5 StartZ=0 EndX=85 EndY=131.5 EndZ=0
    g20: LineSegment StartX=85 StartY=84 StartZ=0 EndX=0 EndY=84 EndZ=0
    g21: Circle CenterX=23 CenterY=35 CenterZ=0 NormalX=0 NormalY=0 NormalZ=1 AngleXU=0 Radius=1.5
    g22: Circle CenterX=53 CenterY=35 CenterZ=0 NormalX=0 NormalY=0 NormalZ=1 AngleXU=0 Radius=1.5
    g23: Circle CenterX=10 CenterY=18.4853 CenterZ=0 NormalX=0 NormalY=0 NormalZ=1 AngleXU=0 Radius=10
    g24: Circle CenterX=71.5147 CenterY=18.4853 CenterZ=0 NormalX=0 NormalY=0 NormalZ=1 AngleXU=0 Radius=10
    g25: Circle CenterX=71.5147 CenterY=149.515 CenterZ=0 NormalX=0 NormalY=0 NormalZ=1 AngleXU=0 Radius=10
    g26: Circle CenterX=10 CenterY=149.515 CenterZ=0 NormalX=0 NormalY=0 NormalZ=1 AngleXU=0 Radius=10
    g27: LineSegment StartX=71.5147 StartY=18.4853 StartZ=0 EndX=80 EndY=10 EndZ=0
  constraints (73):
    c: Coincident(g1,g0)
    c: Coincident(g0,g3)
    c: Coincident(g3,g-1)
    c: Horizontal(g1)
    c: Vertical(g2)
    c: Horizontal(g3)
    c: Coincident(g5,g3)
    c: Vertical(g3,g1)
    c: Coincident(g1,g4)
    c: Coincident(g2,g4)
    c: Coincident(g2,g5)
    c: Equal(g5,g4)
    c: Coincident(g6,g2)
    c: PointOnObject(g6,g-1)
    c: Coincident(g7,g3)
    c: Coincident(g7,g6)
    c: Vertical(g6)
    c: Equal(g7,g6)
    c: DistanceX(g7,g7) = 20
    c: DistanceX(g0,g6) = 90
    c: Vertical(g9,g8)
    c: Vertical(g10)
    c: DistanceY(g10,g10) = 35
    c: DistanceY(g9,g8) = 95
    c: Equal(g9,g8)
    c: DistanceX(g9,g2) = 5
    c: Coincident(g15,g16)
    c: Coincident(g16,g17)
    c: Coincident(g17,g18)
    c: Coincident(g18,g15)
    c: Horizontal(g15)
    c: Horizontal(g17)
    c: Vertical(g16)
    c: Vertical(g18)
    c: Coincident(g15,g13)
    c: Coincident(g16,g12)
    c: Coincident(g14,g15)
    c: Coincident(g11,g17)
    c: Equal(g11,g12)
    c: Equal(g12,g14)
    c: Equal(g14,g13)
    c: Diameter(g11) = 3
    c: DistanceY(g11,g0) = 3
    c: DistanceX(g0,g11) = 18
    c: DistanceX(g17,g17) = 30
    c: Equal(g8,g11)
    c: Coincident(g19,g9)
    c: Coincident(g19,g8)
    c: Horizontal(g20)
    c: Symmetric(g9,g8,g20)
    c: Symmetric(g0,g0,g20)
    c: DistanceY(g0,g0) = 168
    c: DistanceY(g18,g18) = 70
    c: PointOnObject(g0,g-2)
    c: DistanceX(g0,g10) = 38
    c: PointOnObject(g10,g3)
    c: Horizontal(g21,g22)
    c: Symmetric(g21,g22,g10)
    c: DistanceX(g21,g22) = 30
    c: Equal(g22,g21)
    c: Equal(g21,g11)
    c: Equal(g23,g26)
    c: Equal(g23,g25)
    c: Equal(g23,g24)
    c: Diameter(g23) = 20
    c: Symmetric(g23,g26,g20)
    c: Symmetric(g24,g25,g20)
    c: DistanceX(g0,g23) = 10
    c: Coincident(g27,g24)
    c: Perpendicular(g27,g5)
    c: Symmetric(g3,g2,g27)
    c: Distance(g27) = 12
    c: Horizontal(g23,g24)
FEATURE [PartDesign::CoordinateSystem] LCS_Rubber_Pad_1
  AttacherType = Attacher::AttachEngine3D
  MapMode = 11
  Placement = pos=(10,18.4853,0) rot=(0,0,1;1.5708rad)
  Support = -> [Master_Top_Pad_Sketch]
FEATURE [PartDesign::CoordinateSystem] LCS_Rubber_Pad_2
  AttacherType = Attacher::AttachEngine3D
  MapMode = 11
  Placement = pos=(10,149.515,0) rot=(0,0,1;1.5708rad)
  Support = -> [Master_Top_Pad_Sketch]
FEATURE [PartDesign::CoordinateSystem] LCS_Rubber_Pad_3
  AttacherType = Attacher::AttachEngine3D
  AttachmentOffset = pos=(0,0,0) rot=(0,0,1;0.785398rad)
  MapMode = 11
  Placement = pos=(71.5147,149.515,0) rot=(0,0,1;2.35619rad)
  Support = -> [Master_Top_Pad_Sketch]
FEATURE [PartDesign::CoordinateSystem] LCS_Rubber_Pad_4
  AttacherType = Attacher::AttachEngine3D
  AttachmentOffset = pos=(0,0,0) rot=(0,0,1;0.785398rad)
  MapMode = 11
  Placement = pos=(71.5147,18.4853,0) rot=(0,0,1;2.35619rad)
  Support = -> [Master_Top_Pad_Sketch]
FEATURE [App::Link] Rubber_Pad_1
  AssemblyType = Part::Link
  AttachedBy = #LCS_1
  AttachedTo = Parent Assembly#LCS_Rubber_Pad_1
  LinkPlacement = pos=(10,18.4853,0) rot=(-0.707107,-0.707107,0;3.14159rad)
  LinkedObject = -> <external Parts/Rubber Pad.FCStd>#Body
  Placement = pos=(10,18.4853,0) rot=(-0.707107,-0.707107,0;3.14159rad)
  SolverId = Asm4EE
  expr: Placement = LCS_Rubber_Pad_1.Placement * AttachmentOffset * Rubber_Pad#LCS_1.Placement ^ -1
FEATURE [App::Link] Rubber_Pad_2
  AssemblyType = Part::Link
  AttachedBy = #LCS_1
  AttachedTo = Parent Assembly#LCS_Rubber_Pad_2
  LinkPlacement = pos=(10,149.515,0) rot=(-0.707107,-0.707107,0;3.14159rad)
  LinkedObject = -> <external Parts/Rubber Pad.FCStd>#Body
  Placement = pos=(10,149.515,0) rot=(-0.707107,-0.707107,0;3.14159rad)
  SolverId = Asm4EE
  expr: Placement = LCS_Rubber_Pad_2.Placement * AttachmentOffset * Rubber_Pad#LCS_1.Placement ^ -1
FEATURE [App::Link] Rubber_Pad_3
  AssemblyType = Part::Link
  AttachedBy = #LCS_1
  AttachedTo = Parent Assembly#LCS_Rubber_Pad_3
  LinkPlacement = pos=(71.5147,149.515,0) rot=(-0.382683,-0.92388,0;3.14159rad)
  LinkedObject = -> <external Parts/Rubber Pad.FCStd>#Body
  Placement = pos=(71.5147,149.515,0) rot=(-0.382683,-0.92388,0;3.14159rad)
  SolverId = Asm4EE
  expr: Placement = LCS_Rubber_Pad_3.Placement * AttachmentOffset * Rubber_Pad#LCS_1.Placement ^ -1
FEATURE [App::Link] Rubber_Pad_4
  AssemblyType = Part::Link
  AttachedBy = #LCS_1
  AttachedTo = Parent Assembly#LCS_Rubber_Pad_4
  LinkPlacement = pos=(71.5147,18.4853,0) rot=(-0.382683,-0.92388,0;3.14159rad)
  LinkedObject = -> <external Parts/Rubber Pad.FCStd>#Body
  Placement = pos=(71.5147,18.4853,0) rot=(-0.382683,-0.92388,0;3.14159rad)
  SolverId = Asm4EE
  expr: Placement = LCS_Rubber_Pad_4.Placement * AttachmentOffset * Rubber_Pad#LCS_1.Placement ^ -1
FEATURE [App::DocumentObjectGroup] Rubber_Pads
  Group = -> [Rubber_Pad_1,Rubber_Pad_2,Rubber_Pad_3,Rubber_Pad_4]
FEATURE [App::DocumentObjectGroup] Parts
  Group = -> [Tool_Holder,Tool_Holder_Adapter,Tool_Holder_Washer,Tool_Holder_Screw,Tip_Cleaner,Tip_Remover_Bracket,Tip_Magazine,Spool_Screw_Knob,Connector_Minijack,Rubber_Pads,Dummy_Parts]
FEATURE [PartDesign::CoordinateSystem] LCS_Assembly_Handle_Hole_1
  AttacherType = Attacher::AttachEngine3D
  AttachmentOffset = pos=(0,0,-5) rot=(0,0,1;0rad)
  MapMode = 11
  Placement = pos=(48,103,110) rot=(0.57735,-0.57735,0.57735;2.0944rad)
  Support = -> [Sketch037]
FEATURE [PartDesign::CoordinateSystem] LCS_Assembly_Handle_Hole_2
  AttacherType = Attacher::AttachEngine3D
  AttachmentOffset = pos=(0,0,-5) rot=(0,0,1;0rad)
  MapMode = 11
  Placement = pos=(28,103,110) rot=(0.57735,-0.57735,0.57735;2.0944rad)
  Support = -> [Sketch037]
FEATURE [PartDesign::Line] HoleAxis_1
  AttacherType = Attacher::AttachEngineLine
  Length = 4.2272
  MapMode = 19
  Placement = pos=(48,165,0) rot=(0,0,1;0rad)
  ResizeMode = 1
  Support = -> [Master_Top_Screw_Sketch]
FEATURE [PartDesign::Line] HoleAxis_2
  AttacherType = Attacher::AttachEngineLine
  Length = 4.2272
  MapMode = 19
  Placement = pos=(18,165,0) rot=(0,0,1;0rad)
  ResizeMode = 1
  Support = -> [Master_Top_Screw_Sketch]
FEATURE [PartDesign::Line] HoleAxis_3
  AttacherType = Attacher::AttachEngineLine
  Length = 4.2272
  MapMode = 19
  Placement = pos=(18,95,0) rot=(0,0,1;0rad)
  ResizeMode = 1
  Support = -> [Master_Top_Screw_Sketch]
FEATURE [PartDesign::Line] HoleAxis_4
  AttacherType = Attacher::AttachEngineLine
  Length = 4.2272
  MapMode = 19
  Placement = pos=(48,95,0) rot=(0,0,1;0rad)
  ResizeMode = 1
  Support = -> [Master_Top_Screw_Sketch]
FEATURE [PartDesign::Line] HoleAxis_5
  AttacherType = Attacher::AttachEngineLine
  Length = 4.2272
  MapMode = 19
  Placement = pos=(85,131.5,0) rot=(0,0,1;0rad)
  ResizeMode = 1
  Support = -> [Master_Top_Screw_Sketch]
FEATURE [PartDesign::Line] HoleAxis_6
  AttacherType = Attacher::AttachEngineLine
  Length = 4.2272
  MapMode = 19
  Placement = pos=(85,36.5,0) rot=(0,0,1;0rad)
  ResizeMode = 1
  Support = -> [Master_Top_Screw_Sketch]
FEATURE [PartDesign::Line] HoleAxis_7
  AttacherType = Attacher::AttachEngineLine
  Length = 4.2272
  MapMode = 19
  Placement = pos=(53,35,0) rot=(0,0,1;0rad)
  ResizeMode = 1
  Support = -> [Master_Top_Screw_Sketch]
FEATURE [PartDesign::Line] HoleAxis_8
  AttacherType = Attacher::AttachEngineLine
  Length = 4.2272
  MapMode = 19
  Placement = pos=(23,35,0) rot=(0,0,1;0rad)
  ResizeMode = 1
  Support = -> [Master_Top_Screw_Sketch]
FEATURE [PartDesign::Line] HoleAxis_9
  AttacherType = Attacher::AttachEngineLine
  Length = 4.2272
  MapMode = 19
  Placement = pos=(-6,158,3) rot=(0.57735,0.57735,0.57735;2.0944rad)
  ResizeMode = 1
  Support = -> [Master_Side_Screw_Sketch]
FEATURE [PartDesign::Line] HoleAxis_10
  AttacherType = Attacher::AttachEngineLine
  Length = 4.2272
  MapMode = 19
  Placement = pos=(-6,108.667,3) rot=(0.57735,0.57735,0.57735;2.0944rad)
  ResizeMode = 1
  Support = -> [Master_Side_Screw_Sketch]
FEATURE [PartDesign::Line] HoleAxis_11
  AttacherType = Attacher::AttachEngineLine
  Length = 4.2272
  MapMode = 19
  Placement = pos=(-6,59.3333,3) rot=(0.57735,0.57735,0.57735;2.0944rad)
  ResizeMode = 1
  Support = -> [Master_Side_Screw_Sketch]
FEATURE [PartDesign::Line] HoleAxis_12
  AttacherType = Attacher::AttachEngineLine
  Length = 4.2272
  MapMode = 19
  Placement = pos=(-6,10,3) rot=(0.57735,0.57735,0.57735;2.0944rad)
  ResizeMode = 1
  Support = -> [Master_Side_Screw_Sketch]
FEATURE [PartDesign::Line] HoleAxis_13
  AttacherType = Attacher::AttachEngineLine
  Length = 4.2272
  MapMode = 19
  Placement = pos=(-6,165,45) rot=(0.57735,0.57735,0.57735;2.0944rad)
  ResizeMode = 1
  Support = -> [Master_Side_Screw_Sketch]
FEATURE [PartDesign::Line] HoleAxis_14
  AttacherType = Attacher::AttachEngineLine
  Length = 4.2272
  MapMode = 19
  Placement = pos=(-6,95,45) rot=(0.57735,0.57735,0.57735;2.0944rad)
  ResizeMode = 1
  Support = -> [Master_Side_Screw_Sketch]
FEATURE [PartDesign::Line] HoleAxis_15
  AttacherType = Attacher::AttachEngineLine
  Length = 4.2272
  MapMode = 19
  Placement = pos=(-6,57,65) rot=(0.57735,0.57735,0.57735;2.0944rad)
  ResizeMode = 1
  Support = -> [Master_Side_Screw_Sketch]
FEATURE [App::DocumentObjectGroup] Bottom_Hole_Axis
  Group = -> [HoleAxis_1,HoleAxis_2,HoleAxis_3,HoleAxis_4,HoleAxis_5,HoleAxis_6,HoleAxis_7,HoleAxis_8]
FEATURE [App::DocumentObjectGroup] Side_Hole_Axis
  Group = -> [HoleAxis_9,HoleAxis_10,HoleAxis_11,HoleAxis_12,HoleAxis_13,HoleAxis_14,HoleAxis_15]
FEATURE [App::DocumentObjectGroup] LCS
  Group = -> [Sketch037,Sketch014,Master_Top_Sketch,Master_Side_Screw_Sketch,Master_Top_Screw_Sketch,LCS_Assembly_Handle,LCS_Tool_Holder_Adapter,LCS_Tool_Holder_Washer,LCS_Spool_Screw,LCS_Assembly_Rear_Connector,LCS_Assembly_Tip_Cleaner,LCS_Assembly_Tip_Magazine,LCS_Assembly_Spool,LCS_Assembly_Tip_Remover,Master_Top_Pad_Sketch,LCS_Rubber_Pad_1,LCS_Rubber_Pad_2,LCS_Rubber_Pad_3,LCS_Rubber_Pad_4,+4 more]
FEATURE [Part::FeaturePython] Screw021  label="M3x16-Screw629"  # Fasteners workbench fastener (typed FeaturePython)
  AssemblyType = Part::Link
  AttachedBy = Origin
  AttachedTo = Parent Assembly#HoleAxis_2
  AttachmentOffset = pos=(0,0,0) rot=(1,0,0;3.14159rad)
  Placement = pos=(18,165,0) rot=(1,0,0;3.14159rad)
  SolverId = Asm4EE
  diameter = 3
  invert = true
  length = 3
  lengthCustom = 16
  matchOuter = true
  offset = 0
  thread = false
  type = 18
  expr: Placement = HoleAxis_2.Placement * AttachmentOffset
FEATURE [Part::FeaturePython] Screw022  label="M3x16-Screw630"  # Fasteners workbench fastener (typed FeaturePython)
  AssemblyType = Part::Link
  AttachedBy = Origin
  AttachedTo = Parent Assembly#HoleAxis_3
  AttachmentOffset = pos=(0,0,0) rot=(1,0,0;3.14159rad)
  Placement = pos=(18,95,0) rot=(1,0,0;3.14159rad)
  SolverId = Asm4EE
  diameter = 3
  invert = true
  length = 3
  lengthCustom = 16
  matchOuter = true
  offset = 0
  thread = false
  type = 18
  expr: Placement = HoleAxis_3.Placement * AttachmentOffset
FEATURE [Part::FeaturePython] Screw023  label="M3x16-Screw631"  # Fasteners workbench fastener (typed FeaturePython)
  AssemblyType = Part::Link
  AttachedBy = Origin
  AttachedTo = Parent Assembly#HoleAxis_4
  AttachmentOffset = pos=(0,0,0) rot=(1,0,0;3.14159rad)
  Placement = pos=(48,95,0) rot=(1,0,0;3.14159rad)
  SolverId = Asm4EE
  diameter = 3
  invert = true
  length = 3
  lengthCustom = 16
  matchOuter = true
  offset = 0
  thread = false
  type = 18
  expr: Placement = HoleAxis_4.Placement * AttachmentOffset
FEATURE [Part::FeaturePython] Screw024  label="M3x16-Screw632"  # Fasteners workbench fastener (typed FeaturePython)
  AssemblyType = Part::Link
  AttachedBy = Origin
  AttachedTo = Parent Assembly#HoleAxis_5
  AttachmentOffset = pos=(0,0,0) rot=(1,0,0;3.14159rad)
  Placement = pos=(85,131.5,0) rot=(1,0,0;3.14159rad)
  SolverId = Asm4EE
  diameter = 3
  invert = true
  length = 3
  lengthCustom = 16
  matchOuter = true
  offset = 0
  thread = false
  type = 18
  expr: Placement = HoleAxis_5.Placement * AttachmentOffset
FEATURE [Part::FeaturePython] Screw025  label="M3x16-Screw633"  # Fasteners workbench fastener (typed FeaturePython)
  AssemblyType = Part::Link
  AttachedBy = Origin
  AttachedTo = Parent Assembly#HoleAxis_6
  AttachmentOffset = pos=(0,0,0) rot=(1,0,0;3.14159rad)
  Placement = pos=(85,36.5,0) rot=(1,0,0;3.14159rad)
  SolverId = Asm4EE
  diameter = 3
  invert = true
  length = 3
  lengthCustom = 16
  matchOuter = true
  offset = 0
  thread = false
  type = 18
  expr: Placement = HoleAxis_6.Placement * AttachmentOffset
FEATURE [Part::FeaturePython] Screw026  label="M3x16-Screw622"  # Fasteners workbench fastener (typed FeaturePython)
  AssemblyType = Part::Link
  AttachedBy = Origin
  AttachedTo = Parent Assembly#HoleAxis_9
  AttachmentOffset = pos=(0,0,0) rot=(1,0,0;3.14159rad)
  Placement = pos=(-6,158,3) rot=(0.57735,0.57735,-0.57735;4.18879rad)
  SolverId = Asm4EE
  diameter = 3
  invert = true
  length = 3
  lengthCustom = 16
  matchOuter = true
  offset = 0
  thread = false
  type = 18
  expr: Placement = HoleAxis_9.Placement * AttachmentOffset
FEATURE [Part::FeaturePython] Screw027  label="M3x16-Screw623"  # Fasteners workbench fastener (typed FeaturePython)
  AssemblyType = Part::Link
  AttachedBy = Origin
  AttachedTo = Parent Assembly#HoleAxis_10
  AttachmentOffset = pos=(0,0,0) rot=(1,0,0;3.14159rad)
  Placement = pos=(-6,108.667,3) rot=(0.57735,0.57735,-0.57735;4.18879rad)
  SolverId = Asm4EE
  diameter = 3
  invert = true
  length = 3
  lengthCustom = 16
  matchOuter = true
  offset = 0
  thread = false
  type = 18
  expr: Placement = HoleAxis_10.Placement * AttachmentOffset
FEATURE [Part::FeaturePython] Screw028  label="M3x16-Screw624"  # Fasteners workbench fastener (typed FeaturePython)
  AssemblyType = Part::Link
  AttachedBy = Origin
  AttachedTo = Parent Assembly#HoleAxis_11
  AttachmentOffset = pos=(0,0,0) rot=(1,0,0;3.14159rad)
  Placement = pos=(-6,59.3333,3) rot=(0.57735,0.57735,-0.57735;4.18879rad)
  SolverId = Asm4EE
  diameter = 3
  invert = true
  length = 3
  lengthCustom = 16
  matchOuter = true
  offset = 0
  thread = false
  type = 18
  expr: Placement = HoleAxis_11.Placement * AttachmentOffset
FEATURE [Part::FeaturePython] Screw029  label="M3x16-Screw625"  # Fasteners workbench fastener (typed FeaturePython)
  AssemblyType = Part::Link
  AttachedBy = Origin
  AttachedTo = Parent Assembly#HoleAxis_12
  AttachmentOffset = pos=(0,0,0) rot=(1,0,0;3.14159rad)
  Placement = pos=(-6,10,3) rot=(0.57735,0.57735,-0.57735;4.18879rad)
  SolverId = Asm4EE
  diameter = 3
  invert = true
  length = 3
  lengthCustom = 16
  matchOuter = true
  offset = 0
  thread = false
  type = 18
  expr: Placement = HoleAxis_12.Placement * AttachmentOffset
FEATURE [Part::FeaturePython] Screw030  label="M3x16-Screw626"  # Fasteners workbench fastener (typed FeaturePython)
  AssemblyType = Part::Link
  AttachedBy = Origin
  AttachedTo = Parent Assembly#HoleAxis_13
  AttachmentOffset = pos=(0,0,0) rot=(1,0,0;3.14159rad)
  Placement = pos=(-6,165,45) rot=(0.57735,0.57735,-0.57735;4.18879rad)
  SolverId = Asm4EE
  diameter = 3
  invert = true
  length = 3
  lengthCustom = 16
  matchOuter = true
  offset = 0
  thread = false
  type = 18
  expr: Placement = HoleAxis_13.Placement * AttachmentOffset
FEATURE [Part::FeaturePython] Screw031  label="M3x16-Screw627"  # Fasteners workbench fastener (typed FeaturePython)
  AssemblyType = Part::Link
  AttachedBy = Origin
  AttachedTo = Parent Assembly#HoleAxis_14
  AttachmentOffset = pos=(0,0,0) rot=(1,0,0;3.14159rad)
  Placement = pos=(-6,95,45) rot=(0.57735,0.57735,-0.57735;4.18879rad)
  SolverId = Asm4EE
  diameter = 3
  invert = true
  length = 3
  lengthCustom = 16
  matchOuter = true
  offset = 0
  thread = false
  type = 18
  expr: Placement = HoleAxis_14.Placement * AttachmentOffset
FEATURE [Part::FeaturePython] Screw032  label="M3x16-Screw628"  # Fasteners workbench fastener (typed FeaturePython)
  AssemblyType = Part::Link
  AttachedBy = Origin
  AttachedTo = Parent Assembly#HoleAxis_15
  AttachmentOffset = pos=(0,0,0) rot=(1,0,0;3.14159rad)
  Placement = pos=(-6,57,65) rot=(0.57735,0.57735,-0.57735;4.18879rad)
  SolverId = Asm4EE
  diameter = 3
  invert = true
  length = 3
  lengthCustom = 16
  matchOuter = true
  offset = 0
  thread = false
  type = 18
  expr: Placement = HoleAxis_15.Placement * AttachmentOffset
FEATURE [App::DocumentObjectGroup] Side001  label="Side_Fasteners"
  Group = -> [Screw026,Screw027,Screw028,Screw029,Screw030,Screw031,Screw032]
FEATURE [Part::FeaturePython] Screw033  label="M3x16-Screw620"  # Fasteners workbench fastener (typed FeaturePython)
  AssemblyType = Part::Link
  AttachedBy = Origin
  AttachedTo = Parent Assembly#LCS_Assembly_Handle_Hole_1
  AttachmentOffset = pos=(0,0,0) rot=(1,0,0;3.14159rad)
  Placement = pos=(48,103,110) rot=(0.57735,0.57735,0.57735;4.18879rad)
  SolverId = Asm4EE
  diameter = 3
  invert = true
  length = 3
  lengthCustom = 16
  matchOuter = true
  offset = 0
  thread = false
  type = 18
  expr: Placement = LCS_Assembly_Handle_Hole_1.Placement * AttachmentOffset
FEATURE [Part::FeaturePython] Screw034  label="M3x16-Screw621"  # Fasteners workbench fastener (typed FeaturePython)
  AssemblyType = Part::Link
  AttachedBy = Origin
  AttachedTo = Parent Assembly#LCS_Assembly_Handle_Hole_2
  AttachmentOffset = pos=(0,0,0) rot=(1,0,0;3.14159rad)
  Placement = pos=(28,103,110) rot=(0.57735,0.57735,0.57735;4.18879rad)
  SolverId = Asm4EE
  diameter = 3
  invert = true
  length = 3
  lengthCustom = 16
  matchOuter = true
  offset = 0
  thread = false
  type = 18
  expr: Placement = LCS_Assembly_Handle_Hole_2.Placement * AttachmentOffset
FEATURE [App::DocumentObjectGroup] Rear001  label="Rear_Fasteners"
  Group = -> [Screw017,Screw033,Screw034]
FEATURE [Part::FeaturePython] Screw035  label="M3x8-Screw087"  # Fasteners workbench fastener (typed FeaturePython)
  AssemblyType = Part::Link
  AttachedBy = Origin
  AttachedTo = Parent Assembly#HoleAxis_7
  AttachmentOffset = pos=(0,0,0) rot=(1,0,0;3.14159rad)
  Placement = pos=(53,35,0) rot=(1,0,0;3.14159rad)
  SolverId = Asm4EE
  diameter = 3
  invert = true
  length = 0
  lengthCustom = 8
  matchOuter = true
  offset = 0
  thread = false
  type = 18
  expr: Placement = HoleAxis_7.Placement * AttachmentOffset
FEATURE [Part::FeaturePython] Screw036  label="M3x8-Screw088"  # Fasteners workbench fastener (typed FeaturePython)
  AssemblyType = Part::Link
  AttachedBy = Origin
  AttachedTo = Parent Assembly#HoleAxis_8
  AttachmentOffset = pos=(0,0,0) rot=(1,0,0;3.14159rad)
  Placement = pos=(23,35,0) rot=(1,0,0;3.14159rad)
  SolverId = Asm4EE
  diameter = 3
  invert = true
  length = 0
  lengthCustom = 8
  matchOuter = true
  offset = 0
  thread = false
  type = 18
  expr: Placement = HoleAxis_8.Placement * AttachmentOffset
FEATURE [App::DocumentObjectGroup] Bottom  label="Bottom_Fasteners"
  Group = -> [Screw,Screw021,Screw022,Screw023,Screw024,Screw025,Screw035,Screw036]
FEATURE [App::DocumentObjectGroup] Fasteners
  Group = -> [Rear001,Side001,Bottom,Tip_Remover_Fasteners]
FEATURE [Spreadsheet::Sheet] Default
  cells = A1=Asm4::ConfigurationTable; A2=0; A4=ObjectName; B4=Visible; C4=Assembly Type; D4=Pos. X; E4=Pos. Y; F4=Pos. Z; G4=Rot. Yaw; H4=Rot. Pitch; I4=Rot. Roll; A5(AssemblyNut)=Assembly.Nut; B5=True; C5=Asm4EE; D5=0; E5=0; F5=-9.6; G5=0; H5=0; I5=180; A6(AssemblyWasher)=Assembly.Washer; B6=True; C6=Asm4EE; D6=0; E6=0; F6=-9; G6=0; H6=0; I6=180; A7(AssemblyScrew019)=Assembly.Screw019; B7=True; C7=Asm4EE; D7=0; E7=0; F7=9; G7=0; H7=0; I7=0; A8(AssemblyScrew013)=Assembly.Screw013; B8=True; C8=Asm4EE; D8=0; E8=0; F8=0; G8=0; H8=-0; I8=-2.544443745170813e-14; A9(AssemblyScrew036)=Assembly.Screw036; B9=True; C9=Asm4EE; D9=0; E9=0; F9=0; G9=0; H9=0; I9=180; A10(AssemblyScrew035)=Assembly.Screw035; B10=True; C10=Asm4EE; D10=0; E10=0; F10=0; G10=0; H10=0; I10=180; A11(AssemblyScrew025)=Assembly.Screw025; B11=True; C11=Asm4EE; D11=0; E11=0; F11=0; G11=0; H11=0; I11=180; A12(AssemblyScrew024)=Assembly.Screw024; B12=True; C12=Asm4EE; D12=0; E12=0; F12=0; G12=0; H12=0; I12=180; A13(AssemblyScrew023)=Assembly.Screw023; B13=True; C13=Asm4EE; D13=0; E13=0; F13=0; G13=0; H13=0; I13=180; A14(AssemblyScrew022)=Assembly.Screw022; B14=True; C14=Asm4EE; D14=0; E14=0; F14=0; G14=0; H14=0; I14=180; A15(AssemblyScrew021)=Assembly.Screw021; B15=True; C15=Asm4EE; D15=0; E15=0; F15=0; G15=0; H15=0; I15=180; A16(AssemblyScrew020)=Assembly.Screw020; B16=True; C16=Asm4EE; D16=0; E16=0; F16=0; G16=0; H16=0; I16=180; A17(AssemblyScrew)=Assembly.Screw; B17=True; C17=Asm4EE; D17=0; E17=0; F17=0; G17=0; H17=0; I17=180; A18(AssemblyScrew032)=Assembly.Screw032; B18=True; C18=Asm4EE; D18=0; E18=0; F18=0; G18=0; H18=0; I18=180; A19(AssemblyScrew031)=Assembly.Screw031; B19=True; C19=Asm4EE; D19=0; E19=0; F19=0; G19=0; H19=0; I19=180; A20(AssemblyScrew030)=Assembly.Screw030; B20=True; C20=Asm4EE; D20=0; E20=0; F20=0; G20=0; H20=0; I20=180; A21(AssemblyScrew029)=Assembly.Screw029; B21=True; C21=Asm4EE; D21=0; E21=0; F21=0; G21=0; H21=0; I21=180; A22(AssemblyScrew028)=Assembly.Screw028; B22=True; C22=Asm4EE; D22=0; E22=0; F22=0; G22=0; H22=0; I22=180; A23(AssemblyScrew027)=Assembly.Screw027; B23=True; C23=Asm4EE; D23=0; E23=0; F23=0; G23=0; H23=0; I23=180; A24(AssemblyScrew026)=Assembly.Screw026; B24=True; C24=Asm4EE; D24=0; E24=0; F24=0; G24=0; H24=0; I24=180; A25(AssemblyScrew034)=Assembly.Screw034; B25=True; C25=Asm4EE; D25=0; E25=0; F25=0; G25=0; H25=0; I25=180; +318 more cells
FEATURE [Spreadsheet::Sheet] No_Dummy_Models
  cells = A1=Asm4::ConfigurationTable; A2=0; A4=ObjectName; B4=Visible; C4=Assembly Type; D4=Pos. X; E4=Pos. Y; F4=Pos. Z; G4=Rot. Yaw; H4=Rot. Pitch; I4=Rot. Roll; A5(AssemblyNut)=Assembly.Nut; B5=True; C5=Asm4EE; D5=0; E5=0; F5=-9.6; G5=0; H5=0; I5=180; A6(AssemblyWasher)=Assembly.Washer; B6=True; C6=Asm4EE; D6=0; E6=0; F6=-9; G6=0; H6=0; I6=180; A7(AssemblyScrew019)=Assembly.Screw019; B7=True; C7=Asm4EE; D7=0; E7=0; F7=9; G7=0; H7=0; I7=0; A8(AssemblyScrew013)=Assembly.Screw013; B8=True; C8=Asm4EE; D8=0; E8=0; F8=0; G8=0; H8=-0; I8=-2.544443745170813e-14; A9(AssemblyScrew036)=Assembly.Screw036; B9=True; C9=Asm4EE; D9=0; E9=0; F9=0; G9=0; H9=0; I9=180; A10(AssemblyScrew035)=Assembly.Screw035; B10=True; C10=Asm4EE; D10=0; E10=0; F10=0; G10=0; H10=0; I10=180; A11(AssemblyScrew025)=Assembly.Screw025; B11=True; C11=Asm4EE; D11=0; E11=0; F11=0; G11=0; H11=0; I11=180; A12(AssemblyScrew024)=Assembly.Screw024; B12=True; C12=Asm4EE; D12=0; E12=0; F12=0; G12=0; H12=0; I12=180; A13(AssemblyScrew023)=Assembly.Screw023; B13=True; C13=Asm4EE; D13=0; E13=0; F13=0; G13=0; H13=0; I13=180; A14(AssemblyScrew022)=Assembly.Screw022; B14=True; C14=Asm4EE; D14=0; E14=0; F14=0; G14=0; H14=0; I14=180; A15(AssemblyScrew021)=Assembly.Screw021; B15=True; C15=Asm4EE; D15=0; E15=0; F15=0; G15=0; H15=0; I15=180; A16(AssemblyScrew020)=Assembly.Screw020; B16=True; C16=Asm4EE; D16=0; E16=0; F16=0; G16=0; H16=0; I16=180; A17(AssemblyScrew)=Assembly.Screw; B17=True; C17=Asm4EE; D17=0; E17=0; F17=0; G17=0; H17=0; I17=180; A18(AssemblyScrew032)=Assembly.Screw032; B18=True; C18=Asm4EE; D18=0; E18=0; F18=0; G18=0; H18=0; I18=180; A19(AssemblyScrew031)=Assembly.Screw031; B19=True; C19=Asm4EE; D19=0; E19=0; F19=0; G19=0; H19=0; I19=180; A20(AssemblyScrew030)=Assembly.Screw030; B20=True; C20=Asm4EE; D20=0; E20=0; F20=0; G20=0; H20=0; I20=180; A21(AssemblyScrew029)=Assembly.Screw029; B21=True; C21=Asm4EE; D21=0; E21=0; F21=0; G21=0; H21=0; I21=180; A22(AssemblyScrew028)=Assembly.Screw028; B22=True; C22=Asm4EE; D22=0; E22=0; F22=0; G22=0; H22=0; I22=180; A23(AssemblyScrew027)=Assembly.Screw027; B23=True; C23=Asm4EE; D23=0; E23=0; F23=0; G23=0; H23=0; I23=180; A24(AssemblyScrew026)=Assembly.Screw026; B24=True; C24=Asm4EE; D24=0; E24=0; F24=0; G24=0; H24=0; I24=180; A25(AssemblyScrew034)=Assembly.Screw034; B25=True; C25=Asm4EE; D25=0; E25=0; F25=0; G25=0; H25=0; I25=180; +318 more cells
FEATURE [Spreadsheet::Sheet] Printed_Parts
  cells = A1=Asm4::ConfigurationTable; A2=0; A4=ObjectName; B4=Visible; C4=Assembly Type; D4=Pos. X; E4=Pos. Y; F4=Pos. Z; G4=Rot. Yaw; H4=Rot. Pitch; I4=Rot. Roll; A5(AssemblyNut)=Assembly.Nut; B5=False; C5=Asm4EE; D5=0; E5=0; F5=-9.6; G5=0; H5=0; I5=180; A6(AssemblyWasher)=Assembly.Washer; B6=False; C6=Asm4EE; D6=0; E6=0; F6=-9; G6=0; H6=0; I6=180; A7(AssemblyScrew019)=Assembly.Screw019; B7=False; C7=Asm4EE; D7=0; E7=0; F7=9; G7=0; H7=0; I7=0; A8(AssemblyScrew013)=Assembly.Screw013; B8=False; C8=Asm4EE; D8=0; E8=0; F8=0; G8=0; H8=-0; I8=-2.544443745170813e-14; A9(AssemblyScrew036)=Assembly.Screw036; B9=False; C9=Asm4EE; D9=0; E9=0; F9=0; G9=0; H9=0; I9=180; A10(AssemblyScrew035)=Assembly.Screw035; B10=False; C10=Asm4EE; D10=0; E10=0; F10=0; G10=0; H10=0; I10=180; A11(AssemblyScrew025)=Assembly.Screw025; B11=False; C11=Asm4EE; D11=0; E11=0; F11=0; G11=0; H11=0; I11=180; A12(AssemblyScrew024)=Assembly.Screw024; B12=False; C12=Asm4EE; D12=0; E12=0; F12=0; G12=0; H12=0; I12=180; A13(AssemblyScrew023)=Assembly.Screw023; B13=False; C13=Asm4EE; D13=0; E13=0; F13=0; G13=0; H13=0; I13=180; A14(AssemblyScrew022)=Assembly.Screw022; B14=False; C14=Asm4EE; D14=0; E14=0; F14=0; G14=0; H14=0; I14=180; A15(AssemblyScrew021)=Assembly.Screw021; B15=False; C15=Asm4EE; D15=0; E15=0; F15=0; G15=0; H15=0; I15=180; A16(AssemblyScrew020)=Assembly.Screw020; B16=False; C16=Asm4EE; D16=0; E16=0; F16=0; G16=0; H16=0; I16=180; A17(AssemblyScrew)=Assembly.Screw; B17=False; C17=Asm4EE; D17=0; E17=0; F17=0; G17=0; H17=0; I17=180; A18(AssemblyScrew032)=Assembly.Screw032; B18=False; C18=Asm4EE; D18=0; E18=0; F18=0; G18=0; H18=0; I18=180; A19(AssemblyScrew031)=Assembly.Screw031; B19=False; C19=Asm4EE; D19=0; E19=0; F19=0; G19=0; H19=0; I19=180; A20(AssemblyScrew030)=Assembly.Screw030; B20=False; C20=Asm4EE; D20=0; E20=0; F20=0; G20=0; H20=0; I20=180; A21(AssemblyScrew029)=Assembly.Screw029; B21=False; C21=Asm4EE; D21=0; E21=0; F21=0; G21=0; H21=0; I21=180; A22(AssemblyScrew028)=Assembly.Screw028; B22=False; C22=Asm4EE; D22=0; E22=0; F22=0; G22=0; H22=0; I22=180; A23(AssemblyScrew027)=Assembly.Screw027; B23=False; C23=Asm4EE; D23=0; E23=0; F23=0; G23=0; H23=0; I23=180; A24(AssemblyScrew026)=Assembly.Screw026; B24=False; C24=Asm4EE; D24=0; E24=0; F24=0; G24=0; H24=0; I24=180; A25(AssemblyScrew034)=Assembly.Screw034; B25=False; C25=Asm4EE; D25=0; E25=0; F25=0; G25=0; H25=0; I25=180; +318 more cells
FEATURE [Spreadsheet::Sheet] Exploded_View
  cells = A1=Asm4::ConfigurationTable; A2=0; A4=ObjectName; B4=Visible; C4=Assembly Type; D4=Pos. X; E4=Pos. Y; F4=Pos. Z; G4=Rot. Yaw; H4=Rot. Pitch; I4=Rot. Roll; A5(AssemblyNut)=Assembly.Nut; B5=True; C5=Asm4EE; D5=0; E5=0; F5=-45; G5=0; H5=0; I5=180; A6(AssemblyWasher)=Assembly.Washer; B6=True; C6=Asm4EE; D6=0; E6=0; F6=-40; G6=0; H6=0; I6=180; A7(AssemblyScrew019)=Assembly.Screw019; B7=True; C7=Asm4EE; D7=0; E7=0; F7=45; G7=0; H7=0; I7=0; A8(AssemblyScrew013)=Assembly.Screw013; B8=True; C8=Asm4EE; D8=0; E8=0; F8=30; G8=0; H8=0; I8=0; A9(AssemblyScrew036)=Assembly.Screw036; B9=True; C9=Asm4EE; D9=0; E9=0; F9=-80; G9=0; H9=0; I9=180; A10(AssemblyScrew035)=Assembly.Screw035; B10=True; C10=Asm4EE; D10=0; E10=0; F10=-80; G10=0; H10=0; I10=180; A11(AssemblyScrew025)=Assembly.Screw025; B11=True; C11=Asm4EE; D11=0; E11=0; F11=-80; G11=0; H11=0; I11=180; A12(AssemblyScrew024)=Assembly.Screw024; B12=True; C12=Asm4EE; D12=0; E12=0; F12=-80; G12=0; H12=0; I12=180; A13(AssemblyScrew023)=Assembly.Screw023; B13=True; C13=Asm4EE; D13=0; E13=0; F13=-80; G13=0; H13=0; I13=180; A14(AssemblyScrew022)=Assembly.Screw022; B14=True; C14=Asm4EE; D14=0; E14=0; F14=-80; G14=0; H14=0; I14=180; A15(AssemblyScrew021)=Assembly.Screw021; B15=True; C15=Asm4EE; D15=0; E15=0; F15=-80; G15=0; H15=0; I15=180; A16(AssemblyScrew020)=Assembly.Screw020; B16=True; C16=Asm4EE; D16=0; E16=0; F16=-80; G16=0; H16=0; I16=180; A17(AssemblyScrew)=Assembly.Screw; B17=True; C17=Asm4EE; D17=0; E17=0; F17=-80; G17=0; H17=0; I17=180; A18(AssemblyScrew032)=Assembly.Screw032; B18=True; C18=Asm4EE; D18=0; E18=0; F18=-80; G18=0; H18=0; I18=180; A19(AssemblyScrew031)=Assembly.Screw031; B19=True; C19=Asm4EE; D19=0; E19=0; F19=-80; G19=0; H19=0; I19=180; A20(AssemblyScrew030)=Assembly.Screw030; B20=True; C20=Asm4EE; D20=0; E20=0; F20=-80; G20=0; H20=0; I20=180; A21(AssemblyScrew029)=Assembly.Screw029; B21=True; C21=Asm4EE; D21=0; E21=0; F21=-80; G21=0; H21=0; I21=180; A22(AssemblyScrew028)=Assembly.Screw028; B22=True; C22=Asm4EE; D22=0; E22=0; F22=-80; G22=0; H22=0; I22=180; A23(AssemblyScrew027)=Assembly.Screw027; B23=True; C23=Asm4EE; D23=0; E23=0; F23=-80; G23=0; H23=0; I23=180; A24(AssemblyScrew026)=Assembly.Screw026; B24=True; C24=Asm4EE; D24=0; E24=0; F24=-80; G24=0; H24=0; I24=180; A25(AssemblyScrew034)=Assembly.Screw034; B25=True; C25=Asm4EE; D25=40; E25=0; F25=-40; G25=0; H25=0; I25=180; +318 more cells
FEATURE [App::DocumentObjectGroup] Configurations
  Group = -> [Default,No_Dummy_Models,Printed_Parts,Exploded_View]
FEATURE [App::Part] Assembly
  AssemblyType = Part::Link
  Group = -> [LCS_Origin,Variables,Constraints,Configurations,LCS,Bodies,Base,Side,Rear,Handle,Parts,Fasteners,Rear001,Side001,Bottom,LCS_Assembly_Handle,Handle001,Master_Top_Sketch,LCS_Assembly_Tip_Cleaner,LCS_Assembly_Tip_Magazine,Sketch037,LCS_Assembly_Rear_Connector,LCS_Spool_Screw,LCS_Assembly_Spool,Tool_Holder,Tool_Holder_Adapter,Tool_Holder_Washer,Tool_Holder_Screw,Tip_Cleaner,Tip_Remover_Bracket,+69 more]
  Origin = -> Origin
  Type = Assembly
FEATURE [Spreadsheet::Sheet] Spreadsheet  label="BOM"
  cells = A1=Position; B1=Component; C1=Part Number / Specification; D1=Manufacturer; E1=Material; F1=Qty; G1=Description; A2=1; B2=Base Panel; C2=OpenSolder Stand Base Panel; D2=DIY; E2=ABS; F2=1; G2=Alternative material: Aluminium sheet; A3=2; B3=Side Panel; C3=OpenSolder Stand Side Panel; D3=DIY; E3=ABS; F3=1; G3=Alternative material: Aluminium sheet; A4=3; B4=Rear Panel; C4=OpenSolder Stand Rear Panel; D4=DIY; E4=ABS; F4=1; G4=Alternative material: Aluminium sheet; A5=4; B5=Mid Panel; C5=OpenSolder Stand Mid Panel; D5=DIY; E5=ABS; F5=1; G5=Alternative material: Aluminium sheet; A6=5; B6=Handle; C6=OpenSolder Stand Handle; D6=DIY; E6=ABS; F6=1; A7=6; B7=Tool Holder SCD; C7=12994; D7=JBC; E7=-; F7=1; A8=7; B8=Tool Holder Adapter; C8=OpenSolder Tool Holder Adapter; D8=DIY; E8=ABS; F8=1; A9=8; B9=Tool Holder Washer; C9=OpenSolder Tool Holder Washer; D9=DIY; E9=ABS; F9=1; A10=9; B10=Spool Knob; C10=OpenSolder Spool Knob; D10=DIY; E10=ABS; F10=1; A11=10; B11=Tip Magazine; C11=OpenSolder Tip Magazine; D11=DIY; E11=ABS; F11=1; A12=11; B12=Tip Cleaner; C12=OpenSolder Tip Cleaner; D12=DIY; E12=ABS; F12=1; A13=12; B13=Tip Remover Bracket; C13=OpenSolder Tip Remover Bracket; D13=DIY; E13=Aluminium; F13=1; A14=13; B14=Connector; C14=MJ-064H; D14=Marushin Electric; E14=-; F14=1; A15=14; B15=Rubber Pads; C15=Self adhesive; D15=-; E15=-; F15=4; A16=15; B16=CS Flat Head Screw M3X8; C16=ISO 10642; D16=-; E16=-; F16=3; A17=16; B17=CS Flat Head Screw M3X16; C17=ISO 10642; D17=-; E17=-; F17=15; A18=17; B18=Socket Head Cap Screw M3x25; C18=ISO 4762; D18=-; E18=-; F18=1; A19=18; B19=Washer M3; C19=ISO 7089; D19=-; E19=-; F19=1; A20=19; B20=Locknut M3; C20=ISO 10511; D20=-; E20=-; F20=1; A21=20; B21=Hexagon Screw M10x80; C21=ISO 4014; D21=-; E21=-; F21=1
FEATURE [TechDraw::DrawSVGTemplate] Template
  EditableTexts = AUTHOR_NAME=Håvard Jakobsen; DN=-; DRAWING_TITLE=OpenSolder Stand Assembly Drawing; FC-DATE=20220501; FC-REV=REV 1; FC-SC=1:2; FC-SH=1/3; FC-SI=A3; PN=-; SI-1=Assembled station overview; SI-5=https://github.com/<owner>/OpenSolder; SI-6=Licence: GPL-3.0
  Height = 297
  Orientation = 1
  Width = 420
FEATURE [TechDraw::DrawProjGroupItem] ProjItem  label="Front"
  CoarseView = false
  Direction = (0,-1,0)
  Focus = 100
  HardHidden = false
  IsoCount = 0
  IsoHidden = false
  IsoVisible = false
  LockPosition = true
  Perspective = false
  Rotation = 0
  RotationVector = (1,0,0)
  Scale = 0.5
  ScaleType = 2
  SeamHidden = false
  SeamVisible = true
  SmoothHidden = false
  SmoothVisible = true
  Source = -> [Assembly]
  Type = 0
  X = 0
  XDirection = (1,0,0)
  Y = 0
FEATURE [TechDraw::DrawProjGroupItem] ProjItem001  label="Right"
  CoarseView = false
  Direction = (1,-1e-16,0)
  Focus = 100
  HardHidden = false
  IsoCount = 0
  IsoHidden = false
  IsoVisible = false
  LockPosition = false
  Perspective = false
  Rotation = 0
  RotationVector = (1,0,0)
  Scale = 0.5
  ScaleType = 2
  SeamHidden = false
  SeamVisible = true
  SmoothHidden = false
  SmoothVisible = true
  Source = -> [Assembly]
  Type = 2
  X = -115.824
  XDirection = (1e-16,1,0)
  Y = 0
FEATURE [TechDraw::DrawProjGroupItem] ProjItem002  label="Left"
  CoarseView = false
  Direction = (-1,-1e-16,0)
  Focus = 100
  HardHidden = false
  IsoCount = 0
  IsoHidden = false
  IsoVisible = false
  LockPosition = false
  Perspective = false
  Rotation = 0
  RotationVector = (1,0,0)
  Scale = 0.5
  ScaleType = 2
  SeamHidden = false
  SeamVisible = true
  SmoothHidden = false
  SmoothVisible = true
  Source = -> [Assembly]
  Type = 1
  X = 115.67
  XDirection = (1e-16,-1,0)
  Y = 0
FEATURE [TechDraw::DrawProjGroup] ProjGroup
  Anchor = -> ProjItem
  AutoDistribute = true
  LockPosition = true
  ProjectionType = 0
  Rotation = 0
  ScaleType = 0
  Source = -> [Assembly]
  Views = -> [ProjItem,ProjItem001,ProjItem002]
  X = 215
  Y = 225
  spacingX = 0
  spacingY = 0
FEATURE [TechDraw::DrawViewPart] View
  CoarseView = false
  Direction = (0.616,-0.764,0.19)
  Focus = 100
  HardHidden = false
  IsoCount = 0
  IsoHidden = false
  IsoVisible = false
  LockPosition = true
  Perspective = false
  Rotation = 0
  Scale = 0.75
  ScaleType = 2
  SeamHidden = false
  SeamVisible = true
  SmoothHidden = false
  SmoothVisible = true
  Source = -> [Assembly]
  X = 110
  XDirection = (0.778,0.628,0)
  Y = 90
FEATURE [TechDraw::DrawViewDimension] Dimension
  AngleOverride = false
  Arbitrary = false
  ArbitraryTolerances = false
  EqualTolerance = true
  ExtensionAngle = 0
  FormatSpec = %.2f
  FormatSpecOverTolerance = %+.2f
  FormatSpecUnderTolerance = %+.2f
  Inverted = false
  LineAngle = 0
  LockPosition = false
  MeasureType = 1
  OverTolerance = 0
  References2D = -> [ProjItem002]
  Rotation = 0
  ScaleType = 1
  TheoreticalExact = false
  Type = 1
  UnderTolerance = 0
  X = -10
  Y = -35
FEATURE [TechDraw::DrawViewDimension] Dimension001
  AngleOverride = false
  Arbitrary = false
  ArbitraryTolerances = false
  EqualTolerance = true
  ExtensionAngle = 0
  FormatSpec = %.2f
  FormatSpecOverTolerance = %+.2f
  FormatSpecUnderTolerance = %+.2f
  Inverted = false
  LineAngle = 0
  LockPosition = false
  MeasureType = 1
  OverTolerance = 0
  References2D = -> [ProjItem]
  Rotation = 0
  ScaleType = 1
  TheoreticalExact = false
  Type = 1
  UnderTolerance = 0
  X = 5
  Y = -35
FEATURE [TechDraw::DrawViewDimension] Dimension003
  AngleOverride = false
  Arbitrary = false
  ArbitraryTolerances = false
  EqualTolerance = true
  ExtensionAngle = 0
  FormatSpec = %.2f
  FormatSpecOverTolerance = %+.2f
  FormatSpecUnderTolerance = %+.2f
  Inverted = false
  LineAngle = 0
  LockPosition = false
  MeasureType = 1
  OverTolerance = 0
  References2D = -> [ProjItem]
  Rotation = 0
  ScaleType = 1
  TheoreticalExact = false
  Type = 2
  UnderTolerance = 0
  X = 40
  Y = 3
FEATURE [TechDraw::DrawViewBalloon] Balloon
  BubbleShape = 6
  EndType = 0
  EndTypeScale = 1
  KinkLength = 5
  LockPosition = false
  OriginX = 394
  OriginY = 5.91833
  Rotation = 0
  ScaleType = 1
  ShapeScale = 1
  SourceView = -> ProjItem001
  Text = Solder wire spool holder
  TextWrapLen = 30
  X = 316.198
  Y = 95
FEATURE [TechDraw::DrawViewBalloon] Balloon001
  BubbleShape = 6
  EndType = 0
  EndTypeScale = 1
  KinkLength = 5
  LockPosition = false
  OriginX = 11.8228
  OriginY = -44.0485
  Rotation = 0
  ScaleType = 1
  ShapeScale = 1
  SourceView = -> ProjItem001
  Text = Tip magazine
  TextWrapLen = -1
  X = -80
  Y = -120
FEATURE [TechDraw::DrawViewBalloon] Balloon002
  BubbleShape = 6
  EndType = 0
  EndTypeScale = 1
  KinkLength = 5
  LockPosition = false
  OriginX = 45
  OriginY = 50
  Rotation = 0
  ScaleType = 1
  ShapeScale = 1
  SourceView = -> ProjItem002
  Text = Adjustable tool holder angle
  TextWrapLen = 35
  X = 115
  Y = 95
FEATURE [TechDraw::DrawViewBalloon] Balloon003
  BubbleShape = 6
  EndType = 0
  EndTypeScale = 1
  KinkLength = 5
  LockPosition = false
  OriginX = -52.6535
  OriginY = -13.27
  Rotation = 0
  ScaleType = 1
  ShapeScale = 1
  SourceView = -> ProjItem
  Text = Tip remover with sensor
  TextWrapLen = -1
  X = -181.872
  Y = 95
FEATURE [TechDraw::DrawPage] Page  label="Page_1"
  KeepUpdated = false
  NextBalloonIndex = 6
  ProjectionType = 0
  Scale = 0.5
  Template = -> Template
  Views = -> [ProjGroup,View,Dimension,Dimension001,Dimension003,Balloon,Balloon001,Balloon002,Balloon003]
FEATURE [TechDraw::DrawSVGTemplate] Template002
  EditableTexts = AUTHOR_NAME=Håvard Jakobsen; DN=-; DRAWING_TITLE=OpenSolder Stand Assembly Drawing; FC-DATE=20220501; FC-REV=REV 1; FC-SC=1:1; FC-SH=3/3; FC-SI=A3; PN=-; SI-1=Bill of Materials; SI-5=https://github.com/<owner>/OpenSolder; SI-6=Licence: GPL-3.0
  Height = 297
  Orientation = 1
  Width = 420
FEATURE [TechDraw::DrawViewSpreadsheet] Sheet
  CellEnd = G21
  CellStart = A1
  Font = osifont
  LineWidth = 0.35
  LockPosition = true
  Rotation = 0
  Scale = 1.2
  ScaleType = 2
  Source = -> Spreadsheet
  Symbol = <blob: 30012 chars omitted>
  TextSize = 12
  X = 215
  Y = 180
FEATURE [TechDraw::DrawPage] Page002  label="Page_3"
  KeepUpdated = false
  NextBalloonIndex = 1
  ProjectionType = 0
  Template = -> Template002
  Views = -> [Sheet]
FEATURE [TechDraw::DrawSVGTemplate] Template003
  EditableTexts = AUTHOR_NAME=Håvard Jakobsen; DN=-; DRAWING_TITLE=OpenSolder Stand Assembly Drawing; FC-DATE=20220501; FC-REV=REV 1; FC-SC=1:2; FC-SH=2/3; FC-SI=A3; PN=-; SI-1=Exploded view; SI-5=https://github.com/<owner>/OpenSolder; SI-6=Licence: GPL-3.0
  Height = 297
  Orientation = 1
  Width = 420
FEATURE [TechDraw::DrawViewPart] View001
  CoarseView = false
  Direction = (0.577,-0.577,0.577)
  Focus = 100
  HardHidden = false
  IsoCount = 0
  IsoHidden = false
  IsoVisible = false
  LockPosition = true
  Perspective = false
  Rotation = 0
  ScaleType = 0
  SeamHidden = false
  SeamVisible = true
  SmoothHidden = false
  SmoothVisible = true
  Source = -> [Assembly]
  X = 130
  XDirection = (0.707,0.707,0)
  Y = 180
FEATURE [TechDraw::DrawViewPart] View002
  CoarseView = false
  Direction = (-0.577,0.577,-0.577)
  Focus = 100
  HardHidden = false
  IsoCount = 0
  IsoHidden = false
  IsoVisible = false
  LockPosition = true
  Perspective = false
  Rotation = 0
  ScaleType = 0
  SeamHidden = false
  SeamVisible = true
  SmoothHidden = false
  SmoothVisible = true
  Source = -> [Assembly]
  X = 320
  XDirection = (-0.707,-0.707,0)
  Y = 180
FEATURE [TechDraw::DrawViewBalloon] Balloon004
  BubbleShape = 0
  EndType = 0
  EndTypeScale = 1
  KinkLength = 5
  LockPosition = false
  OriginX = 22.4065
  OriginY = -58.8515
  Rotation = 0
  ScaleType = 1
  ShapeScale = 1
  SourceView = -> View001
  Text = 1
  TextWrapLen = -1
  X = 112.999
  Y = -86.4144
FEATURE [TechDraw::DrawViewBalloon] Balloon005
  BubbleShape = 0
  EndType = 0
  EndTypeScale = 1
  KinkLength = 5
  LockPosition = false
  OriginX = -70.806
  OriginY = 75.9429
  Rotation = 0
  ScaleType = 1
  ShapeScale = 1
  SourceView = -> View001
  Text = 2
  TextWrapLen = -1
  X = -107.728
  Y = 147.489
FEATURE [TechDraw::DrawViewBalloon] Balloon008
  BubbleShape = 0
  EndType = 0
  EndTypeScale = 1
  KinkLength = 5
  LockPosition = false
  OriginX = -16.4216
  OriginY = 125.214
  Rotation = 0
  ScaleType = 1
  ShapeScale = 1
  SourceView = -> View001
  Text = 5
  TextWrapLen = -1
  X = -57.2729
  Y = 159.611
FEATURE [TechDraw::DrawViewBalloon] Balloon009
  BubbleShape = 0
  EndType = 0
  EndTypeScale = 1
  KinkLength = 5
  LockPosition = false
  OriginX = -140.013
  OriginY = 90.135
  Rotation = 0
  ScaleType = 1
  ShapeScale = 1
  SourceView = -> View001
  Text = 6
  TextWrapLen = -1
  X = -197.259
  Y = 111.823
FEATURE [TechDraw::DrawViewBalloon] Balloon010
  BubbleShape = 0
  EndType = 0
  EndTypeScale = 1
  KinkLength = 5
  LockPosition = false
  OriginX = -58.9264
  OriginY = 48.9035
  Rotation = 0
  ScaleType = 1
  ShapeScale = 1
  SourceView = -> View001
  Text = 7
  TextWrapLen = -1
  X = -200.89
  Y = 73.4913
FEATURE [TechDraw::DrawViewBalloon] Balloon011
  BubbleShape = 0
  EndType = 0
  EndTypeScale = 1
  KinkLength = 5
  LockPosition = false
  OriginX = -94.2661
  OriginY = 75.4622
  Rotation = 0
  ScaleType = 1
  ShapeScale = 1
  SourceView = -> View001
  Text = 8
  TextWrapLen = -1
  X = -127.927
  Y = 124.816
FEATURE [TechDraw::DrawViewBalloon] Balloon013
  BubbleShape = 0
  EndType = 0
  EndTypeScale = 1
  KinkLength = 5
  LockPosition = false
  OriginX = -131.97
  OriginY = 13.7834
  Rotation = 0
  ScaleType = 1
  ShapeScale = 1
  SourceView = -> View001
  Text = 12
  TextWrapLen = -1
  X = -200.639
  Y = -31.1814
FEATURE [TechDraw::DrawViewBalloon] Balloon015
  BubbleShape = 0
  EndType = 0
  EndTypeScale = 1
  KinkLength = 5
  LockPosition = false
  OriginX = 87.559
  OriginY = -76.6163
  Rotation = 0
  ScaleType = 1
  ShapeScale = 1
  SourceView = -> View002
  Text = 14
  TextWrapLen = -1
  X = 143.392
  Y = -109.205
FEATURE [TechDraw::DrawViewBalloon] Balloon016
  BubbleShape = 0
  EndType = 0
  EndTypeScale = 1
  KinkLength = 5
  LockPosition = false
  OriginX = 62.6178
  OriginY = -105.098
  Rotation = 0
  ScaleType = 1
  ShapeScale = 1
  SourceView = -> View002
  Text = 15
  TextWrapLen = -1
  X = 123.698
  Y = -146.216
FEATURE [TechDraw::DrawViewBalloon] Balloon017
  BubbleShape = 0
  EndType = 0
  EndTypeScale = 1
  KinkLength = 5
  LockPosition = false
  OriginX = -54.5799
  OriginY = -92.532
  Rotation = 0
  ScaleType = 1
  ShapeScale = 1
  SourceView = -> View002
  Text = 16
  TextWrapLen = -1
  X = -106.419
  Y = -117.46
FEATURE [TechDraw::DrawViewBalloon] Balloon018
  BubbleShape = 0
  EndType = 0
  EndTypeScale = 1
  KinkLength = 5
  LockPosition = false
  OriginX = -144.118
  OriginY = 41.7959
  Rotation = 0
  ScaleType = 1
  ShapeScale = 1
  SourceView = -> View001
  Text = 17
  TextWrapLen = -1
  X = -199.931
  Y = 39.2604
FEATURE [TechDraw::DrawViewBalloon] Balloon019
  BubbleShape = 0
  EndType = 0
  EndTypeScale = 1
  KinkLength = 5
  LockPosition = false
  OriginX = -89.5503
  OriginY = 9.42549
  Rotation = 0
  ScaleType = 1
  ShapeScale = 1
  SourceView = -> View001
  Text = 18
  TextWrapLen = -1
  X = -163.409
  Y = -51.1547
FEATURE [TechDraw::DrawViewBalloon] Balloon020
  BubbleShape = 0
  EndType = 0
  EndTypeScale = 1
  KinkLength = 5
  LockPosition = false
  OriginX = -83.1635
  OriginY = 6.60728
  Rotation = 0
  ScaleType = 1
  ShapeScale = 1
  SourceView = -> View001
  Text = 19
  TextWrapLen = -1
  X = -138.071
  Y = -73.643
FEATURE [TechDraw::DrawViewBalloon] Balloon021
  BubbleShape = 0
  EndType = 0
  EndTypeScale = 1
  KinkLength = 5
  LockPosition = false
  OriginX = -144.671
  OriginY = 108.59
  Rotation = 0
  ScaleType = 1
  ShapeScale = 1
  SourceView = -> View002
  Text = 20
  TextWrapLen = -1
  X = -178.055
  Y = 146.517
FEATURE [TechDraw::DrawViewBalloon] Balloon022
  BubbleShape = 0
  EndType = 0
  EndTypeScale = 1
  KinkLength = 5
  LockPosition = false
  OriginX = -79.4164
  OriginY = 81.126
  Rotation = 0
  ScaleType = 1
  ShapeScale = 1
  SourceView = -> View002
  Text = 9
  TextWrapLen = -1
  X = -113.089
  Y = 146.052
FEATURE [TechDraw::DrawViewBalloon] Balloon023
  BubbleShape = 0
  EndType = 0
  EndTypeScale = 1
  KinkLength = 5
  LockPosition = false
  OriginX = 22.4065
  OriginY = -18.8432
  Rotation = 0
  ScaleType = 1
  ShapeScale = 1
  SourceView = -> View001
  Text = 10
  TextWrapLen = -1
  X = 131.548
  Y = -45.5156
FEATURE [TechDraw::DrawViewBalloon] Balloon024
  BubbleShape = 0
  EndType = 0
  EndTypeScale = 1
  KinkLength = 5
  LockPosition = false
  OriginX = -57.4687
  OriginY = 54.4723
  Rotation = 0
  ScaleType = 1
  ShapeScale = 1
  SourceView = -> View002
  Text = 13
  TextWrapLen = -1
  X = -22.0405
  Y = 168.637
FEATURE [TechDraw::DrawViewBalloon] Balloon025
  BubbleShape = 0
  EndType = 0
  EndTypeScale = 1
  KinkLength = 5
  LockPosition = false
  OriginX = -2.60755
  OriginY = -92.3278
  Rotation = 0
  ScaleType = 1
  ShapeScale = 1
  SourceView = -> View002
  Text = 16
  TextWrapLen = -1
  X = -46.4244
  Y = -136.145
FEATURE [TechDraw::DrawViewBalloon] Balloon026
  BubbleShape = 0
  EndType = 0
  EndTypeScale = 1
  KinkLength = 5
  LockPosition = false
  OriginX = 148.759
  OriginY = -8.30148
  Rotation = 0
  ScaleType = 1
  ShapeScale = 1
  SourceView = -> View002
  Text = 16
  TextWrapLen = -1
  X = 139.485
  Y = -56.1821
FEATURE [TechDraw::DrawViewBalloon] Balloon027
  BubbleShape = 0
  EndType = 0
  EndTypeScale = 1
  KinkLength = 5
  LockPosition = false
  OriginX = -140.869
  OriginY = 24.8318
  Rotation = 0
  ScaleType = 1
  ShapeScale = 1
  SourceView = -> View001
  Text = 15
  TextWrapLen = -1
  X = -200.701
  Y = 3.80357
FEATURE [TechDraw::DrawViewBalloon] Balloon028
  BubbleShape = 0
  EndType = 0
  EndTypeScale = 1
  KinkLength = 5
  LockPosition = false
  OriginX = 3.44295
  OriginY = 12.133
  Rotation = 0
  ScaleType = 1
  ShapeScale = 1
  SourceView = -> View001
  Text = 6
  TextWrapLen = -1
  X = 140.1
  Y = 3.80425
FEATURE [TechDraw::DrawViewBalloon] Balloon029
  BubbleShape = 0
  EndType = 0
  EndTypeScale = 1
  KinkLength = 5
  LockPosition = false
  OriginX = 70.305
  OriginY = 29.9231
  Rotation = 0
  ScaleType = 1
  ShapeScale = 1
  SourceView = -> View001
  Text = 3
  TextWrapLen = -1
  X = 159.692
  Y = 39.5854
FEATURE [TechDraw::DrawViewBalloon] Balloon030
  BubbleShape = 0
  EndType = 0
  EndTypeScale = 1
  KinkLength = 5
  LockPosition = false
  OriginX = 7.33004
  OriginY = 45.27
  Rotation = 0
  ScaleType = 1
  ShapeScale = 1
  SourceView = -> View001
  Text = 4
  TextWrapLen = -1
  X = 65.6738
  Y = 113.138
FEATURE [TechDraw::DrawViewBalloon] Balloon031
  BubbleShape = 0
  EndType = 0
  EndTypeScale = 1
  KinkLength = 5
  LockPosition = false
  OriginX = -73.76
  OriginY = -39.2556
  Rotation = 0
  ScaleType = 1
  ShapeScale = 1
  SourceView = -> View001
  Text = 11
  TextWrapLen = -1
  X = -130.77
  Y = -126.251
FEATURE [TechDraw::DrawViewBalloon] Balloon032
  BubbleShape = 0
  EndType = 0
  EndTypeScale = 1
  KinkLength = 5
  LockPosition = false
  OriginX = -18.6633
  OriginY = 126.967
  Rotation = 0
  ScaleType = 1
  ShapeScale = 1
  SourceView = -> View002
  Text = 16
  TextWrapLen = -1
  X = 40.0332
  Y = 169.789
FEATURE [TechDraw::DrawViewSymbol] Symbol
  Caption = MJ-064H Connector (13)
  LockPosition = true
  Rotation = 0
  ScaleType = 2
  Symbol = <?xml version="1.0"?>\n<svg xmlns="http://www.w3.org/2000/svg" xmlns:lc="https://librecad.org" xmlns:xlink="http://www.w3.org/1999/xlink" width="40mm" height="40mm" viewBox="0 0 40 40">\n    <g lc:layername="0" lc:is_locked="false" lc:is_construction="false" fill="none" stroke="black" stroke-width="0.2"/>\n    <g lc:layername="Lines" lc:is_locked="false" lc:is_construction="false" fill="none" stroke="black" stroke-width="0.2">\n        <circle cx="20" cy="20" r="20"/>\n        <line x1="15" y1="30" x2="25" y2="30"/>\n        <line x1="25" y1="30" x2="25" y2="31"/>\n        <line x1="25" y1="31" x2="15" y2="31"/>\n        <line x1="15" y1="31" x2="15" y2="30"/>\n        <line x1="30" y1="17" x2="31" y2="17"/>\n        <line x1="31" y1="17" x2="31" y2="23"/>\n        <line x1="31" y1="23" x2="30" y2="23"/>\n        <line x1="30" y1="17" x2="30" y2="23"/>\n        <line x1="10" y1="17" x2="9" y2="17"/>\n        <line x1="9" y1="17" x2="9" y2="23"/>\n        <line x1="9" y1="23" x2="10" y2="23"/>\n        <line x1="10" y1="17" x2="10" y2="23"/>\n        <line x1="17" y1="10" x2="17" y2="9"/>\n        <line x1="17" y1="9" x2="23" y2="9"/>\n        <line x1="23" y1="9" x2="23" y2="10"/>\n        <line x1="17" y1="10" x2="23" y2="10"/>\n    </g>\n</svg>
  X = 60
  Y = 60
FEATURE [TechDraw::DrawViewBalloon] Balloon035
  BubbleShape = 6
  EndType = 0
  EndTypeScale = 1
  KinkLength = 5
  LockPosition = false
  OriginX = -130
  OriginY = -260
  Rotation = 0
  ScaleType = 1
  ShapeScale = 1
  SourceView = -> View001
  Text = Connect to tool holder (6)
  TextWrapLen = -1
  X = 30
  Y = -280
FEATURE [TechDraw::DrawViewBalloon] Balloon036
  BubbleShape = 6
  EndType = 0
  EndTypeScale = 1
  KinkLength = 5
  LockPosition = false
  OriginX = -158
  OriginY = -240
  Rotation = 0
  ScaleType = 1
  ShapeScale = 1
  SourceView = -> View001
  Text = Connect to tip remover (12) using a ring terminal under washer (18)
  TextWrapLen = 75
  X = 48
  Y = -200
FEATURE [TechDraw::DrawPage] Page003  label="Page_2"
  KeepUpdated = false
  NextBalloonIndex = 36
  ProjectionType = 0
  Scale = 0.5
  Template = -> Template003
  Views = -> [View001,View002,Balloon004,Balloon005,Balloon008,Balloon009,Balloon010,Balloon011,Balloon013,Balloon015,Balloon016,Balloon017,Balloon018,Balloon019,Balloon020,Balloon021,Balloon022,Balloon023,Balloon024,Balloon025,Balloon026,Balloon027,Balloon028,Balloon029,Balloon030,Balloon031,Balloon032,Symbol,Balloon035,Balloon036]
FEATURE [App::DocumentObjectGroup] Drawings
  Group = -> [Page,Page003,Page002]
